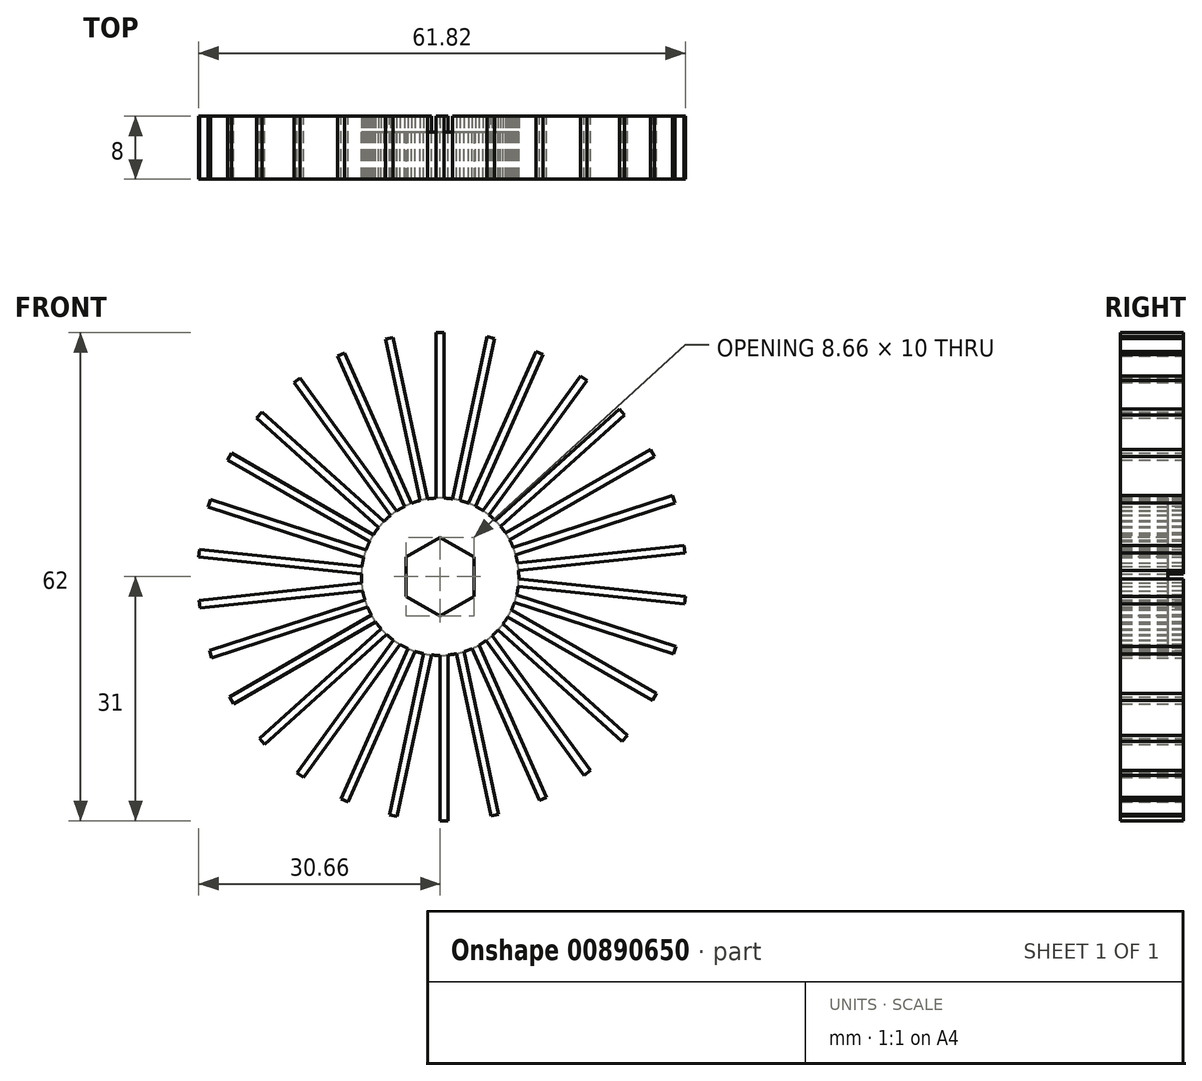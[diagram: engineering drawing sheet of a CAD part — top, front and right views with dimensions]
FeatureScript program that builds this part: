
annotation { "Feature Type Name" : "Feature", "Feature Type Description" : "" }
export const myFeature = defineFeature(function(context is Context, id is Id, definition is map)
    precondition{}
    {
        {
            var Q0;
            Q0=qCreatedBy(makeId("Front.planeOp"),FACE);
            var sketch = newSketch(context, id + "F0", { "sketchPlane" : qUnion([Q0])});
            skCircle(sketch, "E0", {"center": v(0, 0) * mm, "radius": 10 * mm});
            skCircle(sketch, "E1", {"center": v(0, 0) * mm, "radius": 5 * mm});
            skCircle(sketch, "E2.cCircle", {"center": v(0, 0) * mm, "radius": 5 * mm, "construction": true});
            skLineSegment(sketch, "E2.0", {"start": v(0, 5) * mm, "end": v(4.33, 2.5) * mm});
            skLineSegment(sketch, "E2.1", {"start": v(4.33, 2.5) * mm, "end": v(4.33, -2.5) * mm});
            skLineSegment(sketch, "E2.2", {"start": v(4.33, -2.5) * mm, "end": v(0, -5) * mm});
            skLineSegment(sketch, "E2.3", {"start": v(0, -5) * mm, "end": v(-4.33, -2.5) * mm});
            skLineSegment(sketch, "E2.4", {"start": v(-4.33, -2.5) * mm, "end": v(-4.33, 2.5) * mm});
            skLineSegment(sketch, "E2.5", {"start": v(-4.33, 2.5) * mm, "end": v(0, 5) * mm});
            skLineSegment(sketch, "E3", {"start": v(-0.5, 31) * mm, "end": v(0.5, 31) * mm});
            skLineSegment(sketch, "E4", {"start": v(0.5, 31) * mm, "end": v(0.5, 0) * mm});
            skLineSegment(sketch, "E5", {"start": v(-0.5, 31) * mm, "end": v(-0.5, 0) * mm});
            skLineSegment(sketch, "E6.1.0", {"start": v(-5.95, 30.37) * mm, "end": v(0.5, 0.05) * mm});
            skLineSegment(sketch, "E6.1.1", {"start": v(-6.93, 30.17) * mm, "end": v(-0.48, -0.16) * mm});
            skLineSegment(sketch, "E6.1.2", {"start": v(-6.93, 30.17) * mm, "end": v(-5.95, 30.37) * mm});
            skLineSegment(sketch, "E6.2.0", {"start": v(-12.13, 28.42) * mm, "end": v(0.48, 0.1) * mm});
            skLineSegment(sketch, "E6.2.1", {"start": v(-13.04, 28.01) * mm, "end": v(-0.44, -0.3) * mm});
            skLineSegment(sketch, "E6.2.2", {"start": v(-13.04, 28.01) * mm, "end": v(-12.13, 28.42) * mm});
            skLineSegment(sketch, "E6.3.0", {"start": v(-17.77, 25.23) * mm, "end": v(0.45, 0.15) * mm});
            skLineSegment(sketch, "E6.3.1", {"start": v(-18.58, 24.64) * mm, "end": v(-0.36, -0.44) * mm});
            skLineSegment(sketch, "E6.3.2", {"start": v(-18.58, 24.64) * mm, "end": v(-17.77, 25.23) * mm});
            skLineSegment(sketch, "E6.4.0", {"start": v(-22.62, 20.93) * mm, "end": v(0.42, 0.19) * mm});
            skLineSegment(sketch, "E6.4.1", {"start": v(-23.29, 20.19) * mm, "end": v(-0.25, -0.56) * mm});
            skLineSegment(sketch, "E6.4.2", {"start": v(-23.29, 20.19) * mm, "end": v(-22.62, 20.93) * mm});
            skLineSegment(sketch, "E6.5.0", {"start": v(-26.47, 15.72) * mm, "end": v(0.38, 0.22) * mm});
            skLineSegment(sketch, "E6.5.1", {"start": v(-26.97, 14.85) * mm, "end": v(-0.12, -0.65) * mm});
            skLineSegment(sketch, "E6.5.2", {"start": v(-26.97, 14.85) * mm, "end": v(-26.47, 15.72) * mm});
            skPoint(sketch, "E6.center", {"position": v(0.25, 0) * mm});
            skLineSegment(sketch, "E7.3.6.0", {"start": v(-29.46, 8.87) * mm, "end": v(0.02, -0.71) * mm});
            skLineSegment(sketch, "E7.5.6.0", {"start": v(-29.16, 9.82) * mm, "end": v(0.33, 0.24) * mm});
            skLineSegment(sketch, "E7.6.6.0", {"start": v(-29.46, 8.87) * mm, "end": v(-29.16, 9.82) * mm});
            skLineSegment(sketch, "E7.3.7.0", {"start": v(-30.66, 2.5) * mm, "end": v(0.17, -0.75) * mm});
            skLineSegment(sketch, "E7.5.7.0", {"start": v(-30.55, 3.49) * mm, "end": v(0.28, 0.25) * mm});
            skLineSegment(sketch, "E7.6.7.0", {"start": v(-30.66, 2.5) * mm, "end": v(-30.55, 3.49) * mm});
            skLineSegment(sketch, "E7.3.8.0", {"start": v(-30.5, -3.99) * mm, "end": v(0.33, -0.75) * mm});
            skLineSegment(sketch, "E7.5.8.0", {"start": v(-30.6, -3) * mm, "end": v(0.22, 0.25) * mm});
            skLineSegment(sketch, "E7.6.8.0", {"start": v(-30.5, -3.99) * mm, "end": v(-30.6, -3) * mm});
            skLineSegment(sketch, "E7.3.9.0", {"start": v(-29, -10.3) * mm, "end": v(0.48, -0.71) * mm});
            skLineSegment(sketch, "E7.5.9.0", {"start": v(-29.31, -9.34) * mm, "end": v(0.17, 0.24) * mm});
            skLineSegment(sketch, "E7.6.9.0", {"start": v(-29, -10.3) * mm, "end": v(-29.31, -9.34) * mm});
            skLineSegment(sketch, "E7.3.10.0", {"start": v(-26.22, -16.15) * mm, "end": v(0.63, -0.65) * mm});
            skLineSegment(sketch, "E7.5.10.0", {"start": v(-26.72, -15.28) * mm, "end": v(0.13, 0.22) * mm});
            skLineSegment(sketch, "E7.6.10.0", {"start": v(-26.22, -16.15) * mm, "end": v(-26.72, -15.28) * mm});
            skLineSegment(sketch, "E7.3.11.0", {"start": v(-22.29, -21.3) * mm, "end": v(0.75, -0.56) * mm});
            skLineSegment(sketch, "E7.5.11.0", {"start": v(-22.95, -20.56) * mm, "end": v(0.08, 0.19) * mm});
            skLineSegment(sketch, "E7.6.11.0", {"start": v(-22.29, -21.3) * mm, "end": v(-22.95, -20.56) * mm});
            skLineSegment(sketch, "E8.3.12.0", {"start": v(-17.36, -25.52) * mm, "end": v(0.86, -0.44) * mm});
            skLineSegment(sketch, "E8.5.12.0", {"start": v(-18.17, -24.93) * mm, "end": v(0.05, 0.15) * mm});
            skLineSegment(sketch, "E8.6.12.0", {"start": v(-17.36, -25.52) * mm, "end": v(-18.17, -24.93) * mm});
            skLineSegment(sketch, "E8.3.13.0", {"start": v(-11.67, -28.62) * mm, "end": v(0.94, -0.3) * mm});
            skLineSegment(sketch, "E8.5.13.0", {"start": v(-12.59, -28.22) * mm, "end": v(0.02, 0.1) * mm});
            skLineSegment(sketch, "E8.6.13.0", {"start": v(-11.67, -28.62) * mm, "end": v(-12.59, -28.22) * mm});
            skLineSegment(sketch, "E8.3.14.0", {"start": v(-5.46, -30.48) * mm, "end": v(0.98, -0.16) * mm});
            skLineSegment(sketch, "E8.5.14.0", {"start": v(-6.44, -30.27) * mm, "end": v(0, 0.05) * mm});
            skLineSegment(sketch, "E8.6.14.0", {"start": v(-5.46, -30.48) * mm, "end": v(-6.44, -30.27) * mm});
            skLineSegment(sketch, "E8.3.15.0", {"start": v(1, -31) * mm, "end": v(1, 0) * mm});
            skLineSegment(sketch, "E8.5.15.0", {"start": v(0, -31) * mm, "end": v(0, 0) * mm});
            skLineSegment(sketch, "E8.6.15.0", {"start": v(1, -31) * mm, "end": v(0, -31) * mm});
            skLineSegment(sketch, "E8.3.16.0", {"start": v(7.43, -30.17) * mm, "end": v(0.98, 0.16) * mm});
            skLineSegment(sketch, "E8.5.16.0", {"start": v(6.45, -30.37) * mm, "end": v(0, -0.05) * mm});
            skLineSegment(sketch, "E8.6.16.0", {"start": v(7.43, -30.17) * mm, "end": v(6.45, -30.37) * mm});
            skLineSegment(sketch, "E8.3.17.0", {"start": v(13.54, -28.01) * mm, "end": v(0.94, 0.3) * mm});
            skLineSegment(sketch, "E8.5.17.0", {"start": v(12.63, -28.42) * mm, "end": v(0.02, -0.1) * mm});
            skLineSegment(sketch, "E8.6.17.0", {"start": v(13.54, -28.01) * mm, "end": v(12.63, -28.42) * mm});
            skLineSegment(sketch, "E8.3.18.0", {"start": v(19.08, -24.64) * mm, "end": v(0.86, 0.44) * mm});
            skLineSegment(sketch, "E8.5.18.0", {"start": v(18.27, -25.23) * mm, "end": v(0.05, -0.15) * mm});
            skLineSegment(sketch, "E8.6.18.0", {"start": v(19.08, -24.64) * mm, "end": v(18.27, -25.23) * mm});
            skLineSegment(sketch, "E8.3.19.0", {"start": v(23.79, -20.19) * mm, "end": v(0.75, 0.56) * mm});
            skLineSegment(sketch, "E8.5.19.0", {"start": v(23.12, -20.93) * mm, "end": v(0.08, -0.19) * mm});
            skLineSegment(sketch, "E8.6.19.0", {"start": v(23.79, -20.19) * mm, "end": v(23.12, -20.93) * mm});
            skLineSegment(sketch, "E8.3.20.0", {"start": v(27.47, -14.85) * mm, "end": v(0.63, 0.65) * mm});
            skLineSegment(sketch, "E8.5.20.0", {"start": v(26.97, -15.72) * mm, "end": v(0.13, -0.22) * mm});
            skLineSegment(sketch, "E8.6.20.0", {"start": v(27.47, -14.85) * mm, "end": v(26.97, -15.72) * mm});
            skLineSegment(sketch, "E8.3.21.0", {"start": v(29.96, -8.87) * mm, "end": v(0.48, 0.71) * mm});
            skLineSegment(sketch, "E8.5.21.0", {"start": v(29.66, -9.82) * mm, "end": v(0.17, -0.24) * mm});
            skLineSegment(sketch, "E8.6.21.0", {"start": v(29.96, -8.87) * mm, "end": v(29.66, -9.82) * mm});
            skLineSegment(sketch, "E8.3.22.0", {"start": v(31.16, -2.5) * mm, "end": v(0.33, 0.75) * mm});
            skLineSegment(sketch, "E8.5.22.0", {"start": v(31.05, -3.49) * mm, "end": v(0.22, -0.25) * mm});
            skLineSegment(sketch, "E8.6.22.0", {"start": v(31.16, -2.5) * mm, "end": v(31.05, -3.49) * mm});
            skLineSegment(sketch, "E8.3.23.0", {"start": v(31, 3.99) * mm, "end": v(0.17, 0.75) * mm});
            skLineSegment(sketch, "E8.5.23.0", {"start": v(31.1, 3) * mm, "end": v(0.28, -0.25) * mm});
            skLineSegment(sketch, "E8.6.23.0", {"start": v(31, 3.99) * mm, "end": v(31.1, 3) * mm});
            skLineSegment(sketch, "E9.3.24.0", {"start": v(29.5, 10.3) * mm, "end": v(0.02, 0.71) * mm});
            skLineSegment(sketch, "E9.5.24.0", {"start": v(29.81, 9.34) * mm, "end": v(0.33, -0.24) * mm});
            skLineSegment(sketch, "E9.6.24.0", {"start": v(29.5, 10.3) * mm, "end": v(29.81, 9.34) * mm});
            skLineSegment(sketch, "E9.3.25.0", {"start": v(26.72, 16.15) * mm, "end": v(-0.12, 0.65) * mm});
            skLineSegment(sketch, "E9.5.25.0", {"start": v(27.22, 15.28) * mm, "end": v(0.38, -0.22) * mm});
            skLineSegment(sketch, "E9.6.25.0", {"start": v(26.72, 16.15) * mm, "end": v(27.22, 15.28) * mm});
            skLineSegment(sketch, "E9.3.26.0", {"start": v(22.79, 21.3) * mm, "end": v(-0.25, 0.56) * mm});
            skLineSegment(sketch, "E9.5.26.0", {"start": v(23.45, 20.56) * mm, "end": v(0.42, -0.19) * mm});
            skLineSegment(sketch, "E9.6.26.0", {"start": v(22.79, 21.3) * mm, "end": v(23.45, 20.56) * mm});
            skLineSegment(sketch, "E9.3.27.0", {"start": v(17.86, 25.52) * mm, "end": v(-0.36, 0.44) * mm});
            skLineSegment(sketch, "E9.5.27.0", {"start": v(18.67, 24.93) * mm, "end": v(0.45, -0.15) * mm});
            skLineSegment(sketch, "E9.6.27.0", {"start": v(17.86, 25.52) * mm, "end": v(18.67, 24.93) * mm});
            skLineSegment(sketch, "E9.3.28.0", {"start": v(12.17, 28.62) * mm, "end": v(-0.44, 0.3) * mm});
            skLineSegment(sketch, "E9.5.28.0", {"start": v(13.09, 28.22) * mm, "end": v(0.48, -0.1) * mm});
            skLineSegment(sketch, "E9.6.28.0", {"start": v(12.17, 28.62) * mm, "end": v(13.09, 28.22) * mm});
            skLineSegment(sketch, "E9.3.29.0", {"start": v(5.96, 30.48) * mm, "end": v(-0.48, 0.16) * mm});
            skLineSegment(sketch, "E9.5.29.0", {"start": v(6.94, 30.27) * mm, "end": v(0.5, -0.05) * mm});
            skLineSegment(sketch, "E9.6.29.0", {"start": v(5.96, 30.48) * mm, "end": v(6.94, 30.27) * mm});
            skSolve(sketch);
        }
        {
            var Q0;
            {var subQ5=sQuery(id+"F0.wireOp",EDGE,"E7.6.8.0");Q0=makeQuery(id+"F0.imprint","IMPRINT",FACE,{"disambiguationData":[TD([[makeQuery(id+"F0.imprint","IMPRINT",EDGE,{"derivedFrom":subQ5}),-1.0]])]});}
            var Q1;
            {var subQ5=sQuery(id+"F0.wireOp",EDGE,"E7.6.6.0");Q1=makeQuery(id+"F0.imprint","IMPRINT",FACE,{"disambiguationData":[TD([[makeQuery(id+"F0.imprint","IMPRINT",EDGE,{"derivedFrom":subQ5}),-1.0]])]});}
            var Q2;
            {var subQ5=sQuery(id+"F0.wireOp",EDGE,"E7.6.7.0");Q2=makeQuery(id+"F0.imprint","IMPRINT",FACE,{"disambiguationData":[TD([[makeQuery(id+"F0.imprint","IMPRINT",EDGE,{"derivedFrom":subQ5}),-1.0]])]});}
            var Q3;
            {var subQ5=sQuery(id+"F0.wireOp",EDGE,"E8.6.23.0");Q3=makeQuery(id+"F0.imprint","IMPRINT",FACE,{"disambiguationData":[TD([[makeQuery(id+"F0.imprint","IMPRINT",EDGE,{"derivedFrom":subQ5}),-1.0]])]});}
            var Q4;
            {var subQ5=sQuery(id+"F0.wireOp",EDGE,"E9.6.24.0");Q4=makeQuery(id+"F0.imprint","IMPRINT",FACE,{"disambiguationData":[TD([[makeQuery(id+"F0.imprint","IMPRINT",EDGE,{"derivedFrom":subQ5}),-1.0]])]});}
            var Q5;
            {var subQ5=sQuery(id+"F0.wireOp",EDGE,"E9.6.25.0");Q5=makeQuery(id+"F0.imprint","IMPRINT",FACE,{"disambiguationData":[TD([[makeQuery(id+"F0.imprint","IMPRINT",EDGE,{"derivedFrom":subQ5}),-1.0]])]});}
            var Q6;
            {var subQ5=sQuery(id+"F0.wireOp",EDGE,"E9.6.26.0");Q6=makeQuery(id+"F0.imprint","IMPRINT",FACE,{"disambiguationData":[TD([[makeQuery(id+"F0.imprint","IMPRINT",EDGE,{"derivedFrom":subQ5}),-1.0]])]});}
            var Q7;
            {var subQ5=sQuery(id+"F0.wireOp",EDGE,"E9.6.27.0");Q7=makeQuery(id+"F0.imprint","IMPRINT",FACE,{"disambiguationData":[TD([[makeQuery(id+"F0.imprint","IMPRINT",EDGE,{"derivedFrom":subQ5}),-1.0]])]});}
            var Q8;
            {var subQ5=sQuery(id+"F0.wireOp",EDGE,"E9.6.28.0");Q8=makeQuery(id+"F0.imprint","IMPRINT",FACE,{"disambiguationData":[TD([[makeQuery(id+"F0.imprint","IMPRINT",EDGE,{"derivedFrom":subQ5}),-1.0]])]});}
            var Q9;
            {var subQ5=sQuery(id+"F0.wireOp",EDGE,"E9.6.29.0");Q9=makeQuery(id+"F0.imprint","IMPRINT",FACE,{"disambiguationData":[TD([[makeQuery(id+"F0.imprint","IMPRINT",EDGE,{"derivedFrom":subQ5}),-1.0]])]});}
            var Q10;
            {var subQ5=sQuery(id+"F0.wireOp",EDGE,"E3");Q10=makeQuery(id+"F0.imprint","IMPRINT",FACE,{"disambiguationData":[TD([[makeQuery(id+"F0.imprint","IMPRINT",EDGE,{"derivedFrom":subQ5}),-1.0]])]});}
            var Q11;
            {var subQ5=sQuery(id+"F0.wireOp",EDGE,"E6.1.2");Q11=makeQuery(id+"F0.imprint","IMPRINT",FACE,{"disambiguationData":[TD([[makeQuery(id+"F0.imprint","IMPRINT",EDGE,{"derivedFrom":subQ5}),-1.0]])]});}
            var Q12;
            {var subQ5=sQuery(id+"F0.wireOp",EDGE,"E6.2.2");Q12=makeQuery(id+"F0.imprint","IMPRINT",FACE,{"disambiguationData":[TD([[makeQuery(id+"F0.imprint","IMPRINT",EDGE,{"derivedFrom":subQ5}),-1.0]])]});}
            var Q13;
            {var subQ5=sQuery(id+"F0.wireOp",EDGE,"E6.3.2");Q13=makeQuery(id+"F0.imprint","IMPRINT",FACE,{"disambiguationData":[TD([[makeQuery(id+"F0.imprint","IMPRINT",EDGE,{"derivedFrom":subQ5}),-1.0]])]});}
            var Q14;
            {var subQ5=sQuery(id+"F0.wireOp",EDGE,"E6.4.2");Q14=makeQuery(id+"F0.imprint","IMPRINT",FACE,{"disambiguationData":[TD([[makeQuery(id+"F0.imprint","IMPRINT",EDGE,{"derivedFrom":subQ5}),-1.0]])]});}
            var Q15;
            {var subQ5=sQuery(id+"F0.wireOp",EDGE,"E6.5.2");Q15=makeQuery(id+"F0.imprint","IMPRINT",FACE,{"disambiguationData":[TD([[makeQuery(id+"F0.imprint","IMPRINT",EDGE,{"derivedFrom":subQ5}),-1.0]])]});}
            var Q16;
            {var subQ0=sQuery(id+"F0.wireOp",EDGE,"E7.3.6.0");var subQ1=sQuery(id+"F0.wireOp",EDGE,"E0");var subQ2=makeQuery(id+"F0.imprint","INTERSECT",VERTEX,{"derivedFrom":[subQ1,subQ0]});Q16=makeQuery(id+"F0.imprint","IMPRINT",FACE,{"disambiguationData":[TD([[makeQuery(id+"F0.imprint","IMPRINT",EDGE,{"disambiguationData":[TD([[subQ2,-1.0]])],"derivedFrom":subQ1}),1.0]])]});}
            var Q17;
            {var subQ0=sQuery(id+"F0.wireOp",EDGE,"E7.5.6.0");var subQ1=sQuery(id+"F0.wireOp",EDGE,"E0");var subQ2=makeQuery(id+"F0.imprint","INTERSECT",VERTEX,{"derivedFrom":[subQ1,subQ0]});Q17=makeQuery(id+"F0.imprint","IMPRINT",FACE,{"disambiguationData":[TD([[makeQuery(id+"F0.imprint","IMPRINT",EDGE,{"disambiguationData":[TD([[subQ2,-1.0]])],"derivedFrom":subQ1}),1.0]])]});}
            var Q18;
            {var subQ0=sQuery(id+"F0.wireOp",EDGE,"E4");var subQ1=sQuery(id+"F0.wireOp",EDGE,"E0");var subQ2=makeQuery(id+"F0.imprint","INTERSECT",VERTEX,{"derivedFrom":[subQ1,subQ0]});Q18=makeQuery(id+"F0.imprint","IMPRINT",FACE,{"disambiguationData":[TD([[makeQuery(id+"F0.imprint","IMPRINT",EDGE,{"disambiguationData":[TD([[subQ2,-1.0]])],"derivedFrom":subQ1}),1.0]])]});}
            var Q19;
            {var subQ5=sQuery(id+"F0.wireOp",EDGE,"E8.6.22.0");Q19=makeQuery(id+"F0.imprint","IMPRINT",FACE,{"disambiguationData":[TD([[makeQuery(id+"F0.imprint","IMPRINT",EDGE,{"derivedFrom":subQ5}),-1.0]])]});}
            var Q20;
            {var subQ0=sQuery(id+"F0.wireOp",EDGE,"E6.4.1");var subQ1=sQuery(id+"F0.wireOp",EDGE,"E0");var subQ2=makeQuery(id+"F0.imprint","INTERSECT",VERTEX,{"derivedFrom":[subQ1,subQ0]});Q20=makeQuery(id+"F0.imprint","IMPRINT",FACE,{"disambiguationData":[TD([[makeQuery(id+"F0.imprint","IMPRINT",EDGE,{"disambiguationData":[TD([[subQ2,-1.0]])],"derivedFrom":subQ1}),1.0]])]});}
            var Q21;
            {var subQ0=sQuery(id+"F0.wireOp",EDGE,"E6.3.0");var subQ1=sQuery(id+"F0.wireOp",EDGE,"E0");var subQ2=makeQuery(id+"F0.imprint","INTERSECT",VERTEX,{"derivedFrom":[subQ1,subQ0]});Q21=makeQuery(id+"F0.imprint","IMPRINT",FACE,{"disambiguationData":[TD([[makeQuery(id+"F0.imprint","IMPRINT",EDGE,{"disambiguationData":[TD([[subQ2,-1.0]])],"derivedFrom":subQ1}),1.0]])]});}
            var Q22;
            {var subQ0=sQuery(id+"F0.wireOp",EDGE,"E6.5.1");var subQ1=sQuery(id+"F0.wireOp",EDGE,"E0");var subQ2=makeQuery(id+"F0.imprint","INTERSECT",VERTEX,{"derivedFrom":[subQ1,subQ0]});Q22=makeQuery(id+"F0.imprint","IMPRINT",FACE,{"disambiguationData":[TD([[makeQuery(id+"F0.imprint","IMPRINT",EDGE,{"disambiguationData":[TD([[subQ2,-1.0]])],"derivedFrom":subQ1}),1.0]])]});}
            var Q23;
            {var subQ0=sQuery(id+"F0.wireOp",EDGE,"E6.4.0");var subQ1=sQuery(id+"F0.wireOp",EDGE,"E0");var subQ2=makeQuery(id+"F0.imprint","INTERSECT",VERTEX,{"derivedFrom":[subQ1,subQ0]});Q23=makeQuery(id+"F0.imprint","IMPRINT",FACE,{"disambiguationData":[TD([[makeQuery(id+"F0.imprint","IMPRINT",EDGE,{"disambiguationData":[TD([[subQ2,-1.0]])],"derivedFrom":subQ1}),1.0]])]});}
            var Q24;
            {var subQ5=sQuery(id+"F0.wireOp",EDGE,"E7.6.9.0");Q24=makeQuery(id+"F0.imprint","IMPRINT",FACE,{"disambiguationData":[TD([[makeQuery(id+"F0.imprint","IMPRINT",EDGE,{"derivedFrom":subQ5}),-1.0]])]});}
            var Q25;
            {var subQ0=sQuery(id+"F0.wireOp",EDGE,"E7.3.7.0");var subQ1=sQuery(id+"F0.wireOp",EDGE,"E0");var subQ2=makeQuery(id+"F0.imprint","INTERSECT",VERTEX,{"derivedFrom":[subQ1,subQ0]});Q25=makeQuery(id+"F0.imprint","IMPRINT",FACE,{"disambiguationData":[TD([[makeQuery(id+"F0.imprint","IMPRINT",EDGE,{"disambiguationData":[TD([[subQ2,-1.0]])],"derivedFrom":subQ1}),1.0]])]});}
            var Q26;
            {var subQ0=sQuery(id+"F0.wireOp",EDGE,"E6.5.0");var subQ1=sQuery(id+"F0.wireOp",EDGE,"E0");var subQ2=makeQuery(id+"F0.imprint","INTERSECT",VERTEX,{"derivedFrom":[subQ1,subQ0]});Q26=makeQuery(id+"F0.imprint","IMPRINT",FACE,{"disambiguationData":[TD([[makeQuery(id+"F0.imprint","IMPRINT",EDGE,{"disambiguationData":[TD([[subQ2,-1.0]])],"derivedFrom":subQ1}),1.0]])]});}
            var Q27;
            {var subQ5=sQuery(id+"F0.wireOp",EDGE,"E7.6.10.0");Q27=makeQuery(id+"F0.imprint","IMPRINT",FACE,{"disambiguationData":[TD([[makeQuery(id+"F0.imprint","IMPRINT",EDGE,{"derivedFrom":subQ5}),-1.0]])]});}
            var Q28;
            {var subQ0=sQuery(id+"F0.wireOp",EDGE,"E7.5.8.0");var subQ1=sQuery(id+"F0.wireOp",EDGE,"E0");var subQ2=makeQuery(id+"F0.imprint","INTERSECT",VERTEX,{"derivedFrom":[subQ1,subQ0]});Q28=makeQuery(id+"F0.imprint","IMPRINT",FACE,{"disambiguationData":[TD([[makeQuery(id+"F0.imprint","IMPRINT",EDGE,{"disambiguationData":[TD([[subQ2,-1.0]])],"derivedFrom":subQ1}),1.0]])]});}
            var Q29;
            {var subQ1=sQuery(id+"F0.wireOp",EDGE,"E0");var subQ5=sQuery(id+"F0.wireOp",EDGE,"E7.5.10.0");var subQ6=makeQuery(id+"F0.imprint","INTERSECT",VERTEX,{"derivedFrom":[subQ1,subQ5]});Q29=makeQuery(id+"F0.imprint","IMPRINT",FACE,{"disambiguationData":[TD([[makeQuery(id+"F0.imprint","IMPRINT",EDGE,{"disambiguationData":[TD([[subQ6,-1.0]])],"derivedFrom":subQ1}),1.0]])]});}
            var Q30;
            {var subQ5=sQuery(id+"F0.wireOp",EDGE,"E7.6.11.0");Q30=makeQuery(id+"F0.imprint","IMPRINT",FACE,{"disambiguationData":[TD([[makeQuery(id+"F0.imprint","IMPRINT",EDGE,{"derivedFrom":subQ5}),-1.0]])]});}
            var Q31;
            {var subQ0=sQuery(id+"F0.wireOp",EDGE,"E7.3.9.0");var subQ1=sQuery(id+"F0.wireOp",EDGE,"E0");var subQ2=makeQuery(id+"F0.imprint","INTERSECT",VERTEX,{"derivedFrom":[subQ1,subQ0]});Q31=makeQuery(id+"F0.imprint","IMPRINT",FACE,{"disambiguationData":[TD([[makeQuery(id+"F0.imprint","IMPRINT",EDGE,{"disambiguationData":[TD([[subQ2,-1.0]])],"derivedFrom":subQ1}),1.0]])]});}
            var Q32;
            {var subQ0=sQuery(id+"F0.wireOp",EDGE,"E7.5.9.0");var subQ1=sQuery(id+"F0.wireOp",EDGE,"E0");var subQ2=makeQuery(id+"F0.imprint","INTERSECT",VERTEX,{"derivedFrom":[subQ1,subQ0]});Q32=makeQuery(id+"F0.imprint","IMPRINT",FACE,{"disambiguationData":[TD([[makeQuery(id+"F0.imprint","IMPRINT",EDGE,{"disambiguationData":[TD([[subQ2,-1.0]])],"derivedFrom":subQ1}),1.0]])]});}
            var Q33;
            {var subQ1=sQuery(id+"F0.wireOp",EDGE,"E0");var subQ5=sQuery(id+"F0.wireOp",EDGE,"E8.5.19.0");var subQ6=makeQuery(id+"F0.imprint","INTERSECT",VERTEX,{"derivedFrom":[subQ1,subQ5]});Q33=makeQuery(id+"F0.imprint","IMPRINT",FACE,{"disambiguationData":[TD([[makeQuery(id+"F0.imprint","IMPRINT",EDGE,{"disambiguationData":[TD([[subQ6,-1.0]])],"derivedFrom":subQ1}),1.0]])]});}
            var Q34;
            {var subQ5=sQuery(id+"F0.wireOp",EDGE,"E8.6.12.0");Q34=makeQuery(id+"F0.imprint","IMPRINT",FACE,{"disambiguationData":[TD([[makeQuery(id+"F0.imprint","IMPRINT",EDGE,{"derivedFrom":subQ5}),-1.0]])]});}
            var Q35;
            {var subQ7=sQuery(id+"F0.wireOp",EDGE,"E8.3.23.0");var subQ8=sQuery(id+"F0.wireOp",EDGE,"E0");var subQ9=makeQuery(id+"F0.imprint","INTERSECT",VERTEX,{"derivedFrom":[subQ8,subQ7]});Q35=makeQuery(id+"F0.imprint","IMPRINT",FACE,{"disambiguationData":[TD([[makeQuery(id+"F0.imprint","IMPRINT",EDGE,{"disambiguationData":[TD([[subQ9,1.0]])],"derivedFrom":subQ8}),1.0]])]});}
            var Q36;
            {var subQ5=sQuery(id+"F0.wireOp",EDGE,"E8.6.13.0");Q36=makeQuery(id+"F0.imprint","IMPRINT",FACE,{"disambiguationData":[TD([[makeQuery(id+"F0.imprint","IMPRINT",EDGE,{"derivedFrom":subQ5}),-1.0]])]});}
            var Q37;
            {var subQ0=sQuery(id+"F0.wireOp",EDGE,"E8.5.12.0");var subQ1=sQuery(id+"F0.wireOp",EDGE,"E0");var subQ2=makeQuery(id+"F0.imprint","INTERSECT",VERTEX,{"derivedFrom":[subQ1,subQ0]});Q37=makeQuery(id+"F0.imprint","IMPRINT",FACE,{"disambiguationData":[TD([[makeQuery(id+"F0.imprint","IMPRINT",EDGE,{"disambiguationData":[TD([[subQ2,-1.0]])],"derivedFrom":subQ1}),1.0]])]});}
            var Q38;
            {var subQ1=sQuery(id+"F0.wireOp",EDGE,"E0");var subQ8=sQuery(id+"F0.wireOp",EDGE,"E9.5.24.0");var subQ11=makeQuery(id+"F0.imprint","INTERSECT",VERTEX,{"derivedFrom":[subQ1,subQ8]});Q38=makeQuery(id+"F0.imprint","IMPRINT",FACE,{"disambiguationData":[TD([[makeQuery(id+"F0.imprint","IMPRINT",EDGE,{"disambiguationData":[TD([[subQ11,-1.0]])],"derivedFrom":subQ1}),1.0]])]});}
            var Q39;
            {var subQ5=sQuery(id+"F0.wireOp",EDGE,"E8.6.14.0");Q39=makeQuery(id+"F0.imprint","IMPRINT",FACE,{"disambiguationData":[TD([[makeQuery(id+"F0.imprint","IMPRINT",EDGE,{"derivedFrom":subQ5}),-1.0]])]});}
            var Q40;
            {var subQ0=sQuery(id+"F0.wireOp",EDGE,"E8.3.12.0");var subQ1=sQuery(id+"F0.wireOp",EDGE,"E0");var subQ2=makeQuery(id+"F0.imprint","INTERSECT",VERTEX,{"derivedFrom":[subQ1,subQ0]});Q40=makeQuery(id+"F0.imprint","IMPRINT",FACE,{"disambiguationData":[TD([[makeQuery(id+"F0.imprint","IMPRINT",EDGE,{"disambiguationData":[TD([[subQ2,-1.0]])],"derivedFrom":subQ1}),1.0]])]});}
            var Q41;
            {var subQ0=sQuery(id+"F0.wireOp",EDGE,"E8.5.13.0");var subQ1=sQuery(id+"F0.wireOp",EDGE,"E0");var subQ2=makeQuery(id+"F0.imprint","INTERSECT",VERTEX,{"derivedFrom":[subQ1,subQ0]});Q41=makeQuery(id+"F0.imprint","IMPRINT",FACE,{"disambiguationData":[TD([[makeQuery(id+"F0.imprint","IMPRINT",EDGE,{"disambiguationData":[TD([[subQ2,-1.0]])],"derivedFrom":subQ1}),1.0]])]});}
            var Q42;
            {var subQ3=sQuery(id+"F0.wireOp",EDGE,"E9.5.25.0");var subQ8=sQuery(id+"F0.wireOp",EDGE,"E0");var subQ9=makeQuery(id+"F0.imprint","INTERSECT",VERTEX,{"derivedFrom":[subQ8,subQ3]});Q42=makeQuery(id+"F0.imprint","IMPRINT",FACE,{"disambiguationData":[TD([[makeQuery(id+"F0.imprint","IMPRINT",EDGE,{"disambiguationData":[TD([[subQ9,-1.0]])],"derivedFrom":subQ8}),1.0]])]});}
            var Q43;
            {var subQ5=sQuery(id+"F0.wireOp",EDGE,"E8.6.15.0");Q43=makeQuery(id+"F0.imprint","IMPRINT",FACE,{"disambiguationData":[TD([[makeQuery(id+"F0.imprint","IMPRINT",EDGE,{"derivedFrom":subQ5}),-1.0]])]});}
            var Q44;
            {var subQ0=sQuery(id+"F0.wireOp",EDGE,"E8.5.14.0");var subQ1=sQuery(id+"F0.wireOp",EDGE,"E0");var subQ2=makeQuery(id+"F0.imprint","INTERSECT",VERTEX,{"derivedFrom":[subQ1,subQ0]});Q44=makeQuery(id+"F0.imprint","IMPRINT",FACE,{"disambiguationData":[TD([[makeQuery(id+"F0.imprint","IMPRINT",EDGE,{"disambiguationData":[TD([[subQ2,-1.0]])],"derivedFrom":subQ1}),1.0]])]});}
            var Q45;
            {var subQ1=sQuery(id+"F0.wireOp",EDGE,"E0");var subQ9=sQuery(id+"F0.wireOp",EDGE,"E8.5.21.0");var subQ10=makeQuery(id+"F0.imprint","INTERSECT",VERTEX,{"derivedFrom":[subQ1,subQ9]});Q45=makeQuery(id+"F0.imprint","IMPRINT",FACE,{"disambiguationData":[TD([[makeQuery(id+"F0.imprint","IMPRINT",EDGE,{"disambiguationData":[TD([[subQ10,-1.0]])],"derivedFrom":subQ1}),1.0]])]});}
            var Q46;
            {var subQ5=sQuery(id+"F0.wireOp",EDGE,"E8.6.16.0");Q46=makeQuery(id+"F0.imprint","IMPRINT",FACE,{"disambiguationData":[TD([[makeQuery(id+"F0.imprint","IMPRINT",EDGE,{"derivedFrom":subQ5}),-1.0]])]});}
            var Q47;
            {var subQ0=sQuery(id+"F0.wireOp",EDGE,"E9.3.28.0");var subQ1=sQuery(id+"F0.wireOp",EDGE,"E0");var subQ2=makeQuery(id+"F0.imprint","INTERSECT",VERTEX,{"derivedFrom":[subQ1,subQ0]});Q47=makeQuery(id+"F0.imprint","IMPRINT",FACE,{"disambiguationData":[TD([[makeQuery(id+"F0.imprint","IMPRINT",EDGE,{"disambiguationData":[TD([[subQ2,-1.0]])],"derivedFrom":subQ1}),1.0]])]});}
            var Q48;
            {var subQ0=sQuery(id+"F0.wireOp",EDGE,"E8.3.14.0");var subQ1=sQuery(id+"F0.wireOp",EDGE,"E0");var subQ2=makeQuery(id+"F0.imprint","INTERSECT",VERTEX,{"derivedFrom":[subQ1,subQ0]});Q48=makeQuery(id+"F0.imprint","IMPRINT",FACE,{"disambiguationData":[TD([[makeQuery(id+"F0.imprint","IMPRINT",EDGE,{"disambiguationData":[TD([[subQ2,-1.0]])],"derivedFrom":subQ1}),1.0]])]});}
            var Q49;
            {var subQ0=sQuery(id+"F0.wireOp",EDGE,"E8.5.15.0");var subQ1=sQuery(id+"F0.wireOp",EDGE,"E0");var subQ2=makeQuery(id+"F0.imprint","INTERSECT",VERTEX,{"derivedFrom":[subQ1,subQ0]});Q49=makeQuery(id+"F0.imprint","IMPRINT",FACE,{"disambiguationData":[TD([[makeQuery(id+"F0.imprint","IMPRINT",EDGE,{"disambiguationData":[TD([[subQ2,-1.0]])],"derivedFrom":subQ1}),1.0]])]});}
            var Q50;
            {var subQ1=sQuery(id+"F0.wireOp",EDGE,"E0");var subQ9=sQuery(id+"F0.wireOp",EDGE,"E8.5.22.0");var subQ10=makeQuery(id+"F0.imprint","INTERSECT",VERTEX,{"derivedFrom":[subQ1,subQ9]});Q50=makeQuery(id+"F0.imprint","IMPRINT",FACE,{"disambiguationData":[TD([[makeQuery(id+"F0.imprint","IMPRINT",EDGE,{"disambiguationData":[TD([[subQ10,-1.0]])],"derivedFrom":subQ1}),1.0]])]});}
            var Q51;
            {var subQ5=sQuery(id+"F0.wireOp",EDGE,"E8.6.17.0");Q51=makeQuery(id+"F0.imprint","IMPRINT",FACE,{"disambiguationData":[TD([[makeQuery(id+"F0.imprint","IMPRINT",EDGE,{"derivedFrom":subQ5}),-1.0]])]});}
            var Q52;
            {var subQ0=sQuery(id+"F0.wireOp",EDGE,"E9.5.27.0");var subQ1=sQuery(id+"F0.wireOp",EDGE,"E0");var subQ2=makeQuery(id+"F0.imprint","INTERSECT",VERTEX,{"derivedFrom":[subQ1,subQ0]});Q52=makeQuery(id+"F0.imprint","IMPRINT",FACE,{"disambiguationData":[TD([[makeQuery(id+"F0.imprint","IMPRINT",EDGE,{"disambiguationData":[TD([[subQ2,-1.0]])],"derivedFrom":subQ1}),1.0]])]});}
            var Q53;
            {var subQ0=sQuery(id+"F0.wireOp",EDGE,"E8.5.16.0");var subQ1=sQuery(id+"F0.wireOp",EDGE,"E0");var subQ2=makeQuery(id+"F0.imprint","INTERSECT",VERTEX,{"derivedFrom":[subQ1,subQ0]});Q53=makeQuery(id+"F0.imprint","IMPRINT",FACE,{"disambiguationData":[TD([[makeQuery(id+"F0.imprint","IMPRINT",EDGE,{"disambiguationData":[TD([[subQ2,-1.0]])],"derivedFrom":subQ1}),1.0]])]});}
            var Q54;
            {var subQ5=sQuery(id+"F0.wireOp",EDGE,"E8.6.18.0");Q54=makeQuery(id+"F0.imprint","IMPRINT",FACE,{"disambiguationData":[TD([[makeQuery(id+"F0.imprint","IMPRINT",EDGE,{"derivedFrom":subQ5}),-1.0]])]});}
            var Q55;
            {var subQ0=sQuery(id+"F0.wireOp",EDGE,"E8.3.16.0");var subQ1=sQuery(id+"F0.wireOp",EDGE,"E0");var subQ2=makeQuery(id+"F0.imprint","INTERSECT",VERTEX,{"derivedFrom":[subQ1,subQ0]});Q55=makeQuery(id+"F0.imprint","IMPRINT",FACE,{"disambiguationData":[TD([[makeQuery(id+"F0.imprint","IMPRINT",EDGE,{"disambiguationData":[TD([[subQ2,-1.0]])],"derivedFrom":subQ1}),1.0]])]});}
            var Q56;
            {var subQ0=sQuery(id+"F0.wireOp",EDGE,"E9.5.28.0");var subQ1=sQuery(id+"F0.wireOp",EDGE,"E0");var subQ2=makeQuery(id+"F0.imprint","INTERSECT",VERTEX,{"derivedFrom":[subQ1,subQ0]});Q56=makeQuery(id+"F0.imprint","IMPRINT",FACE,{"disambiguationData":[TD([[makeQuery(id+"F0.imprint","IMPRINT",EDGE,{"disambiguationData":[TD([[subQ2,-1.0]])],"derivedFrom":subQ1}),1.0]])]});}
            var Q57;
            {var subQ0=sQuery(id+"F0.wireOp",EDGE,"E8.5.17.0");var subQ1=sQuery(id+"F0.wireOp",EDGE,"E0");var subQ2=makeQuery(id+"F0.imprint","INTERSECT",VERTEX,{"derivedFrom":[subQ1,subQ0]});Q57=makeQuery(id+"F0.imprint","IMPRINT",FACE,{"disambiguationData":[TD([[makeQuery(id+"F0.imprint","IMPRINT",EDGE,{"disambiguationData":[TD([[subQ2,-1.0]])],"derivedFrom":subQ1}),1.0]])]});}
            var Q58;
            {var subQ5=sQuery(id+"F0.wireOp",EDGE,"E8.6.19.0");Q58=makeQuery(id+"F0.imprint","IMPRINT",FACE,{"disambiguationData":[TD([[makeQuery(id+"F0.imprint","IMPRINT",EDGE,{"derivedFrom":subQ5}),-1.0]])]});}
            var Q59;
            {var subQ0=sQuery(id+"F0.wireOp",EDGE,"E8.5.18.0");var subQ1=sQuery(id+"F0.wireOp",EDGE,"E0");var subQ2=makeQuery(id+"F0.imprint","INTERSECT",VERTEX,{"derivedFrom":[subQ1,subQ0]});Q59=makeQuery(id+"F0.imprint","IMPRINT",FACE,{"disambiguationData":[TD([[makeQuery(id+"F0.imprint","IMPRINT",EDGE,{"disambiguationData":[TD([[subQ2,-1.0]])],"derivedFrom":subQ1}),1.0]])]});}
            var Q60;
            {var subQ5=sQuery(id+"F0.wireOp",EDGE,"E8.6.20.0");Q60=makeQuery(id+"F0.imprint","IMPRINT",FACE,{"disambiguationData":[TD([[makeQuery(id+"F0.imprint","IMPRINT",EDGE,{"derivedFrom":subQ5}),-1.0]])]});}
            var Q61;
            {var subQ0=sQuery(id+"F0.wireOp",EDGE,"E8.3.18.0");var subQ1=sQuery(id+"F0.wireOp",EDGE,"E0");var subQ2=makeQuery(id+"F0.imprint","INTERSECT",VERTEX,{"derivedFrom":[subQ1,subQ0]});Q61=makeQuery(id+"F0.imprint","IMPRINT",FACE,{"disambiguationData":[TD([[makeQuery(id+"F0.imprint","IMPRINT",EDGE,{"disambiguationData":[TD([[subQ2,-1.0]])],"derivedFrom":subQ1}),1.0]])]});}
            var Q62;
            {var subQ0=sQuery(id+"F0.wireOp",EDGE,"E6.1.0");var subQ1=sQuery(id+"F0.wireOp",EDGE,"E0");var subQ2=makeQuery(id+"F0.imprint","INTERSECT",VERTEX,{"derivedFrom":[subQ1,subQ0]});Q62=makeQuery(id+"F0.imprint","IMPRINT",FACE,{"disambiguationData":[TD([[makeQuery(id+"F0.imprint","IMPRINT",EDGE,{"disambiguationData":[TD([[subQ2,-1.0]])],"derivedFrom":subQ1}),1.0]])]});}
            var Q63;
            {var subQ5=sQuery(id+"F0.wireOp",EDGE,"E8.6.21.0");Q63=makeQuery(id+"F0.imprint","IMPRINT",FACE,{"disambiguationData":[TD([[makeQuery(id+"F0.imprint","IMPRINT",EDGE,{"derivedFrom":subQ5}),-1.0]])]});}
            var Q64;
            {var subQ0=sQuery(id+"F0.wireOp",EDGE,"E6.2.0");var subQ1=sQuery(id+"F0.wireOp",EDGE,"E0");var subQ2=makeQuery(id+"F0.imprint","INTERSECT",VERTEX,{"derivedFrom":[subQ1,subQ0]});Q64=makeQuery(id+"F0.imprint","IMPRINT",FACE,{"disambiguationData":[TD([[makeQuery(id+"F0.imprint","IMPRINT",EDGE,{"disambiguationData":[TD([[subQ2,-1.0]])],"derivedFrom":subQ1}),1.0]])]});}
            var Q65;
            {var subQ0=sQuery(id+"F0.wireOp",EDGE,"E9.3.24.0");var subQ1=sQuery(id+"F0.wireOp",EDGE,"E0");var subQ2=makeQuery(id+"F0.imprint","INTERSECT",VERTEX,{"derivedFrom":[subQ1,subQ0]});Q65=makeQuery(id+"F0.imprint","IMPRINT",FACE,{"disambiguationData":[TD([[makeQuery(id+"F0.imprint","IMPRINT",EDGE,{"disambiguationData":[TD([[subQ2,-1.0]])],"derivedFrom":subQ1}),1.0]])]});}
            var Q66;
            {var subQ0=sQuery(id+"F0.wireOp",EDGE,"E8.3.23.0");var subQ1=sQuery(id+"F0.wireOp",EDGE,"E0");var subQ2=makeQuery(id+"F0.imprint","INTERSECT",VERTEX,{"derivedFrom":[subQ1,subQ0]});Q66=makeQuery(id+"F0.imprint","IMPRINT",FACE,{"disambiguationData":[TD([[makeQuery(id+"F0.imprint","IMPRINT",EDGE,{"disambiguationData":[TD([[subQ2,-1.0]])],"derivedFrom":subQ1}),1.0]])]});}
            var Q67;
            {var subQ0=sQuery(id+"F0.wireOp",EDGE,"E8.3.19.0");var subQ1=sQuery(id+"F0.wireOp",EDGE,"E0");var subQ2=makeQuery(id+"F0.imprint","INTERSECT",VERTEX,{"derivedFrom":[subQ1,subQ0]});Q67=makeQuery(id+"F0.imprint","IMPRINT",FACE,{"disambiguationData":[TD([[makeQuery(id+"F0.imprint","IMPRINT",EDGE,{"disambiguationData":[TD([[subQ2,-1.0]])],"derivedFrom":subQ1}),1.0]])]});}
            var Q68;
            {var subQ0=sQuery(id+"F0.wireOp",EDGE,"E9.5.29.0");var subQ1=sQuery(id+"F0.wireOp",EDGE,"E2.0");var subQ2=makeQuery(id+"F0.imprint","INTERSECT",VERTEX,{"derivedFrom":[subQ1,subQ0]});Q68=makeQuery(id+"F0.imprint","IMPRINT",FACE,{"disambiguationData":[TD([[makeQuery(id+"F0.imprint","IMPRINT",EDGE,{"disambiguationData":[TD([[subQ2,-1.0]])],"derivedFrom":subQ1}),-1.0]])]});}
            var Q69;
            {var subQ0=sQuery(id+"F0.wireOp",EDGE,"E7.5.7.0");var subQ1=sQuery(id+"F0.wireOp",EDGE,"E0");var subQ2=makeQuery(id+"F0.imprint","INTERSECT",VERTEX,{"derivedFrom":[subQ1,subQ0]});Q69=makeQuery(id+"F0.imprint","IMPRINT",FACE,{"disambiguationData":[TD([[makeQuery(id+"F0.imprint","IMPRINT",EDGE,{"disambiguationData":[TD([[subQ2,-1.0]])],"derivedFrom":subQ1}),1.0]])]});}
            var Q70;
            {var subQ0=sQuery(id+"F0.wireOp",EDGE,"E8.3.20.0");var subQ1=sQuery(id+"F0.wireOp",EDGE,"E0");var subQ2=makeQuery(id+"F0.imprint","INTERSECT",VERTEX,{"derivedFrom":[subQ1,subQ0]});Q70=makeQuery(id+"F0.imprint","IMPRINT",FACE,{"disambiguationData":[TD([[makeQuery(id+"F0.imprint","IMPRINT",EDGE,{"disambiguationData":[TD([[subQ2,-1.0]])],"derivedFrom":subQ1}),1.0]])]});}
            var Q71;
            {var subQ0=sQuery(id+"F0.wireOp",EDGE,"E7.3.8.0");var subQ1=sQuery(id+"F0.wireOp",EDGE,"E0");var subQ2=makeQuery(id+"F0.imprint","INTERSECT",VERTEX,{"derivedFrom":[subQ1,subQ0]});Q71=makeQuery(id+"F0.imprint","IMPRINT",FACE,{"disambiguationData":[TD([[makeQuery(id+"F0.imprint","IMPRINT",EDGE,{"disambiguationData":[TD([[subQ2,-1.0]])],"derivedFrom":subQ1}),1.0]])]});}
            var Q72;
            {var subQ0=sQuery(id+"F0.wireOp",EDGE,"E8.3.21.0");var subQ1=sQuery(id+"F0.wireOp",EDGE,"E0");var subQ2=makeQuery(id+"F0.imprint","INTERSECT",VERTEX,{"derivedFrom":[subQ1,subQ0]});Q72=makeQuery(id+"F0.imprint","IMPRINT",FACE,{"disambiguationData":[TD([[makeQuery(id+"F0.imprint","IMPRINT",EDGE,{"disambiguationData":[TD([[subQ2,-1.0]])],"derivedFrom":subQ1}),1.0]])]});}
            var Q73;
            {var subQ1=sQuery(id+"F0.wireOp",EDGE,"E1");var subQ8=sQuery(id+"F0.wireOp",EDGE,"E8.5.12.0");var subQ11=makeQuery(id+"F0.imprint","INTERSECT",VERTEX,{"derivedFrom":[subQ1,subQ8]});Q73=makeQuery(id+"F0.imprint","IMPRINT",FACE,{"disambiguationData":[TD([[makeQuery(id+"F0.imprint","IMPRINT",EDGE,{"disambiguationData":[TD([[subQ11,-1.0]])],"derivedFrom":subQ1}),1.0]])]});}
            var Q74;
            {var subQ0=sQuery(id+"F0.wireOp",EDGE,"E8.5.23.0");var subQ1=sQuery(id+"F0.wireOp",EDGE,"E0");var subQ2=makeQuery(id+"F0.imprint","INTERSECT",VERTEX,{"derivedFrom":[subQ1,subQ0]});Q74=makeQuery(id+"F0.imprint","IMPRINT",FACE,{"disambiguationData":[TD([[makeQuery(id+"F0.imprint","IMPRINT",EDGE,{"disambiguationData":[TD([[subQ2,1.0]])],"derivedFrom":subQ1}),1.0]])]});}
            var Q75;
            {var subQ0=sQuery(id+"F0.wireOp",EDGE,"E7.3.10.0");var subQ1=sQuery(id+"F0.wireOp",EDGE,"E0");var subQ2=makeQuery(id+"F0.imprint","INTERSECT",VERTEX,{"derivedFrom":[subQ1,subQ0]});Q75=makeQuery(id+"F0.imprint","IMPRINT",FACE,{"disambiguationData":[TD([[makeQuery(id+"F0.imprint","IMPRINT",EDGE,{"disambiguationData":[TD([[subQ2,-1.0]])],"derivedFrom":subQ1}),1.0]])]});}
            var Q76;
            {var subQ0=sQuery(id+"F0.wireOp",EDGE,"E7.5.11.0");var subQ1=sQuery(id+"F0.wireOp",EDGE,"E0");var subQ2=makeQuery(id+"F0.imprint","INTERSECT",VERTEX,{"derivedFrom":[subQ1,subQ0]});Q76=makeQuery(id+"F0.imprint","IMPRINT",FACE,{"disambiguationData":[TD([[makeQuery(id+"F0.imprint","IMPRINT",EDGE,{"disambiguationData":[TD([[subQ2,-1.0]])],"derivedFrom":subQ1}),1.0]])]});}
            var Q77;
            {var subQ0=sQuery(id+"F0.wireOp",EDGE,"E9.3.25.0");var subQ1=sQuery(id+"F0.wireOp",EDGE,"E0");var subQ2=makeQuery(id+"F0.imprint","INTERSECT",VERTEX,{"derivedFrom":[subQ1,subQ0]});Q77=makeQuery(id+"F0.imprint","IMPRINT",FACE,{"disambiguationData":[TD([[makeQuery(id+"F0.imprint","IMPRINT",EDGE,{"disambiguationData":[TD([[subQ2,-1.0]])],"derivedFrom":subQ1}),1.0]])]});}
            var Q78;
            {var subQ0=sQuery(id+"F0.wireOp",EDGE,"E7.3.11.0");var subQ1=sQuery(id+"F0.wireOp",EDGE,"E0");var subQ2=makeQuery(id+"F0.imprint","INTERSECT",VERTEX,{"derivedFrom":[subQ1,subQ0]});Q78=makeQuery(id+"F0.imprint","IMPRINT",FACE,{"disambiguationData":[TD([[makeQuery(id+"F0.imprint","IMPRINT",EDGE,{"disambiguationData":[TD([[subQ2,-1.0]])],"derivedFrom":subQ1}),1.0]])]});}
            var Q79;
            {var subQ0=sQuery(id+"F0.wireOp",EDGE,"E9.3.26.0");var subQ1=sQuery(id+"F0.wireOp",EDGE,"E0");var subQ2=makeQuery(id+"F0.imprint","INTERSECT",VERTEX,{"derivedFrom":[subQ1,subQ0]});Q79=makeQuery(id+"F0.imprint","IMPRINT",FACE,{"disambiguationData":[TD([[makeQuery(id+"F0.imprint","IMPRINT",EDGE,{"disambiguationData":[TD([[subQ2,-1.0]])],"derivedFrom":subQ1}),1.0]])]});}
            var Q80;
            {var subQ0=sQuery(id+"F0.wireOp",EDGE,"E9.3.27.0");var subQ1=sQuery(id+"F0.wireOp",EDGE,"E0");var subQ2=makeQuery(id+"F0.imprint","INTERSECT",VERTEX,{"derivedFrom":[subQ1,subQ0]});Q80=makeQuery(id+"F0.imprint","IMPRINT",FACE,{"disambiguationData":[TD([[makeQuery(id+"F0.imprint","IMPRINT",EDGE,{"disambiguationData":[TD([[subQ2,-1.0]])],"derivedFrom":subQ1}),1.0]])]});}
            var Q81;
            {var subQ0=sQuery(id+"F0.wireOp",EDGE,"E8.3.13.0");var subQ1=sQuery(id+"F0.wireOp",EDGE,"E0");var subQ2=makeQuery(id+"F0.imprint","INTERSECT",VERTEX,{"derivedFrom":[subQ1,subQ0]});Q81=makeQuery(id+"F0.imprint","IMPRINT",FACE,{"disambiguationData":[TD([[makeQuery(id+"F0.imprint","IMPRINT",EDGE,{"disambiguationData":[TD([[subQ2,-1.0]])],"derivedFrom":subQ1}),1.0]])]});}
            var Q82;
            {var subQ0=sQuery(id+"F0.wireOp",EDGE,"E9.5.24.0");var subQ1=sQuery(id+"F0.wireOp",EDGE,"E2.1");var subQ2=makeQuery(id+"F0.imprint","INTERSECT",VERTEX,{"derivedFrom":[subQ1,subQ0]});Q82=makeQuery(id+"F0.imprint","IMPRINT",FACE,{"disambiguationData":[TD([[makeQuery(id+"F0.imprint","IMPRINT",EDGE,{"disambiguationData":[TD([[subQ2,-1.0]])],"derivedFrom":subQ1}),-1.0]])]});}
            var Q83;
            {var subQ0=sQuery(id+"F0.wireOp",EDGE,"E9.5.26.0");var subQ1=sQuery(id+"F0.wireOp",EDGE,"E0");var subQ2=makeQuery(id+"F0.imprint","INTERSECT",VERTEX,{"derivedFrom":[subQ1,subQ0]});Q83=makeQuery(id+"F0.imprint","IMPRINT",FACE,{"disambiguationData":[TD([[makeQuery(id+"F0.imprint","IMPRINT",EDGE,{"disambiguationData":[TD([[subQ2,-1.0]])],"derivedFrom":subQ1}),1.0]])]});}
            var Q84;
            {var subQ0=sQuery(id+"F0.wireOp",EDGE,"E9.3.29.0");var subQ1=sQuery(id+"F0.wireOp",EDGE,"E0");var subQ2=makeQuery(id+"F0.imprint","INTERSECT",VERTEX,{"derivedFrom":[subQ1,subQ0]});Q84=makeQuery(id+"F0.imprint","IMPRINT",FACE,{"disambiguationData":[TD([[makeQuery(id+"F0.imprint","IMPRINT",EDGE,{"disambiguationData":[TD([[subQ2,-1.0]])],"derivedFrom":subQ1}),1.0]])]});}
            var Q85;
            {var subQ0=sQuery(id+"F0.wireOp",EDGE,"E8.3.15.0");var subQ1=sQuery(id+"F0.wireOp",EDGE,"E0");var subQ2=makeQuery(id+"F0.imprint","INTERSECT",VERTEX,{"derivedFrom":[subQ1,subQ0]});Q85=makeQuery(id+"F0.imprint","IMPRINT",FACE,{"disambiguationData":[TD([[makeQuery(id+"F0.imprint","IMPRINT",EDGE,{"disambiguationData":[TD([[subQ2,-1.0]])],"derivedFrom":subQ1}),1.0]])]});}
            var Q86;
            {var subQ0=sQuery(id+"F0.wireOp",EDGE,"E8.5.23.0");var subQ1=sQuery(id+"F0.wireOp",EDGE,"E2.1");var subQ2=makeQuery(id+"F0.imprint","INTERSECT",VERTEX,{"derivedFrom":[subQ1,subQ0]});Q86=makeQuery(id+"F0.imprint","IMPRINT",FACE,{"disambiguationData":[TD([[makeQuery(id+"F0.imprint","IMPRINT",EDGE,{"disambiguationData":[TD([[subQ2,-1.0]])],"derivedFrom":subQ1}),-1.0]])]});}
            var Q87;
            {var subQ3=sQuery(id+"F0.wireOp",EDGE,"E8.5.20.0");var subQ8=sQuery(id+"F0.wireOp",EDGE,"E0");var subQ9=makeQuery(id+"F0.imprint","INTERSECT",VERTEX,{"derivedFrom":[subQ8,subQ3]});Q87=makeQuery(id+"F0.imprint","IMPRINT",FACE,{"disambiguationData":[TD([[makeQuery(id+"F0.imprint","IMPRINT",EDGE,{"disambiguationData":[TD([[subQ9,-1.0]])],"derivedFrom":subQ8}),1.0]])]});}
            var Q88;
            {var subQ0=sQuery(id+"F0.wireOp",EDGE,"E5");var subQ1=sQuery(id+"F0.wireOp",EDGE,"E0");var subQ2=makeQuery(id+"F0.imprint","INTERSECT",VERTEX,{"derivedFrom":[subQ1,subQ0]});Q88=makeQuery(id+"F0.imprint","IMPRINT",FACE,{"disambiguationData":[TD([[makeQuery(id+"F0.imprint","IMPRINT",EDGE,{"disambiguationData":[TD([[subQ2,-1.0]])],"derivedFrom":subQ1}),1.0]])]});}
            var Q89;
            {var subQ0=sQuery(id+"F0.wireOp",EDGE,"E8.5.22.0");var subQ1=sQuery(id+"F0.wireOp",EDGE,"E2.1");var subQ2=makeQuery(id+"F0.imprint","INTERSECT",VERTEX,{"derivedFrom":[subQ1,subQ0]});Q89=makeQuery(id+"F0.imprint","IMPRINT",FACE,{"disambiguationData":[TD([[makeQuery(id+"F0.imprint","IMPRINT",EDGE,{"disambiguationData":[TD([[subQ2,-1.0]])],"derivedFrom":subQ1}),-1.0]])]});}
            var Q90;
            {var subQ0=sQuery(id+"F0.wireOp",EDGE,"E6.1.1");var subQ1=sQuery(id+"F0.wireOp",EDGE,"E0");var subQ2=makeQuery(id+"F0.imprint","INTERSECT",VERTEX,{"derivedFrom":[subQ1,subQ0]});Q90=makeQuery(id+"F0.imprint","IMPRINT",FACE,{"disambiguationData":[TD([[makeQuery(id+"F0.imprint","IMPRINT",EDGE,{"disambiguationData":[TD([[subQ2,-1.0]])],"derivedFrom":subQ1}),1.0]])]});}
            var Q91;
            {var subQ0=sQuery(id+"F0.wireOp",EDGE,"E8.3.17.0");var subQ1=sQuery(id+"F0.wireOp",EDGE,"E0");var subQ2=makeQuery(id+"F0.imprint","INTERSECT",VERTEX,{"derivedFrom":[subQ1,subQ0]});Q91=makeQuery(id+"F0.imprint","IMPRINT",FACE,{"disambiguationData":[TD([[makeQuery(id+"F0.imprint","IMPRINT",EDGE,{"disambiguationData":[TD([[subQ2,-1.0]])],"derivedFrom":subQ1}),1.0]])]});}
            var Q92;
            {var subQ0=sQuery(id+"F0.wireOp",EDGE,"E9.5.29.0");var subQ1=sQuery(id+"F0.wireOp",EDGE,"E0");var subQ2=makeQuery(id+"F0.imprint","INTERSECT",VERTEX,{"derivedFrom":[subQ1,subQ0]});Q92=makeQuery(id+"F0.imprint","IMPRINT",FACE,{"disambiguationData":[TD([[makeQuery(id+"F0.imprint","IMPRINT",EDGE,{"disambiguationData":[TD([[subQ2,-1.0]])],"derivedFrom":subQ1}),1.0]])]});}
            var Q93;
            {var subQ0=sQuery(id+"F0.wireOp",EDGE,"E6.2.1");var subQ1=sQuery(id+"F0.wireOp",EDGE,"E0");var subQ2=makeQuery(id+"F0.imprint","INTERSECT",VERTEX,{"derivedFrom":[subQ1,subQ0]});Q93=makeQuery(id+"F0.imprint","IMPRINT",FACE,{"disambiguationData":[TD([[makeQuery(id+"F0.imprint","IMPRINT",EDGE,{"disambiguationData":[TD([[subQ2,-1.0]])],"derivedFrom":subQ1}),1.0]])]});}
            var Q94;
            {var subQ0=sQuery(id+"F0.wireOp",EDGE,"E6.3.1");var subQ1=sQuery(id+"F0.wireOp",EDGE,"E0");var subQ2=makeQuery(id+"F0.imprint","INTERSECT",VERTEX,{"derivedFrom":[subQ1,subQ0]});Q94=makeQuery(id+"F0.imprint","IMPRINT",FACE,{"disambiguationData":[TD([[makeQuery(id+"F0.imprint","IMPRINT",EDGE,{"disambiguationData":[TD([[subQ2,-1.0]])],"derivedFrom":subQ1}),1.0]])]});}
            var Q95;
            {var subQ0=sQuery(id+"F0.wireOp",EDGE,"E9.5.25.0");var subQ1=sQuery(id+"F0.wireOp",EDGE,"E1");var subQ2=makeQuery(id+"F0.imprint","INTERSECT",VERTEX,{"derivedFrom":[subQ1,subQ0]});Q95=makeQuery(id+"F0.imprint","IMPRINT",FACE,{"disambiguationData":[TD([[makeQuery(id+"F0.imprint","IMPRINT",EDGE,{"disambiguationData":[TD([[subQ2,-1.0]])],"derivedFrom":subQ1}),1.0]])]});}
            var Q96;
            {var subQ0=sQuery(id+"F0.wireOp",EDGE,"E2.2");var subQ5=sQuery(id+"F0.wireOp",EDGE,"E8.3.19.0");var subQ6=makeQuery(id+"F0.imprint","INTERSECT",VERTEX,{"derivedFrom":[subQ0,subQ5]});Q96=makeQuery(id+"F0.imprint","IMPRINT",FACE,{"disambiguationData":[TD([[makeQuery(id+"F0.imprint","IMPRINT",EDGE,{"disambiguationData":[TD([[subQ6,-1.0]])],"derivedFrom":subQ5}),-1.0]])]});}
            var Q97;
            {var subQ0=sQuery(id+"F0.wireOp",EDGE,"E6.5.0");var subQ1=sQuery(id+"F0.wireOp",EDGE,"E6.3.1");var subQ2=makeQuery(id+"F0.imprint","INTERSECT",VERTEX,{"derivedFrom":[subQ1,subQ0]});Q97=makeQuery(id+"F0.imprint","IMPRINT",FACE,{"disambiguationData":[TD([[makeQuery(id+"F0.imprint","IMPRINT",EDGE,{"disambiguationData":[TD([[subQ2,-1.0]])],"derivedFrom":subQ1}),-1.0]])]});}
            var Q98;
            {var subQ1=sQuery(id+"F0.wireOp",EDGE,"E2.1");var subQ5=sQuery(id+"F0.wireOp",EDGE,"E8.3.22.0");var subQ6=makeQuery(id+"F0.imprint","INTERSECT",VERTEX,{"derivedFrom":[subQ1,subQ5]});Q98=makeQuery(id+"F0.imprint","IMPRINT",FACE,{"disambiguationData":[TD([[makeQuery(id+"F0.imprint","IMPRINT",EDGE,{"disambiguationData":[TD([[subQ6,-1.0]])],"derivedFrom":subQ1}),-1.0]])]});}
            var Q99;
            {var subQ1=sQuery(id+"F0.wireOp",EDGE,"E2.5");var subQ5=sQuery(id+"F0.wireOp",EDGE,"E6.3.1");var subQ6=makeQuery(id+"F0.imprint","INTERSECT",VERTEX,{"derivedFrom":[subQ1,subQ5]});Q99=makeQuery(id+"F0.imprint","IMPRINT",FACE,{"disambiguationData":[TD([[makeQuery(id+"F0.imprint","IMPRINT",EDGE,{"disambiguationData":[TD([[subQ6,-1.0]])],"derivedFrom":subQ1}),-1.0]])]});}
            var Q100;
            {var subQ3=sQuery(id+"F0.wireOp",EDGE,"E7.5.7.0");var subQ9=sQuery(id+"F0.wireOp",EDGE,"E1");var subQ11=makeQuery(id+"F0.imprint","INTERSECT",VERTEX,{"derivedFrom":[subQ9,subQ3]});Q100=makeQuery(id+"F0.imprint","IMPRINT",FACE,{"disambiguationData":[TD([[makeQuery(id+"F0.imprint","IMPRINT",EDGE,{"disambiguationData":[TD([[subQ11,-1.0]])],"derivedFrom":subQ9}),1.0]])]});}
            var Q101;
            {var subQ0=sQuery(id+"F0.wireOp",EDGE,"E9.5.24.0");var subQ1=sQuery(id+"F0.wireOp",EDGE,"E1");var subQ2=makeQuery(id+"F0.imprint","INTERSECT",VERTEX,{"derivedFrom":[subQ1,subQ0]});Q101=makeQuery(id+"F0.imprint","IMPRINT",FACE,{"disambiguationData":[TD([[makeQuery(id+"F0.imprint","IMPRINT",EDGE,{"disambiguationData":[TD([[subQ2,-1.0]])],"derivedFrom":subQ1}),-1.0]])]});}
            var Q102;
            {var subQ0=sQuery(id+"F0.wireOp",EDGE,"E7.3.8.0");var subQ1=sQuery(id+"F0.wireOp",EDGE,"E1");var subQ2=makeQuery(id+"F0.imprint","INTERSECT",VERTEX,{"derivedFrom":[subQ1,subQ0]});Q102=makeQuery(id+"F0.imprint","IMPRINT",FACE,{"disambiguationData":[TD([[makeQuery(id+"F0.imprint","IMPRINT",EDGE,{"disambiguationData":[TD([[subQ2,-1.0]])],"derivedFrom":subQ1}),1.0]])]});}
            var Q103;
            {var subQ0=sQuery(id+"F0.wireOp",EDGE,"E9.3.29.0");var subQ1=sQuery(id+"F0.wireOp",EDGE,"E2.0");var subQ2=makeQuery(id+"F0.imprint","INTERSECT",VERTEX,{"derivedFrom":[subQ1,subQ0]});Q103=makeQuery(id+"F0.imprint","IMPRINT",FACE,{"disambiguationData":[TD([[makeQuery(id+"F0.imprint","IMPRINT",EDGE,{"disambiguationData":[TD([[subQ2,-1.0]])],"derivedFrom":subQ1}),1.0]])]});}
            var Q104;
            {var subQ0=sQuery(id+"F0.wireOp",EDGE,"E2.5");var subQ5=sQuery(id+"F0.wireOp",EDGE,"E6.1.0");var subQ6=makeQuery(id+"F0.imprint","INTERSECT",VERTEX,{"derivedFrom":[subQ0,subQ5]});Q104=makeQuery(id+"F0.imprint","IMPRINT",FACE,{"disambiguationData":[TD([[makeQuery(id+"F0.imprint","IMPRINT",EDGE,{"disambiguationData":[TD([[subQ6,-1.0]])],"derivedFrom":subQ5}),1.0]])]});}
            var Q105;
            {var subQ0=sQuery(id+"F0.wireOp",EDGE,"E7.5.10.0");var subQ1=sQuery(id+"F0.wireOp",EDGE,"E7.3.8.0");var subQ2=makeQuery(id+"F0.imprint","INTERSECT",VERTEX,{"derivedFrom":[subQ1,subQ0]});Q105=makeQuery(id+"F0.imprint","IMPRINT",FACE,{"disambiguationData":[TD([[makeQuery(id+"F0.imprint","IMPRINT",EDGE,{"disambiguationData":[TD([[subQ2,-1.0]])],"derivedFrom":subQ1}),-1.0]])]});}
            var Q106;
            {var subQ0=sQuery(id+"F0.wireOp",EDGE,"E8.5.14.0");var subQ1=sQuery(id+"F0.wireOp",EDGE,"E7.3.11.0");var subQ2=makeQuery(id+"F0.imprint","INTERSECT",VERTEX,{"derivedFrom":[subQ1,subQ0]});Q106=makeQuery(id+"F0.imprint","IMPRINT",FACE,{"disambiguationData":[TD([[makeQuery(id+"F0.imprint","IMPRINT",EDGE,{"disambiguationData":[TD([[subQ2,-1.0]])],"derivedFrom":subQ1}),-1.0]])]});}
            var Q107;
            {var subQ0=sQuery(id+"F0.wireOp",EDGE,"E8.5.17.0");var subQ1=sQuery(id+"F0.wireOp",EDGE,"E8.3.14.0");var subQ2=makeQuery(id+"F0.imprint","INTERSECT",VERTEX,{"derivedFrom":[subQ1,subQ0]});Q107=makeQuery(id+"F0.imprint","IMPRINT",FACE,{"disambiguationData":[TD([[makeQuery(id+"F0.imprint","IMPRINT",EDGE,{"disambiguationData":[TD([[subQ2,-1.0]])],"derivedFrom":subQ1}),-1.0]])]});}
            var Q108;
            {var subQ1=sQuery(id+"F0.wireOp",EDGE,"E2.4");var subQ5=sQuery(id+"F0.wireOp",EDGE,"E7.3.7.0");var subQ6=makeQuery(id+"F0.imprint","INTERSECT",VERTEX,{"derivedFrom":[subQ1,subQ5]});Q108=makeQuery(id+"F0.imprint","IMPRINT",FACE,{"disambiguationData":[TD([[makeQuery(id+"F0.imprint","IMPRINT",EDGE,{"disambiguationData":[TD([[subQ6,-1.0]])],"derivedFrom":subQ1}),-1.0]])]});}
            var Q109;
            {var subQ0=sQuery(id+"F0.wireOp",EDGE,"E6.2.0");var subQ1=sQuery(id+"F0.wireOp",EDGE,"E1");var subQ2=makeQuery(id+"F0.imprint","INTERSECT",VERTEX,{"derivedFrom":[subQ1,subQ0]});Q109=makeQuery(id+"F0.imprint","IMPRINT",FACE,{"disambiguationData":[TD([[makeQuery(id+"F0.imprint","IMPRINT",EDGE,{"disambiguationData":[TD([[subQ2,-1.0]])],"derivedFrom":subQ1}),1.0]])]});}
            var Q110;
            {var subQ0=sQuery(id+"F0.wireOp",EDGE,"E4");var subQ1=sQuery(id+"F0.wireOp",EDGE,"E2.0");var subQ2=makeQuery(id+"F0.imprint","INTERSECT",VERTEX,{"derivedFrom":[subQ1,subQ0]});Q110=makeQuery(id+"F0.imprint","IMPRINT",FACE,{"disambiguationData":[TD([[makeQuery(id+"F0.imprint","IMPRINT",EDGE,{"disambiguationData":[TD([[subQ2,-1.0]])],"derivedFrom":subQ1}),-1.0]])]});}
            var Q111;
            {var subQ0=sQuery(id+"F0.wireOp",EDGE,"E8.5.18.0");var subQ1=sQuery(id+"F0.wireOp",EDGE,"E2.2");var subQ2=makeQuery(id+"F0.imprint","INTERSECT",VERTEX,{"derivedFrom":[subQ1,subQ0]});Q111=makeQuery(id+"F0.imprint","IMPRINT",FACE,{"disambiguationData":[TD([[makeQuery(id+"F0.imprint","IMPRINT",EDGE,{"disambiguationData":[TD([[subQ2,-1.0]])],"derivedFrom":subQ1}),-1.0]])]});}
            var Q112;
            {var subQ0=sQuery(id+"F0.wireOp",EDGE,"E7.5.8.0");var subQ1=sQuery(id+"F0.wireOp",EDGE,"E2.4");var subQ2=makeQuery(id+"F0.imprint","INTERSECT",VERTEX,{"derivedFrom":[subQ1,subQ0]});Q112=makeQuery(id+"F0.imprint","IMPRINT",FACE,{"disambiguationData":[TD([[makeQuery(id+"F0.imprint","IMPRINT",EDGE,{"disambiguationData":[TD([[subQ2,-1.0]])],"derivedFrom":subQ1}),-1.0]])]});}
            var Q113;
            {var subQ0=sQuery(id+"F0.wireOp",EDGE,"E8.3.23.0");var subQ1=sQuery(id+"F0.wireOp",EDGE,"E1");var subQ2=makeQuery(id+"F0.imprint","INTERSECT",VERTEX,{"derivedFrom":[subQ1,subQ0]});Q113=makeQuery(id+"F0.imprint","IMPRINT",FACE,{"disambiguationData":[TD([[makeQuery(id+"F0.imprint","IMPRINT",EDGE,{"disambiguationData":[TD([[subQ2,-1.0]])],"derivedFrom":subQ1}),1.0]])]});}
            var Q114;
            {var subQ0=sQuery(id+"F0.wireOp",EDGE,"E2.1");var subQ5=sQuery(id+"F0.wireOp",EDGE,"E9.3.24.0");var subQ7=makeQuery(id+"F0.imprint","INTERSECT",VERTEX,{"derivedFrom":[subQ0,subQ5]});Q114=makeQuery(id+"F0.imprint","IMPRINT",FACE,{"disambiguationData":[TD([[makeQuery(id+"F0.imprint","IMPRINT",EDGE,{"disambiguationData":[TD([[subQ7,-1.0]])],"derivedFrom":subQ5}),-1.0]])]});}
            var Q115;
            {var subQ1=sQuery(id+"F0.wireOp",EDGE,"E2.1");var subQ5=sQuery(id+"F0.wireOp",EDGE,"E8.3.23.0");var subQ6=makeQuery(id+"F0.imprint","INTERSECT",VERTEX,{"derivedFrom":[subQ1,subQ5]});Q115=makeQuery(id+"F0.imprint","IMPRINT",FACE,{"disambiguationData":[TD([[makeQuery(id+"F0.imprint","IMPRINT",EDGE,{"disambiguationData":[TD([[subQ6,-1.0]])],"derivedFrom":subQ1}),-1.0]])]});}
            var Q116;
            {var subQ1=sQuery(id+"F0.wireOp",EDGE,"E2.4");var subQ5=sQuery(id+"F0.wireOp",EDGE,"E7.3.6.0");var subQ6=makeQuery(id+"F0.imprint","INTERSECT",VERTEX,{"derivedFrom":[subQ1,subQ5]});Q116=makeQuery(id+"F0.imprint","IMPRINT",FACE,{"disambiguationData":[TD([[makeQuery(id+"F0.imprint","IMPRINT",EDGE,{"disambiguationData":[TD([[subQ6,-1.0]])],"derivedFrom":subQ1}),-1.0]])]});}
            var Q117;
            {var subQ0=sQuery(id+"F0.wireOp",EDGE,"E6.3.0");var subQ1=sQuery(id+"F0.wireOp",EDGE,"E1");var subQ2=makeQuery(id+"F0.imprint","INTERSECT",VERTEX,{"derivedFrom":[subQ1,subQ0]});Q117=makeQuery(id+"F0.imprint","IMPRINT",FACE,{"disambiguationData":[TD([[makeQuery(id+"F0.imprint","IMPRINT",EDGE,{"disambiguationData":[TD([[subQ2,-1.0]])],"derivedFrom":subQ1}),1.0]])]});}
            var Q118;
            {var subQ0=sQuery(id+"F0.wireOp",EDGE,"E7.3.11.0");var subQ1=sQuery(id+"F0.wireOp",EDGE,"E1");var subQ2=makeQuery(id+"F0.imprint","INTERSECT",VERTEX,{"derivedFrom":[subQ1,subQ0]});Q118=makeQuery(id+"F0.imprint","IMPRINT",FACE,{"disambiguationData":[TD([[makeQuery(id+"F0.imprint","IMPRINT",EDGE,{"disambiguationData":[TD([[subQ2,-1.0]])],"derivedFrom":subQ1}),1.0]])]});}
            var Q119;
            {var subQ0=sQuery(id+"F0.wireOp",EDGE,"E8.5.17.0");var subQ1=sQuery(id+"F0.wireOp",EDGE,"E2.2");var subQ2=makeQuery(id+"F0.imprint","INTERSECT",VERTEX,{"derivedFrom":[subQ1,subQ0]});Q119=makeQuery(id+"F0.imprint","IMPRINT",FACE,{"disambiguationData":[TD([[makeQuery(id+"F0.imprint","IMPRINT",EDGE,{"disambiguationData":[TD([[subQ2,-1.0]])],"derivedFrom":subQ1}),-1.0]])]});}
            var Q120;
            {var subQ0=sQuery(id+"F0.wireOp",EDGE,"E8.5.15.0");var subQ5=sQuery(id+"F0.wireOp",EDGE,"E8.3.14.0");var subQ6=makeQuery(id+"F0.imprint","INTERSECT",VERTEX,{"derivedFrom":[subQ5,subQ0]});Q120=makeQuery(id+"F0.imprint","IMPRINT",FACE,{"disambiguationData":[TD([[makeQuery(id+"F0.imprint","IMPRINT",EDGE,{"disambiguationData":[TD([[subQ6,-1.0]])],"derivedFrom":subQ5}),-1.0]])]});}
            var Q121;
            {var subQ0=sQuery(id+"F0.wireOp",EDGE,"E6.3.0");var subQ1=sQuery(id+"F0.wireOp",EDGE,"E5");var subQ2=makeQuery(id+"F0.imprint","INTERSECT",VERTEX,{"derivedFrom":[subQ1,subQ0]});Q121=makeQuery(id+"F0.imprint","IMPRINT",FACE,{"disambiguationData":[TD([[makeQuery(id+"F0.imprint","IMPRINT",EDGE,{"disambiguationData":[TD([[subQ2,-1.0]])],"derivedFrom":subQ1}),-1.0]])]});}
            var Q122;
            {var subQ1=sQuery(id+"F0.wireOp",EDGE,"E2.1");var subQ7=sQuery(id+"F0.wireOp",EDGE,"E8.3.21.0");var subQ8=makeQuery(id+"F0.imprint","INTERSECT",VERTEX,{"derivedFrom":[subQ1,subQ7]});Q122=makeQuery(id+"F0.imprint","IMPRINT",FACE,{"disambiguationData":[TD([[makeQuery(id+"F0.imprint","IMPRINT",EDGE,{"disambiguationData":[TD([[subQ8,-1.0]])],"derivedFrom":subQ1}),-1.0]])]});}
            var Q123;
            {var subQ0=sQuery(id+"F0.wireOp",EDGE,"E6.2.1");var subQ1=sQuery(id+"F0.wireOp",EDGE,"E2.5");var subQ2=makeQuery(id+"F0.imprint","INTERSECT",VERTEX,{"derivedFrom":[subQ1,subQ0]});Q123=makeQuery(id+"F0.imprint","IMPRINT",FACE,{"disambiguationData":[TD([[makeQuery(id+"F0.imprint","IMPRINT",EDGE,{"disambiguationData":[TD([[subQ2,-1.0]])],"derivedFrom":subQ1}),-1.0]])]});}
            var Q124;
            {var subQ3=sQuery(id+"F0.wireOp",EDGE,"E7.5.8.0");var subQ6=sQuery(id+"F0.wireOp",EDGE,"E1");var subQ11=makeQuery(id+"F0.imprint","INTERSECT",VERTEX,{"derivedFrom":[subQ6,subQ3]});Q124=makeQuery(id+"F0.imprint","IMPRINT",FACE,{"disambiguationData":[TD([[makeQuery(id+"F0.imprint","IMPRINT",EDGE,{"disambiguationData":[TD([[subQ11,-1.0]])],"derivedFrom":subQ6}),1.0]])]});}
            var Q125;
            {var subQ0=sQuery(id+"F0.wireOp",EDGE,"E8.3.12.0");var subQ1=sQuery(id+"F0.wireOp",EDGE,"E1");var subQ2=makeQuery(id+"F0.imprint","INTERSECT",VERTEX,{"derivedFrom":[subQ1,subQ0]});Q125=makeQuery(id+"F0.imprint","IMPRINT",FACE,{"disambiguationData":[TD([[makeQuery(id+"F0.imprint","IMPRINT",EDGE,{"disambiguationData":[TD([[subQ2,-1.0]])],"derivedFrom":subQ1}),1.0]])]});}
            var Q126;
            {var subQ0=sQuery(id+"F0.wireOp",EDGE,"E9.3.27.0");var subQ1=sQuery(id+"F0.wireOp",EDGE,"E2.0");var subQ2=makeQuery(id+"F0.imprint","INTERSECT",VERTEX,{"derivedFrom":[subQ1,subQ0]});Q126=makeQuery(id+"F0.imprint","IMPRINT",FACE,{"disambiguationData":[TD([[makeQuery(id+"F0.imprint","IMPRINT",EDGE,{"disambiguationData":[TD([[subQ2,-1.0]])],"derivedFrom":subQ1}),1.0]])]});}
            var Q127;
            {var subQ0=sQuery(id+"F0.wireOp",EDGE,"E8.3.14.0");var subQ1=sQuery(id+"F0.wireOp",EDGE,"E2.3");var subQ2=makeQuery(id+"F0.imprint","INTERSECT",VERTEX,{"derivedFrom":[subQ1,subQ0]});Q127=makeQuery(id+"F0.imprint","IMPRINT",FACE,{"disambiguationData":[TD([[makeQuery(id+"F0.imprint","IMPRINT",EDGE,{"disambiguationData":[TD([[subQ2,-1.0]])],"derivedFrom":subQ1}),-1.0]])]});}
            var Q128;
            {var subQ0=sQuery(id+"F0.wireOp",EDGE,"E8.3.20.0");var subQ1=sQuery(id+"F0.wireOp",EDGE,"E2.1");var subQ2=makeQuery(id+"F0.imprint","INTERSECT",VERTEX,{"derivedFrom":[subQ1,subQ0]});Q128=makeQuery(id+"F0.imprint","IMPRINT",FACE,{"disambiguationData":[TD([[makeQuery(id+"F0.imprint","IMPRINT",EDGE,{"disambiguationData":[TD([[subQ2,-1.0]])],"derivedFrom":subQ1}),-1.0]])]});}
            var Q129;
            {var subQ1=sQuery(id+"F0.wireOp",EDGE,"E2.5");var subQ7=sQuery(id+"F0.wireOp",EDGE,"E6.1.1");var subQ8=makeQuery(id+"F0.imprint","INTERSECT",VERTEX,{"derivedFrom":[subQ1,subQ7]});Q129=makeQuery(id+"F0.imprint","IMPRINT",FACE,{"disambiguationData":[TD([[makeQuery(id+"F0.imprint","IMPRINT",EDGE,{"disambiguationData":[TD([[subQ8,-1.0]])],"derivedFrom":subQ1}),-1.0]])]});}
            var Q130;
            {var subQ1=sQuery(id+"F0.wireOp",EDGE,"E1");var subQ8=sQuery(id+"F0.wireOp",EDGE,"E7.5.11.0");var subQ11=makeQuery(id+"F0.imprint","INTERSECT",VERTEX,{"derivedFrom":[subQ1,subQ8]});Q130=makeQuery(id+"F0.imprint","IMPRINT",FACE,{"disambiguationData":[TD([[makeQuery(id+"F0.imprint","IMPRINT",EDGE,{"disambiguationData":[TD([[subQ11,-1.0]])],"derivedFrom":subQ1}),1.0]])]});}
            var Q131;
            {var subQ0=sQuery(id+"F0.wireOp",EDGE,"E9.5.28.0");var subQ1=sQuery(id+"F0.wireOp",EDGE,"E2.0");var subQ2=makeQuery(id+"F0.imprint","INTERSECT",VERTEX,{"derivedFrom":[subQ1,subQ0]});Q131=makeQuery(id+"F0.imprint","IMPRINT",FACE,{"disambiguationData":[TD([[makeQuery(id+"F0.imprint","IMPRINT",EDGE,{"disambiguationData":[TD([[subQ2,-1.0]])],"derivedFrom":subQ1}),-1.0]])]});}
            var Q132;
            {var subQ1=sQuery(id+"F0.wireOp",EDGE,"E2.3");var subQ3=sQuery(id+"F0.wireOp",EDGE,"E8.3.14.0");var subQ4=makeQuery(id+"F0.imprint","INTERSECT",VERTEX,{"derivedFrom":[subQ1,subQ3]});Q132=makeQuery(id+"F0.imprint","IMPRINT",FACE,{"disambiguationData":[TD([[makeQuery(id+"F0.imprint","IMPRINT",EDGE,{"disambiguationData":[TD([[subQ4,-1.0]])],"derivedFrom":subQ3}),-1.0]])]});}
            var Q133;
            {var subQ0=sQuery(id+"F0.wireOp",EDGE,"E7.3.9.0");var subQ1=sQuery(id+"F0.wireOp",EDGE,"E2.4");var subQ2=makeQuery(id+"F0.imprint","INTERSECT",VERTEX,{"derivedFrom":[subQ1,subQ0]});Q133=makeQuery(id+"F0.imprint","IMPRINT",FACE,{"disambiguationData":[TD([[makeQuery(id+"F0.imprint","IMPRINT",EDGE,{"disambiguationData":[TD([[subQ2,-1.0]])],"derivedFrom":subQ1}),-1.0]])]});}
            var Q134;
            {var subQ0=sQuery(id+"F0.wireOp",EDGE,"E8.5.18.0");var subQ1=sQuery(id+"F0.wireOp",EDGE,"E8.3.15.0");var subQ2=makeQuery(id+"F0.imprint","INTERSECT",VERTEX,{"derivedFrom":[subQ1,subQ0]});Q134=makeQuery(id+"F0.imprint","IMPRINT",FACE,{"disambiguationData":[TD([[makeQuery(id+"F0.imprint","IMPRINT",EDGE,{"disambiguationData":[TD([[subQ2,-1.0]])],"derivedFrom":subQ1}),-1.0]])]});}
            var Q135;
            {var subQ1=sQuery(id+"F0.wireOp",EDGE,"E5");var subQ6=sQuery(id+"F0.wireOp",EDGE,"E2.5");var subQ9=makeQuery(id+"F0.imprint","INTERSECT",VERTEX,{"derivedFrom":[subQ6,subQ1]});Q135=makeQuery(id+"F0.imprint","IMPRINT",FACE,{"disambiguationData":[TD([[makeQuery(id+"F0.imprint","IMPRINT",EDGE,{"disambiguationData":[TD([[subQ9,-1.0]])],"derivedFrom":subQ6}),-1.0]])]});}
            var Q136;
            {var subQ0=sQuery(id+"F0.wireOp",EDGE,"E9.3.26.0");var subQ1=sQuery(id+"F0.wireOp",EDGE,"E2.0");var subQ2=makeQuery(id+"F0.imprint","INTERSECT",VERTEX,{"derivedFrom":[subQ1,subQ0]});Q136=makeQuery(id+"F0.imprint","IMPRINT",FACE,{"disambiguationData":[TD([[makeQuery(id+"F0.imprint","IMPRINT",EDGE,{"disambiguationData":[TD([[subQ2,-1.0]])],"derivedFrom":subQ1}),1.0]])]});}
            var Q137;
            {var subQ0=sQuery(id+"F0.wireOp",EDGE,"E6.4.0");var subQ1=sQuery(id+"F0.wireOp",EDGE,"E2.5");var subQ2=makeQuery(id+"F0.imprint","INTERSECT",VERTEX,{"derivedFrom":[subQ1,subQ0]});Q137=makeQuery(id+"F0.imprint","IMPRINT",FACE,{"disambiguationData":[TD([[makeQuery(id+"F0.imprint","IMPRINT",EDGE,{"disambiguationData":[TD([[subQ2,-1.0]])],"derivedFrom":subQ1}),-1.0]])]});}
            var Q138;
            {var subQ0=sQuery(id+"F0.wireOp",EDGE,"E7.5.7.0");var subQ1=sQuery(id+"F0.wireOp",EDGE,"E2.4");var subQ2=makeQuery(id+"F0.imprint","INTERSECT",VERTEX,{"derivedFrom":[subQ1,subQ0]});Q138=makeQuery(id+"F0.imprint","IMPRINT",FACE,{"disambiguationData":[TD([[makeQuery(id+"F0.imprint","IMPRINT",EDGE,{"disambiguationData":[TD([[subQ2,-1.0]])],"derivedFrom":subQ1}),-1.0]])]});}
            var Q139;
            {var subQ0=sQuery(id+"F0.wireOp",EDGE,"E6.4.0");var subQ1=sQuery(id+"F0.wireOp",EDGE,"E1");var subQ2=makeQuery(id+"F0.imprint","INTERSECT",VERTEX,{"derivedFrom":[subQ1,subQ0]});Q139=makeQuery(id+"F0.imprint","IMPRINT",FACE,{"disambiguationData":[TD([[makeQuery(id+"F0.imprint","IMPRINT",EDGE,{"disambiguationData":[TD([[subQ2,-1.0]])],"derivedFrom":subQ1}),1.0]])]});}
            var Q140;
            {var subQ0=sQuery(id+"F0.wireOp",EDGE,"E8.3.18.0");var subQ1=sQuery(id+"F0.wireOp",EDGE,"E2.2");var subQ2=makeQuery(id+"F0.imprint","INTERSECT",VERTEX,{"derivedFrom":[subQ1,subQ0]});Q140=makeQuery(id+"F0.imprint","IMPRINT",FACE,{"disambiguationData":[TD([[makeQuery(id+"F0.imprint","IMPRINT",EDGE,{"disambiguationData":[TD([[subQ2,-1.0]])],"derivedFrom":subQ1}),-1.0]])]});}
            var Q141;
            {var subQ1=sQuery(id+"F0.wireOp",EDGE,"E1");var subQ8=sQuery(id+"F0.wireOp",EDGE,"E8.5.13.0");var subQ11=makeQuery(id+"F0.imprint","INTERSECT",VERTEX,{"derivedFrom":[subQ1,subQ8]});Q141=makeQuery(id+"F0.imprint","IMPRINT",FACE,{"disambiguationData":[TD([[makeQuery(id+"F0.imprint","IMPRINT",EDGE,{"disambiguationData":[TD([[subQ11,-1.0]])],"derivedFrom":subQ1}),1.0]])]});}
            var Q142;
            {var subQ0=sQuery(id+"F0.wireOp",EDGE,"E8.3.15.0");var subQ1=sQuery(id+"F0.wireOp",EDGE,"E1");var subQ2=makeQuery(id+"F0.imprint","INTERSECT",VERTEX,{"derivedFrom":[subQ1,subQ0]});Q142=makeQuery(id+"F0.imprint","IMPRINT",FACE,{"disambiguationData":[TD([[makeQuery(id+"F0.imprint","IMPRINT",EDGE,{"disambiguationData":[TD([[subQ2,-1.0]])],"derivedFrom":subQ1}),1.0]])]});}
            var Q143;
            {var subQ0=sQuery(id+"F0.wireOp",EDGE,"E9.5.27.0");var subQ1=sQuery(id+"F0.wireOp",EDGE,"E2.0");var subQ2=makeQuery(id+"F0.imprint","INTERSECT",VERTEX,{"derivedFrom":[subQ1,subQ0]});Q143=makeQuery(id+"F0.imprint","IMPRINT",FACE,{"disambiguationData":[TD([[makeQuery(id+"F0.imprint","IMPRINT",EDGE,{"disambiguationData":[TD([[subQ2,-1.0]])],"derivedFrom":subQ1}),-1.0]])]});}
            var Q144;
            {var subQ0=sQuery(id+"F0.wireOp",EDGE,"E8.5.14.0");var subQ1=sQuery(id+"F0.wireOp",EDGE,"E2.3");var subQ2=makeQuery(id+"F0.imprint","INTERSECT",VERTEX,{"derivedFrom":[subQ1,subQ0]});Q144=makeQuery(id+"F0.imprint","IMPRINT",FACE,{"disambiguationData":[TD([[makeQuery(id+"F0.imprint","IMPRINT",EDGE,{"disambiguationData":[TD([[subQ2,-1.0]])],"derivedFrom":subQ1}),-1.0]])]});}
            var Q145;
            {var subQ0=sQuery(id+"F0.wireOp",EDGE,"E6.4.1");var subQ1=sQuery(id+"F0.wireOp",EDGE,"E2.5");var subQ2=makeQuery(id+"F0.imprint","INTERSECT",VERTEX,{"derivedFrom":[subQ1,subQ0]});Q145=makeQuery(id+"F0.imprint","IMPRINT",FACE,{"disambiguationData":[TD([[makeQuery(id+"F0.imprint","IMPRINT",EDGE,{"disambiguationData":[TD([[subQ2,-1.0]])],"derivedFrom":subQ1}),-1.0]])]});}
            var Q146;
            {var subQ0=sQuery(id+"F0.wireOp",EDGE,"E7.5.6.0");var subQ1=sQuery(id+"F0.wireOp",EDGE,"E1");var subQ2=makeQuery(id+"F0.imprint","INTERSECT",VERTEX,{"derivedFrom":[subQ1,subQ0]});Q146=makeQuery(id+"F0.imprint","IMPRINT",FACE,{"disambiguationData":[TD([[makeQuery(id+"F0.imprint","IMPRINT",EDGE,{"disambiguationData":[TD([[subQ2,-1.0]])],"derivedFrom":subQ1}),1.0]])]});}
            var Q147;
            {var subQ1=sQuery(id+"F0.wireOp",EDGE,"E2.2");var subQ5=sQuery(id+"F0.wireOp",EDGE,"E8.3.17.0");var subQ6=makeQuery(id+"F0.imprint","INTERSECT",VERTEX,{"derivedFrom":[subQ1,subQ5]});Q147=makeQuery(id+"F0.imprint","IMPRINT",FACE,{"disambiguationData":[TD([[makeQuery(id+"F0.imprint","IMPRINT",EDGE,{"disambiguationData":[TD([[subQ6,-1.0]])],"derivedFrom":subQ1}),-1.0]])]});}
            var Q148;
            {var subQ3=sQuery(id+"F0.wireOp",EDGE,"E8.5.16.0");var subQ7=sQuery(id+"F0.wireOp",EDGE,"E1");var subQ8=makeQuery(id+"F0.imprint","INTERSECT",VERTEX,{"derivedFrom":[subQ7,subQ3]});Q148=makeQuery(id+"F0.imprint","IMPRINT",FACE,{"disambiguationData":[TD([[makeQuery(id+"F0.imprint","IMPRINT",EDGE,{"disambiguationData":[TD([[subQ8,-1.0]])],"derivedFrom":subQ7}),1.0]])]});}
            var Q149;
            {var subQ0=sQuery(id+"F0.wireOp",EDGE,"E9.3.25.0");var subQ1=sQuery(id+"F0.wireOp",EDGE,"E2.0");var subQ2=makeQuery(id+"F0.imprint","INTERSECT",VERTEX,{"derivedFrom":[subQ1,subQ0]});Q149=makeQuery(id+"F0.imprint","IMPRINT",FACE,{"disambiguationData":[TD([[makeQuery(id+"F0.imprint","IMPRINT",EDGE,{"disambiguationData":[TD([[subQ2,-1.0]])],"derivedFrom":subQ1}),1.0]])]});}
            var Q150;
            {var subQ0=sQuery(id+"F0.wireOp",EDGE,"E8.3.12.0");var subQ1=sQuery(id+"F0.wireOp",EDGE,"E2.3");var subQ2=makeQuery(id+"F0.imprint","INTERSECT",VERTEX,{"derivedFrom":[subQ1,subQ0]});Q150=makeQuery(id+"F0.imprint","IMPRINT",FACE,{"disambiguationData":[TD([[makeQuery(id+"F0.imprint","IMPRINT",EDGE,{"disambiguationData":[TD([[subQ2,-1.0]])],"derivedFrom":subQ1}),1.0]])]});}
            var Q151;
            {var subQ0=sQuery(id+"F0.wireOp",EDGE,"E6.3.0");var subQ1=sQuery(id+"F0.wireOp",EDGE,"E2.5");var subQ2=makeQuery(id+"F0.imprint","INTERSECT",VERTEX,{"derivedFrom":[subQ1,subQ0]});Q151=makeQuery(id+"F0.imprint","IMPRINT",FACE,{"disambiguationData":[TD([[makeQuery(id+"F0.imprint","IMPRINT",EDGE,{"disambiguationData":[TD([[subQ2,-1.0]])],"derivedFrom":subQ1}),-1.0]])]});}
            var Q152;
            {var subQ1=sQuery(id+"F0.wireOp",EDGE,"E1");var subQ7=sQuery(id+"F0.wireOp",EDGE,"E7.5.9.0");var subQ9=makeQuery(id+"F0.imprint","INTERSECT",VERTEX,{"derivedFrom":[subQ1,subQ7]});Q152=makeQuery(id+"F0.imprint","IMPRINT",FACE,{"disambiguationData":[TD([[makeQuery(id+"F0.imprint","IMPRINT",EDGE,{"disambiguationData":[TD([[subQ9,-1.0]])],"derivedFrom":subQ1}),1.0]])]});}
            var Q153;
            {var subQ0=sQuery(id+"F0.wireOp",EDGE,"E8.3.16.0");var subQ1=sQuery(id+"F0.wireOp",EDGE,"E2.2");var subQ2=makeQuery(id+"F0.imprint","INTERSECT",VERTEX,{"derivedFrom":[subQ1,subQ0]});Q153=makeQuery(id+"F0.imprint","IMPRINT",FACE,{"disambiguationData":[TD([[makeQuery(id+"F0.imprint","IMPRINT",EDGE,{"disambiguationData":[TD([[subQ2,-1.0]])],"derivedFrom":subQ1}),-1.0]])]});}
            var Q154;
            {var subQ1=sQuery(id+"F0.wireOp",EDGE,"E1");var subQ8=sQuery(id+"F0.wireOp",EDGE,"E8.5.17.0");var subQ11=makeQuery(id+"F0.imprint","INTERSECT",VERTEX,{"derivedFrom":[subQ1,subQ8]});Q154=makeQuery(id+"F0.imprint","IMPRINT",FACE,{"disambiguationData":[TD([[makeQuery(id+"F0.imprint","IMPRINT",EDGE,{"disambiguationData":[TD([[subQ11,-1.0]])],"derivedFrom":subQ1}),1.0]])]});}
            var Q155;
            {var subQ0=sQuery(id+"F0.wireOp",EDGE,"E6.1.1");var subQ1=sQuery(id+"F0.wireOp",EDGE,"E1");var subQ2=makeQuery(id+"F0.imprint","INTERSECT",VERTEX,{"derivedFrom":[subQ1,subQ0]});Q155=makeQuery(id+"F0.imprint","IMPRINT",FACE,{"disambiguationData":[TD([[makeQuery(id+"F0.imprint","IMPRINT",EDGE,{"disambiguationData":[TD([[subQ2,-1.0]])],"derivedFrom":subQ1}),1.0]])]});}
            var Q156;
            {var subQ0=sQuery(id+"F0.wireOp",EDGE,"E9.5.25.0");var subQ1=sQuery(id+"F0.wireOp",EDGE,"E2.1");var subQ2=makeQuery(id+"F0.imprint","INTERSECT",VERTEX,{"derivedFrom":[subQ1,subQ0]});Q156=makeQuery(id+"F0.imprint","IMPRINT",FACE,{"disambiguationData":[TD([[makeQuery(id+"F0.imprint","IMPRINT",EDGE,{"disambiguationData":[TD([[subQ2,-1.0]])],"derivedFrom":subQ1}),-1.0]])]});}
            var Q157;
            {var subQ0=sQuery(id+"F0.wireOp",EDGE,"E8.5.13.0");var subQ1=sQuery(id+"F0.wireOp",EDGE,"E2.3");var subQ2=makeQuery(id+"F0.imprint","INTERSECT",VERTEX,{"derivedFrom":[subQ1,subQ0]});Q157=makeQuery(id+"F0.imprint","IMPRINT",FACE,{"disambiguationData":[TD([[makeQuery(id+"F0.imprint","IMPRINT",EDGE,{"disambiguationData":[TD([[subQ2,-1.0]])],"derivedFrom":subQ1}),-1.0]])]});}
            var Q158;
            {var subQ1=sQuery(id+"F0.wireOp",EDGE,"E1");var subQ3=sQuery(id+"F0.wireOp",EDGE,"E7.3.10.0");var subQ4=makeQuery(id+"F0.imprint","INTERSECT",VERTEX,{"derivedFrom":[subQ1,subQ3]});Q158=makeQuery(id+"F0.imprint","IMPRINT",FACE,{"disambiguationData":[TD([[makeQuery(id+"F0.imprint","IMPRINT",EDGE,{"disambiguationData":[TD([[subQ4,-1.0]])],"derivedFrom":subQ3}),1.0]])]});}
            var Q159;
            {var subQ3=sQuery(id+"F0.wireOp",EDGE,"E8.5.14.0");var subQ7=sQuery(id+"F0.wireOp",EDGE,"E1");var subQ9=makeQuery(id+"F0.imprint","INTERSECT",VERTEX,{"derivedFrom":[subQ7,subQ3]});Q159=makeQuery(id+"F0.imprint","IMPRINT",FACE,{"disambiguationData":[TD([[makeQuery(id+"F0.imprint","IMPRINT",EDGE,{"disambiguationData":[TD([[subQ9,-1.0]])],"derivedFrom":subQ7}),1.0]])]});}
            var Q160;
            {var subQ0=sQuery(id+"F0.wireOp",EDGE,"E8.3.15.0");var subQ1=sQuery(id+"F0.wireOp",EDGE,"E2.2");var subQ2=makeQuery(id+"F0.imprint","INTERSECT",VERTEX,{"derivedFrom":[subQ1,subQ0]});Q160=makeQuery(id+"F0.imprint","IMPRINT",FACE,{"disambiguationData":[TD([[makeQuery(id+"F0.imprint","IMPRINT",EDGE,{"disambiguationData":[TD([[subQ2,-1.0]])],"derivedFrom":subQ1}),-1.0]])]});}
            var Q161;
            {var subQ3=sQuery(id+"F0.wireOp",EDGE,"E8.5.18.0");var subQ6=sQuery(id+"F0.wireOp",EDGE,"E1");var subQ11=makeQuery(id+"F0.imprint","INTERSECT",VERTEX,{"derivedFrom":[subQ6,subQ3]});Q161=makeQuery(id+"F0.imprint","IMPRINT",FACE,{"disambiguationData":[TD([[makeQuery(id+"F0.imprint","IMPRINT",EDGE,{"disambiguationData":[TD([[subQ11,-1.0]])],"derivedFrom":subQ6}),1.0]])]});}
            var Q162;
            {var subQ0=sQuery(id+"F0.wireOp",EDGE,"E6.2.0");var subQ1=sQuery(id+"F0.wireOp",EDGE,"E2.5");var subQ2=makeQuery(id+"F0.imprint","INTERSECT",VERTEX,{"derivedFrom":[subQ1,subQ0]});Q162=makeQuery(id+"F0.imprint","IMPRINT",FACE,{"disambiguationData":[TD([[makeQuery(id+"F0.imprint","IMPRINT",EDGE,{"disambiguationData":[TD([[subQ2,-1.0]])],"derivedFrom":subQ1}),-1.0]])]});}
            var Q163;
            {var subQ1=sQuery(id+"F0.wireOp",EDGE,"E1");var subQ3=sQuery(id+"F0.wireOp",EDGE,"E8.3.15.0");var subQ4=makeQuery(id+"F0.imprint","INTERSECT",VERTEX,{"derivedFrom":[subQ1,subQ3]});Q163=makeQuery(id+"F0.imprint","IMPRINT",FACE,{"disambiguationData":[TD([[makeQuery(id+"F0.imprint","IMPRINT",EDGE,{"disambiguationData":[TD([[subQ4,-1.0]])],"derivedFrom":subQ3}),1.0]])]});}
            var Q164;
            {var subQ0=sQuery(id+"F0.wireOp",EDGE,"E7.5.6.0");var subQ1=sQuery(id+"F0.wireOp",EDGE,"E6.4.1");var subQ2=makeQuery(id+"F0.imprint","INTERSECT",VERTEX,{"derivedFrom":[subQ1,subQ0]});Q164=makeQuery(id+"F0.imprint","IMPRINT",FACE,{"disambiguationData":[TD([[makeQuery(id+"F0.imprint","IMPRINT",EDGE,{"disambiguationData":[TD([[subQ2,-1.0]])],"derivedFrom":subQ1}),-1.0]])]});}
            var Q165;
            {var subQ0=sQuery(id+"F0.wireOp",EDGE,"E8.5.19.0");var subQ1=sQuery(id+"F0.wireOp",EDGE,"E1");var subQ2=makeQuery(id+"F0.imprint","INTERSECT",VERTEX,{"derivedFrom":[subQ1,subQ0]});Q165=makeQuery(id+"F0.imprint","IMPRINT",FACE,{"disambiguationData":[TD([[makeQuery(id+"F0.imprint","IMPRINT",EDGE,{"disambiguationData":[TD([[subQ2,-1.0]])],"derivedFrom":subQ1}),1.0]])]});}
            var Q166;
            {var subQ0=sQuery(id+"F0.wireOp",EDGE,"E6.5.0");var subQ1=sQuery(id+"F0.wireOp",EDGE,"E6.4.1");var subQ2=makeQuery(id+"F0.imprint","INTERSECT",VERTEX,{"derivedFrom":[subQ1,subQ0]});Q166=makeQuery(id+"F0.imprint","IMPRINT",FACE,{"disambiguationData":[TD([[makeQuery(id+"F0.imprint","IMPRINT",EDGE,{"disambiguationData":[TD([[subQ2,-1.0]])],"derivedFrom":subQ1}),-1.0]])]});}
            var Q167;
            {var subQ0=sQuery(id+"F0.wireOp",EDGE,"E8.5.12.0");var subQ1=sQuery(id+"F0.wireOp",EDGE,"E2.3");var subQ2=makeQuery(id+"F0.imprint","INTERSECT",VERTEX,{"derivedFrom":[subQ1,subQ0]});Q167=makeQuery(id+"F0.imprint","IMPRINT",FACE,{"disambiguationData":[TD([[makeQuery(id+"F0.imprint","IMPRINT",EDGE,{"disambiguationData":[TD([[subQ2,-1.0]])],"derivedFrom":subQ1}),-1.0]])]});}
            var Q168;
            {var subQ1=sQuery(id+"F0.wireOp",EDGE,"E2.3");var subQ5=sQuery(id+"F0.wireOp",EDGE,"E8.3.12.0");var subQ6=makeQuery(id+"F0.imprint","INTERSECT",VERTEX,{"derivedFrom":[subQ1,subQ5]});Q168=makeQuery(id+"F0.imprint","IMPRINT",FACE,{"disambiguationData":[TD([[makeQuery(id+"F0.imprint","IMPRINT",EDGE,{"disambiguationData":[TD([[subQ6,-1.0]])],"derivedFrom":subQ1}),-1.0]])]});}
            var Q169;
            {var subQ1=sQuery(id+"F0.wireOp",EDGE,"E1");var subQ8=sQuery(id+"F0.wireOp",EDGE,"E9.5.26.0");var subQ11=makeQuery(id+"F0.imprint","INTERSECT",VERTEX,{"derivedFrom":[subQ1,subQ8]});Q169=makeQuery(id+"F0.imprint","IMPRINT",FACE,{"disambiguationData":[TD([[makeQuery(id+"F0.imprint","IMPRINT",EDGE,{"disambiguationData":[TD([[subQ11,-1.0]])],"derivedFrom":subQ1}),1.0]])]});}
            var Q170;
            {var subQ5=sQuery(id+"F0.wireOp",EDGE,"E9.3.28.0");var subQ7=sQuery(id+"F0.wireOp",EDGE,"E2.0");var subQ8=makeQuery(id+"F0.imprint","INTERSECT",VERTEX,{"derivedFrom":[subQ7,subQ5]});Q170=makeQuery(id+"F0.imprint","IMPRINT",FACE,{"disambiguationData":[TD([[makeQuery(id+"F0.imprint","IMPRINT",EDGE,{"disambiguationData":[TD([[subQ8,-1.0]])],"derivedFrom":subQ7}),-1.0]])]});}
            var Q171;
            {var subQ1=sQuery(id+"F0.wireOp",EDGE,"E2.3");var subQ7=sQuery(id+"F0.wireOp",EDGE,"E7.3.11.0");var subQ8=makeQuery(id+"F0.imprint","INTERSECT",VERTEX,{"derivedFrom":[subQ1,subQ7]});Q171=makeQuery(id+"F0.imprint","IMPRINT",FACE,{"disambiguationData":[TD([[makeQuery(id+"F0.imprint","IMPRINT",EDGE,{"disambiguationData":[TD([[subQ8,-1.0]])],"derivedFrom":subQ1}),-1.0]])]});}
            var Q172;
            {var subQ3=sQuery(id+"F0.wireOp",EDGE,"E9.5.27.0");var subQ6=sQuery(id+"F0.wireOp",EDGE,"E1");var subQ11=makeQuery(id+"F0.imprint","INTERSECT",VERTEX,{"derivedFrom":[subQ6,subQ3]});Q172=makeQuery(id+"F0.imprint","IMPRINT",FACE,{"disambiguationData":[TD([[makeQuery(id+"F0.imprint","IMPRINT",EDGE,{"disambiguationData":[TD([[subQ11,-1.0]])],"derivedFrom":subQ6}),1.0]])]});}
            var Q173;
            {var subQ1=sQuery(id+"F0.wireOp",EDGE,"E1");var subQ3=sQuery(id+"F0.wireOp",EDGE,"E6.5.1");var subQ4=makeQuery(id+"F0.imprint","INTERSECT",VERTEX,{"derivedFrom":[subQ1,subQ3]});Q173=makeQuery(id+"F0.imprint","IMPRINT",FACE,{"disambiguationData":[TD([[makeQuery(id+"F0.imprint","IMPRINT",EDGE,{"disambiguationData":[TD([[subQ4,-1.0]])],"derivedFrom":subQ3}),1.0]])]});}
            var Q174;
            {var subQ1=sQuery(id+"F0.wireOp",EDGE,"E1");var subQ3=sQuery(id+"F0.wireOp",EDGE,"E8.5.21.0");var subQ4=makeQuery(id+"F0.imprint","INTERSECT",VERTEX,{"derivedFrom":[subQ1,subQ3]});Q174=makeQuery(id+"F0.imprint","IMPRINT",FACE,{"disambiguationData":[TD([[makeQuery(id+"F0.imprint","IMPRINT",EDGE,{"disambiguationData":[TD([[subQ4,-1.0]])],"derivedFrom":subQ3}),1.0]])]});}
            var Q175;
            {var subQ0=sQuery(id+"F0.wireOp",EDGE,"E8.5.20.0");var subQ1=sQuery(id+"F0.wireOp",EDGE,"E2.2");var subQ2=makeQuery(id+"F0.imprint","INTERSECT",VERTEX,{"derivedFrom":[subQ1,subQ0]});Q175=makeQuery(id+"F0.imprint","IMPRINT",FACE,{"disambiguationData":[TD([[makeQuery(id+"F0.imprint","IMPRINT",EDGE,{"disambiguationData":[TD([[subQ2,-1.0]])],"derivedFrom":subQ1}),-1.0]])]});}
            var Q176;
            {var subQ0=sQuery(id+"F0.wireOp",EDGE,"E8.3.20.0");var subQ1=sQuery(id+"F0.wireOp",EDGE,"E1");var subQ2=makeQuery(id+"F0.imprint","INTERSECT",VERTEX,{"derivedFrom":[subQ1,subQ0]});Q176=makeQuery(id+"F0.imprint","IMPRINT",FACE,{"disambiguationData":[TD([[makeQuery(id+"F0.imprint","IMPRINT",EDGE,{"disambiguationData":[TD([[subQ2,-1.0]])],"derivedFrom":subQ1}),1.0]])]});}
            var Q177;
            {var subQ1=sQuery(id+"F0.wireOp",EDGE,"E1");var subQ9=sQuery(id+"F0.wireOp",EDGE,"E9.5.28.0");var subQ11=makeQuery(id+"F0.imprint","INTERSECT",VERTEX,{"derivedFrom":[subQ1,subQ9]});Q177=makeQuery(id+"F0.imprint","IMPRINT",FACE,{"disambiguationData":[TD([[makeQuery(id+"F0.imprint","IMPRINT",EDGE,{"disambiguationData":[TD([[subQ11,-1.0]])],"derivedFrom":subQ1}),1.0]])]});}
            var Q178;
            {var subQ0=sQuery(id+"F0.wireOp",EDGE,"E7.3.6.0");var subQ1=sQuery(id+"F0.wireOp",EDGE,"E1");var subQ2=makeQuery(id+"F0.imprint","INTERSECT",VERTEX,{"derivedFrom":[subQ1,subQ0]});Q178=makeQuery(id+"F0.imprint","IMPRINT",FACE,{"disambiguationData":[TD([[makeQuery(id+"F0.imprint","IMPRINT",EDGE,{"disambiguationData":[TD([[subQ2,-1.0]])],"derivedFrom":subQ1}),1.0]])]});}
            var Q179;
            {var subQ0=sQuery(id+"F0.wireOp",EDGE,"E8.5.21.0");var subQ1=sQuery(id+"F0.wireOp",EDGE,"E1");var subQ2=makeQuery(id+"F0.imprint","INTERSECT",VERTEX,{"derivedFrom":[subQ1,subQ0]});Q179=makeQuery(id+"F0.imprint","IMPRINT",FACE,{"disambiguationData":[TD([[makeQuery(id+"F0.imprint","IMPRINT",EDGE,{"disambiguationData":[TD([[subQ2,-1.0]])],"derivedFrom":subQ1}),-1.0]])]});}
            var Q180;
            {var subQ1=sQuery(id+"F0.wireOp",EDGE,"E2.0");var subQ5=sQuery(id+"F0.wireOp",EDGE,"E9.3.26.0");var subQ6=makeQuery(id+"F0.imprint","INTERSECT",VERTEX,{"derivedFrom":[subQ1,subQ5]});Q180=makeQuery(id+"F0.imprint","IMPRINT",FACE,{"disambiguationData":[TD([[makeQuery(id+"F0.imprint","IMPRINT",EDGE,{"disambiguationData":[TD([[subQ6,-1.0]])],"derivedFrom":subQ1}),-1.0]])]});}
            var Q181;
            {var subQ3=sQuery(id+"F0.wireOp",EDGE,"E9.5.29.0");var subQ9=sQuery(id+"F0.wireOp",EDGE,"E1");var subQ10=makeQuery(id+"F0.imprint","INTERSECT",VERTEX,{"derivedFrom":[subQ9,subQ3]});Q181=makeQuery(id+"F0.imprint","IMPRINT",FACE,{"disambiguationData":[TD([[makeQuery(id+"F0.imprint","IMPRINT",EDGE,{"disambiguationData":[TD([[subQ10,-1.0]])],"derivedFrom":subQ9}),1.0]])]});}
            var Q182;
            {var subQ0=sQuery(id+"F0.wireOp",EDGE,"E8.5.22.0");var subQ1=sQuery(id+"F0.wireOp",EDGE,"E1");var subQ2=makeQuery(id+"F0.imprint","INTERSECT",VERTEX,{"derivedFrom":[subQ1,subQ0]});Q182=makeQuery(id+"F0.imprint","IMPRINT",FACE,{"disambiguationData":[TD([[makeQuery(id+"F0.imprint","IMPRINT",EDGE,{"disambiguationData":[TD([[subQ2,-1.0]])],"derivedFrom":subQ1}),-1.0]])]});}
            var Q183;
            {var subQ0=sQuery(id+"F0.wireOp",EDGE,"E8.5.19.0");var subQ1=sQuery(id+"F0.wireOp",EDGE,"E2.2");var subQ2=makeQuery(id+"F0.imprint","INTERSECT",VERTEX,{"derivedFrom":[subQ1,subQ0]});Q183=makeQuery(id+"F0.imprint","IMPRINT",FACE,{"disambiguationData":[TD([[makeQuery(id+"F0.imprint","IMPRINT",EDGE,{"disambiguationData":[TD([[subQ2,-1.0]])],"derivedFrom":subQ1}),-1.0]])]});}
            var Q184;
            {var subQ0=sQuery(id+"F0.wireOp",EDGE,"E7.5.9.0");var subQ1=sQuery(id+"F0.wireOp",EDGE,"E2.4");var subQ2=makeQuery(id+"F0.imprint","INTERSECT",VERTEX,{"derivedFrom":[subQ1,subQ0]});Q184=makeQuery(id+"F0.imprint","IMPRINT",FACE,{"disambiguationData":[TD([[makeQuery(id+"F0.imprint","IMPRINT",EDGE,{"disambiguationData":[TD([[subQ2,-1.0]])],"derivedFrom":subQ1}),-1.0]])]});}
            var Q185;
            {var subQ0=sQuery(id+"F0.wireOp",EDGE,"E8.3.22.0");var subQ1=sQuery(id+"F0.wireOp",EDGE,"E1");var subQ2=makeQuery(id+"F0.imprint","INTERSECT",VERTEX,{"derivedFrom":[subQ1,subQ0]});Q185=makeQuery(id+"F0.imprint","IMPRINT",FACE,{"disambiguationData":[TD([[makeQuery(id+"F0.imprint","IMPRINT",EDGE,{"disambiguationData":[TD([[subQ2,-1.0]])],"derivedFrom":subQ1}),1.0]])]});}
            var Q186;
            {var subQ0=sQuery(id+"F0.wireOp",EDGE,"E8.5.23.0");var subQ1=sQuery(id+"F0.wireOp",EDGE,"E1");var subQ2=makeQuery(id+"F0.imprint","INTERSECT",VERTEX,{"derivedFrom":[subQ1,subQ0]});Q186=makeQuery(id+"F0.imprint","IMPRINT",FACE,{"disambiguationData":[TD([[makeQuery(id+"F0.imprint","IMPRINT",EDGE,{"disambiguationData":[TD([[subQ2,1.0]])],"derivedFrom":subQ1}),1.0]])]});}
            var Q187;
            {var subQ0=sQuery(id+"F0.wireOp",EDGE,"E8.5.20.0");var subQ1=sQuery(id+"F0.wireOp",EDGE,"E8.3.17.0");var subQ2=makeQuery(id+"F0.imprint","INTERSECT",VERTEX,{"derivedFrom":[subQ1,subQ0]});Q187=makeQuery(id+"F0.imprint","IMPRINT",FACE,{"disambiguationData":[TD([[makeQuery(id+"F0.imprint","IMPRINT",EDGE,{"disambiguationData":[TD([[subQ2,-1.0]])],"derivedFrom":subQ1}),-1.0]])]});}
            var Q188;
            {var subQ1=sQuery(id+"F0.wireOp",EDGE,"E2.0");var subQ5=sQuery(id+"F0.wireOp",EDGE,"E9.3.25.0");var subQ6=makeQuery(id+"F0.imprint","INTERSECT",VERTEX,{"derivedFrom":[subQ1,subQ5]});Q188=makeQuery(id+"F0.imprint","IMPRINT",FACE,{"disambiguationData":[TD([[makeQuery(id+"F0.imprint","IMPRINT",EDGE,{"disambiguationData":[TD([[subQ6,-1.0]])],"derivedFrom":subQ1}),-1.0]])]});}
            var Q189;
            {var subQ3=sQuery(id+"F0.wireOp",EDGE,"E6.1.0");var subQ5=sQuery(id+"F0.wireOp",EDGE,"E1");var subQ6=makeQuery(id+"F0.imprint","INTERSECT",VERTEX,{"derivedFrom":[subQ5,subQ3]});Q189=makeQuery(id+"F0.imprint","IMPRINT",FACE,{"disambiguationData":[TD([[makeQuery(id+"F0.imprint","IMPRINT",EDGE,{"disambiguationData":[TD([[subQ6,-1.0]])],"derivedFrom":subQ5}),1.0]])]});}
            var Q190;
            {var subQ0=sQuery(id+"F0.wireOp",EDGE,"E7.3.10.0");var subQ1=sQuery(id+"F0.wireOp",EDGE,"E1");var subQ2=makeQuery(id+"F0.imprint","INTERSECT",VERTEX,{"derivedFrom":[subQ1,subQ0]});Q190=makeQuery(id+"F0.imprint","IMPRINT",FACE,{"disambiguationData":[TD([[makeQuery(id+"F0.imprint","IMPRINT",EDGE,{"disambiguationData":[TD([[subQ2,-1.0]])],"derivedFrom":subQ1}),1.0]])]});}
            var Q191;
            {var subQ0=sQuery(id+"F0.wireOp",EDGE,"E9.3.28.0");var subQ1=sQuery(id+"F0.wireOp",EDGE,"E2.0");var subQ2=makeQuery(id+"F0.imprint","INTERSECT",VERTEX,{"derivedFrom":[subQ1,subQ0]});Q191=makeQuery(id+"F0.imprint","IMPRINT",FACE,{"disambiguationData":[TD([[makeQuery(id+"F0.imprint","IMPRINT",EDGE,{"disambiguationData":[TD([[subQ2,-1.0]])],"derivedFrom":subQ1}),1.0]])]});}
            var Q192;
            {var subQ0=sQuery(id+"F0.wireOp",EDGE,"E8.3.16.0");var subQ1=sQuery(id+"F0.wireOp",EDGE,"E2.2");var subQ2=makeQuery(id+"F0.imprint","INTERSECT",VERTEX,{"derivedFrom":[subQ1,subQ0]});Q192=makeQuery(id+"F0.imprint","IMPRINT",FACE,{"disambiguationData":[TD([[makeQuery(id+"F0.imprint","IMPRINT",EDGE,{"disambiguationData":[TD([[subQ2,-1.0]])],"derivedFrom":subQ1}),1.0]])]});}
            var Q193;
            {var subQ0=sQuery(id+"F0.wireOp",EDGE,"E7.3.6.0");var subQ1=sQuery(id+"F0.wireOp",EDGE,"E2.4");var subQ2=makeQuery(id+"F0.imprint","INTERSECT",VERTEX,{"derivedFrom":[subQ1,subQ0]});Q193=makeQuery(id+"F0.imprint","IMPRINT",FACE,{"disambiguationData":[TD([[makeQuery(id+"F0.imprint","IMPRINT",EDGE,{"disambiguationData":[TD([[subQ2,-1.0]])],"derivedFrom":subQ1}),1.0]])]});}
            var Q194;
            {var subQ0=sQuery(id+"F0.wireOp",EDGE,"E8.3.17.0");var subQ1=sQuery(id+"F0.wireOp",EDGE,"E2.2");var subQ2=makeQuery(id+"F0.imprint","INTERSECT",VERTEX,{"derivedFrom":[subQ1,subQ0]});Q194=makeQuery(id+"F0.imprint","IMPRINT",FACE,{"disambiguationData":[TD([[makeQuery(id+"F0.imprint","IMPRINT",EDGE,{"disambiguationData":[TD([[subQ2,-1.0]])],"derivedFrom":subQ1}),1.0]])]});}
            var Q195;
            {var subQ0=sQuery(id+"F0.wireOp",EDGE,"E7.3.7.0");var subQ1=sQuery(id+"F0.wireOp",EDGE,"E2.4");var subQ2=makeQuery(id+"F0.imprint","INTERSECT",VERTEX,{"derivedFrom":[subQ1,subQ0]});Q195=makeQuery(id+"F0.imprint","IMPRINT",FACE,{"disambiguationData":[TD([[makeQuery(id+"F0.imprint","IMPRINT",EDGE,{"disambiguationData":[TD([[subQ2,-1.0]])],"derivedFrom":subQ1}),1.0]])]});}
            var Q196;
            {var subQ0=sQuery(id+"F0.wireOp",EDGE,"E9.5.24.0");var subQ1=sQuery(id+"F0.wireOp",EDGE,"E1");var subQ2=makeQuery(id+"F0.imprint","INTERSECT",VERTEX,{"derivedFrom":[subQ1,subQ0]});Q196=makeQuery(id+"F0.imprint","IMPRINT",FACE,{"disambiguationData":[TD([[makeQuery(id+"F0.imprint","IMPRINT",EDGE,{"disambiguationData":[TD([[subQ2,-1.0]])],"derivedFrom":subQ1}),1.0]])]});}
            var Q197;
            {var subQ1=sQuery(id+"F0.wireOp",EDGE,"E2.1");var subQ5=sQuery(id+"F0.wireOp",EDGE,"E9.3.24.0");var subQ6=makeQuery(id+"F0.imprint","INTERSECT",VERTEX,{"derivedFrom":[subQ1,subQ5]});Q197=makeQuery(id+"F0.imprint","IMPRINT",FACE,{"disambiguationData":[TD([[makeQuery(id+"F0.imprint","IMPRINT",EDGE,{"disambiguationData":[TD([[subQ6,-1.0]])],"derivedFrom":subQ1}),-1.0]])]});}
            var Q198;
            {var subQ0=sQuery(id+"F0.wireOp",EDGE,"E9.5.25.0");var subQ1=sQuery(id+"F0.wireOp",EDGE,"E1");var subQ2=makeQuery(id+"F0.imprint","INTERSECT",VERTEX,{"derivedFrom":[subQ1,subQ0]});Q198=makeQuery(id+"F0.imprint","IMPRINT",FACE,{"disambiguationData":[TD([[makeQuery(id+"F0.imprint","IMPRINT",EDGE,{"disambiguationData":[TD([[subQ2,-1.0]])],"derivedFrom":subQ1}),-1.0]])]});}
            var Q199;
            {var subQ1=sQuery(id+"F0.wireOp",EDGE,"E1");var subQ3=sQuery(id+"F0.wireOp",EDGE,"E7.5.10.0");var subQ4=makeQuery(id+"F0.imprint","INTERSECT",VERTEX,{"derivedFrom":[subQ1,subQ3]});Q199=makeQuery(id+"F0.imprint","IMPRINT",FACE,{"disambiguationData":[TD([[makeQuery(id+"F0.imprint","IMPRINT",EDGE,{"disambiguationData":[TD([[subQ4,-1.0]])],"derivedFrom":subQ3}),-1.0]])]});}
            var Q200;
            {var subQ0=sQuery(id+"F0.wireOp",EDGE,"E6.4.0");var subQ1=sQuery(id+"F0.wireOp",EDGE,"E6.1.1");var subQ2=makeQuery(id+"F0.imprint","INTERSECT",VERTEX,{"derivedFrom":[subQ1,subQ0]});Q200=makeQuery(id+"F0.imprint","IMPRINT",FACE,{"disambiguationData":[TD([[makeQuery(id+"F0.imprint","IMPRINT",EDGE,{"disambiguationData":[TD([[subQ2,-1.0]])],"derivedFrom":subQ1}),-1.0]])]});}
            var Q201;
            {var subQ0=sQuery(id+"F0.wireOp",EDGE,"E7.5.8.0");var subQ1=sQuery(id+"F0.wireOp",EDGE,"E6.5.1");var subQ2=makeQuery(id+"F0.imprint","INTERSECT",VERTEX,{"derivedFrom":[subQ1,subQ0]});Q201=makeQuery(id+"F0.imprint","IMPRINT",FACE,{"disambiguationData":[TD([[makeQuery(id+"F0.imprint","IMPRINT",EDGE,{"disambiguationData":[TD([[subQ2,-1.0]])],"derivedFrom":subQ1}),-1.0]])]});}
            var Q202;
            {var subQ0=sQuery(id+"F0.wireOp",EDGE,"E9.3.25.0");var subQ1=sQuery(id+"F0.wireOp",EDGE,"E1");var subQ2=makeQuery(id+"F0.imprint","INTERSECT",VERTEX,{"derivedFrom":[subQ1,subQ0]});Q202=makeQuery(id+"F0.imprint","IMPRINT",FACE,{"disambiguationData":[TD([[makeQuery(id+"F0.imprint","IMPRINT",EDGE,{"disambiguationData":[TD([[subQ2,-1.0]])],"derivedFrom":subQ1}),1.0]])]});}
            var Q203;
            {var subQ0=sQuery(id+"F0.wireOp",EDGE,"E7.5.6.0");var subQ1=sQuery(id+"F0.wireOp",EDGE,"E2.4");var subQ2=makeQuery(id+"F0.imprint","INTERSECT",VERTEX,{"derivedFrom":[subQ1,subQ0]});Q203=makeQuery(id+"F0.imprint","IMPRINT",FACE,{"disambiguationData":[TD([[makeQuery(id+"F0.imprint","IMPRINT",EDGE,{"disambiguationData":[TD([[subQ2,-1.0]])],"derivedFrom":subQ1}),-1.0]])]});}
            var Q204;
            {var subQ1=sQuery(id+"F0.wireOp",EDGE,"E1");var subQ3=sQuery(id+"F0.wireOp",EDGE,"E9.3.25.0");var subQ4=makeQuery(id+"F0.imprint","INTERSECT",VERTEX,{"derivedFrom":[subQ1,subQ3]});Q204=makeQuery(id+"F0.imprint","IMPRINT",FACE,{"disambiguationData":[TD([[makeQuery(id+"F0.imprint","IMPRINT",EDGE,{"disambiguationData":[TD([[subQ4,-1.0]])],"derivedFrom":subQ3}),1.0]])]});}
            var Q205;
            {var subQ0=sQuery(id+"F0.wireOp",EDGE,"E9.3.26.0");var subQ1=sQuery(id+"F0.wireOp",EDGE,"E1");var subQ2=makeQuery(id+"F0.imprint","INTERSECT",VERTEX,{"derivedFrom":[subQ1,subQ0]});Q205=makeQuery(id+"F0.imprint","IMPRINT",FACE,{"disambiguationData":[TD([[makeQuery(id+"F0.imprint","IMPRINT",EDGE,{"disambiguationData":[TD([[subQ2,-1.0]])],"derivedFrom":subQ1}),1.0]])]});}
            var Q206;
            {var subQ0=sQuery(id+"F0.wireOp",EDGE,"E8.3.15.0");var subQ1=sQuery(id+"F0.wireOp",EDGE,"E2.2");var subQ2=makeQuery(id+"F0.imprint","INTERSECT",VERTEX,{"derivedFrom":[subQ1,subQ0]});Q206=makeQuery(id+"F0.imprint","IMPRINT",FACE,{"disambiguationData":[TD([[makeQuery(id+"F0.imprint","IMPRINT",EDGE,{"disambiguationData":[TD([[subQ2,-1.0]])],"derivedFrom":subQ1}),1.0]])]});}
            var Q207;
            {var subQ0=sQuery(id+"F0.wireOp",EDGE,"E6.5.0");var subQ1=sQuery(id+"F0.wireOp",EDGE,"E2.5");var subQ2=makeQuery(id+"F0.imprint","INTERSECT",VERTEX,{"derivedFrom":[subQ1,subQ0]});Q207=makeQuery(id+"F0.imprint","IMPRINT",FACE,{"disambiguationData":[TD([[makeQuery(id+"F0.imprint","IMPRINT",EDGE,{"disambiguationData":[TD([[subQ2,-1.0]])],"derivedFrom":subQ1}),-1.0]])]});}
            var Q208;
            {var subQ1=sQuery(id+"F0.wireOp",EDGE,"E1");var subQ3=sQuery(id+"F0.wireOp",EDGE,"E4");var subQ4=makeQuery(id+"F0.imprint","INTERSECT",VERTEX,{"derivedFrom":[subQ1,subQ3]});Q208=makeQuery(id+"F0.imprint","IMPRINT",FACE,{"disambiguationData":[TD([[makeQuery(id+"F0.imprint","IMPRINT",EDGE,{"disambiguationData":[TD([[subQ4,-1.0]])],"derivedFrom":subQ3}),-1.0]])]});}
            var Q209;
            {var subQ0=sQuery(id+"F0.wireOp",EDGE,"E8.3.13.0");var subQ1=sQuery(id+"F0.wireOp",EDGE,"E1");var subQ2=makeQuery(id+"F0.imprint","INTERSECT",VERTEX,{"derivedFrom":[subQ1,subQ0]});Q209=makeQuery(id+"F0.imprint","IMPRINT",FACE,{"disambiguationData":[TD([[makeQuery(id+"F0.imprint","IMPRINT",EDGE,{"disambiguationData":[TD([[subQ2,-1.0]])],"derivedFrom":subQ1}),1.0]])]});}
            var Q210;
            {var subQ0=sQuery(id+"F0.wireOp",EDGE,"E6.3.1");var subQ1=sQuery(id+"F0.wireOp",EDGE,"E2.5");var subQ2=makeQuery(id+"F0.imprint","INTERSECT",VERTEX,{"derivedFrom":[subQ1,subQ0]});Q210=makeQuery(id+"F0.imprint","IMPRINT",FACE,{"disambiguationData":[TD([[makeQuery(id+"F0.imprint","IMPRINT",EDGE,{"disambiguationData":[TD([[subQ2,-1.0]])],"derivedFrom":subQ1}),1.0]])]});}
            var Q211;
            {var subQ0=sQuery(id+"F0.wireOp",EDGE,"E8.5.15.0");var subQ1=sQuery(id+"F0.wireOp",EDGE,"E8.3.12.0");var subQ2=makeQuery(id+"F0.imprint","INTERSECT",VERTEX,{"derivedFrom":[subQ1,subQ0]});Q211=makeQuery(id+"F0.imprint","IMPRINT",FACE,{"disambiguationData":[TD([[makeQuery(id+"F0.imprint","IMPRINT",EDGE,{"disambiguationData":[TD([[subQ2,-1.0]])],"derivedFrom":subQ1}),-1.0]])]});}
            var Q212;
            {var subQ1=sQuery(id+"F0.wireOp",EDGE,"E2.2");var subQ7=sQuery(id+"F0.wireOp",EDGE,"E8.3.19.0");var subQ8=makeQuery(id+"F0.imprint","INTERSECT",VERTEX,{"derivedFrom":[subQ1,subQ7]});Q212=makeQuery(id+"F0.imprint","IMPRINT",FACE,{"disambiguationData":[TD([[makeQuery(id+"F0.imprint","IMPRINT",EDGE,{"disambiguationData":[TD([[subQ8,-1.0]])],"derivedFrom":subQ1}),-1.0]])]});}
            var Q213;
            {var subQ1=sQuery(id+"F0.wireOp",EDGE,"E1");var subQ3=sQuery(id+"F0.wireOp",EDGE,"E8.3.14.0");var subQ4=makeQuery(id+"F0.imprint","INTERSECT",VERTEX,{"derivedFrom":[subQ1,subQ3]});Q213=makeQuery(id+"F0.imprint","IMPRINT",FACE,{"disambiguationData":[TD([[makeQuery(id+"F0.imprint","IMPRINT",EDGE,{"disambiguationData":[TD([[subQ4,-1.0]])],"derivedFrom":subQ3}),-1.0]])]});}
            var Q214;
            {var subQ0=sQuery(id+"F0.wireOp",EDGE,"E6.2.1");var subQ1=sQuery(id+"F0.wireOp",EDGE,"E2.5");var subQ2=makeQuery(id+"F0.imprint","INTERSECT",VERTEX,{"derivedFrom":[subQ1,subQ0]});Q214=makeQuery(id+"F0.imprint","IMPRINT",FACE,{"disambiguationData":[TD([[makeQuery(id+"F0.imprint","IMPRINT",EDGE,{"disambiguationData":[TD([[subQ2,-1.0]])],"derivedFrom":subQ1}),1.0]])]});}
            var Q215;
            {var subQ0=sQuery(id+"F0.wireOp",EDGE,"E6.5.1");var subQ1=sQuery(id+"F0.wireOp",EDGE,"E1");var subQ2=makeQuery(id+"F0.imprint","INTERSECT",VERTEX,{"derivedFrom":[subQ1,subQ0]});Q215=makeQuery(id+"F0.imprint","IMPRINT",FACE,{"disambiguationData":[TD([[makeQuery(id+"F0.imprint","IMPRINT",EDGE,{"disambiguationData":[TD([[subQ2,-1.0]])],"derivedFrom":subQ1}),1.0]])]});}
            var Q216;
            {var subQ0=sQuery(id+"F0.wireOp",EDGE,"E8.3.16.0");var subQ1=sQuery(id+"F0.wireOp",EDGE,"E1");var subQ2=makeQuery(id+"F0.imprint","INTERSECT",VERTEX,{"derivedFrom":[subQ1,subQ0]});Q216=makeQuery(id+"F0.imprint","IMPRINT",FACE,{"disambiguationData":[TD([[makeQuery(id+"F0.imprint","IMPRINT",EDGE,{"disambiguationData":[TD([[subQ2,-1.0]])],"derivedFrom":subQ1}),1.0]])]});}
            var Q217;
            {var subQ0=sQuery(id+"F0.wireOp",EDGE,"E9.3.28.0");var subQ1=sQuery(id+"F0.wireOp",EDGE,"E4");var subQ2=makeQuery(id+"F0.imprint","INTERSECT",VERTEX,{"derivedFrom":[subQ1,subQ0]});Q217=makeQuery(id+"F0.imprint","IMPRINT",FACE,{"disambiguationData":[TD([[makeQuery(id+"F0.imprint","IMPRINT",EDGE,{"disambiguationData":[TD([[subQ2,-1.0]])],"derivedFrom":subQ1}),-1.0]])]});}
            var Q218;
            {var subQ0=sQuery(id+"F0.wireOp",EDGE,"E8.3.17.0");var subQ1=sQuery(id+"F0.wireOp",EDGE,"E1");var subQ2=makeQuery(id+"F0.imprint","INTERSECT",VERTEX,{"derivedFrom":[subQ1,subQ0]});Q218=makeQuery(id+"F0.imprint","IMPRINT",FACE,{"disambiguationData":[TD([[makeQuery(id+"F0.imprint","IMPRINT",EDGE,{"disambiguationData":[TD([[subQ2,-1.0]])],"derivedFrom":subQ1}),1.0]])]});}
            var Q219;
            {var subQ0=sQuery(id+"F0.wireOp",EDGE,"E6.1.1");var subQ1=sQuery(id+"F0.wireOp",EDGE,"E2.5");var subQ2=makeQuery(id+"F0.imprint","INTERSECT",VERTEX,{"derivedFrom":[subQ1,subQ0]});Q219=makeQuery(id+"F0.imprint","IMPRINT",FACE,{"disambiguationData":[TD([[makeQuery(id+"F0.imprint","IMPRINT",EDGE,{"disambiguationData":[TD([[subQ2,-1.0]])],"derivedFrom":subQ1}),1.0]])]});}
            var Q220;
            {var subQ0=sQuery(id+"F0.wireOp",EDGE,"E8.5.22.0");var subQ1=sQuery(id+"F0.wireOp",EDGE,"E8.3.19.0");var subQ2=makeQuery(id+"F0.imprint","INTERSECT",VERTEX,{"derivedFrom":[subQ1,subQ0]});Q220=makeQuery(id+"F0.imprint","IMPRINT",FACE,{"disambiguationData":[TD([[makeQuery(id+"F0.imprint","IMPRINT",EDGE,{"disambiguationData":[TD([[subQ2,-1.0]])],"derivedFrom":subQ1}),-1.0]])]});}
            var Q221;
            {var subQ0=sQuery(id+"F0.wireOp",EDGE,"E8.3.18.0");var subQ1=sQuery(id+"F0.wireOp",EDGE,"E1");var subQ2=makeQuery(id+"F0.imprint","INTERSECT",VERTEX,{"derivedFrom":[subQ1,subQ0]});Q221=makeQuery(id+"F0.imprint","IMPRINT",FACE,{"disambiguationData":[TD([[makeQuery(id+"F0.imprint","IMPRINT",EDGE,{"disambiguationData":[TD([[subQ2,-1.0]])],"derivedFrom":subQ1}),1.0]])]});}
            var Q222;
            {var subQ0=sQuery(id+"F0.wireOp",EDGE,"E7.3.11.0");var subQ1=sQuery(id+"F0.wireOp",EDGE,"E2.3");var subQ2=makeQuery(id+"F0.imprint","INTERSECT",VERTEX,{"derivedFrom":[subQ1,subQ0]});Q222=makeQuery(id+"F0.imprint","IMPRINT",FACE,{"disambiguationData":[TD([[makeQuery(id+"F0.imprint","IMPRINT",EDGE,{"disambiguationData":[TD([[subQ2,-1.0]])],"derivedFrom":subQ1}),1.0]])]});}
            var Q223;
            {var subQ0=sQuery(id+"F0.wireOp",EDGE,"E6.5.0");var subQ1=sQuery(id+"F0.wireOp",EDGE,"E6.2.1");var subQ2=makeQuery(id+"F0.imprint","INTERSECT",VERTEX,{"derivedFrom":[subQ1,subQ0]});Q223=makeQuery(id+"F0.imprint","IMPRINT",FACE,{"disambiguationData":[TD([[makeQuery(id+"F0.imprint","IMPRINT",EDGE,{"disambiguationData":[TD([[subQ2,-1.0]])],"derivedFrom":subQ1}),-1.0]])]});}
            var Q224;
            {var subQ0=sQuery(id+"F0.wireOp",EDGE,"E8.5.15.0");var subQ1=sQuery(id+"F0.wireOp",EDGE,"E8.3.13.0");var subQ2=makeQuery(id+"F0.imprint","INTERSECT",VERTEX,{"derivedFrom":[subQ1,subQ0]});Q224=makeQuery(id+"F0.imprint","IMPRINT",FACE,{"disambiguationData":[TD([[makeQuery(id+"F0.imprint","IMPRINT",EDGE,{"disambiguationData":[TD([[subQ2,-1.0]])],"derivedFrom":subQ1}),-1.0]])]});}
            var Q225;
            {var subQ0=sQuery(id+"F0.wireOp",EDGE,"E8.5.19.0");var subQ1=sQuery(id+"F0.wireOp",EDGE,"E8.3.16.0");var subQ2=makeQuery(id+"F0.imprint","INTERSECT",VERTEX,{"derivedFrom":[subQ1,subQ0]});Q225=makeQuery(id+"F0.imprint","IMPRINT",FACE,{"disambiguationData":[TD([[makeQuery(id+"F0.imprint","IMPRINT",EDGE,{"disambiguationData":[TD([[subQ2,-1.0]])],"derivedFrom":subQ1}),-1.0]])]});}
            var Q226;
            {var subQ1=sQuery(id+"F0.wireOp",EDGE,"E2.3");var subQ5=sQuery(id+"F0.wireOp",EDGE,"E8.3.13.0");var subQ6=makeQuery(id+"F0.imprint","INTERSECT",VERTEX,{"derivedFrom":[subQ1,subQ5]});Q226=makeQuery(id+"F0.imprint","IMPRINT",FACE,{"disambiguationData":[TD([[makeQuery(id+"F0.imprint","IMPRINT",EDGE,{"disambiguationData":[TD([[subQ6,-1.0]])],"derivedFrom":subQ1}),-1.0]])]});}
            var Q227;
            {var subQ0=sQuery(id+"F0.wireOp",EDGE,"E8.5.20.0");var subQ1=sQuery(id+"F0.wireOp",EDGE,"E1");var subQ2=makeQuery(id+"F0.imprint","INTERSECT",VERTEX,{"derivedFrom":[subQ1,subQ0]});Q227=makeQuery(id+"F0.imprint","IMPRINT",FACE,{"disambiguationData":[TD([[makeQuery(id+"F0.imprint","IMPRINT",EDGE,{"disambiguationData":[TD([[subQ2,-1.0]])],"derivedFrom":subQ1}),-1.0]])]});}
            var Q228;
            {var subQ0=sQuery(id+"F0.wireOp",EDGE,"E7.5.7.0");var subQ1=sQuery(id+"F0.wireOp",EDGE,"E6.4.1");var subQ2=makeQuery(id+"F0.imprint","INTERSECT",VERTEX,{"derivedFrom":[subQ1,subQ0]});Q228=makeQuery(id+"F0.imprint","IMPRINT",FACE,{"disambiguationData":[TD([[makeQuery(id+"F0.imprint","IMPRINT",EDGE,{"disambiguationData":[TD([[subQ2,-1.0]])],"derivedFrom":subQ1}),-1.0]])]});}
            var Q229;
            {var subQ0=sQuery(id+"F0.wireOp",EDGE,"E7.5.10.0");var subQ1=sQuery(id+"F0.wireOp",EDGE,"E7.3.7.0");var subQ2=makeQuery(id+"F0.imprint","INTERSECT",VERTEX,{"derivedFrom":[subQ1,subQ0]});Q229=makeQuery(id+"F0.imprint","IMPRINT",FACE,{"disambiguationData":[TD([[makeQuery(id+"F0.imprint","IMPRINT",EDGE,{"disambiguationData":[TD([[subQ2,-1.0]])],"derivedFrom":subQ1}),-1.0]])]});}
            var Q230;
            {var subQ5=sQuery(id+"F0.wireOp",EDGE,"E9.3.29.0");var subQ7=sQuery(id+"F0.wireOp",EDGE,"E2.0");var subQ9=makeQuery(id+"F0.imprint","INTERSECT",VERTEX,{"derivedFrom":[subQ7,subQ5]});Q230=makeQuery(id+"F0.imprint","IMPRINT",FACE,{"disambiguationData":[TD([[makeQuery(id+"F0.imprint","IMPRINT",EDGE,{"disambiguationData":[TD([[subQ9,-1.0]])],"derivedFrom":subQ7}),-1.0]])]});}
            var Q231;
            {var subQ0=sQuery(id+"F0.wireOp",EDGE,"E7.3.10.0");var subQ1=sQuery(id+"F0.wireOp",EDGE,"E2.3");var subQ2=makeQuery(id+"F0.imprint","INTERSECT",VERTEX,{"derivedFrom":[subQ1,subQ0]});Q231=makeQuery(id+"F0.imprint","IMPRINT",FACE,{"disambiguationData":[TD([[makeQuery(id+"F0.imprint","IMPRINT",EDGE,{"disambiguationData":[TD([[subQ2,-1.0]])],"derivedFrom":subQ1}),1.0]])]});}
            var Q232;
            {var subQ0=sQuery(id+"F0.wireOp",EDGE,"E8.5.21.0");var subQ1=sQuery(id+"F0.wireOp",EDGE,"E1");var subQ2=makeQuery(id+"F0.imprint","INTERSECT",VERTEX,{"derivedFrom":[subQ1,subQ0]});Q232=makeQuery(id+"F0.imprint","IMPRINT",FACE,{"disambiguationData":[TD([[makeQuery(id+"F0.imprint","IMPRINT",EDGE,{"disambiguationData":[TD([[subQ2,-1.0]])],"derivedFrom":subQ1}),1.0]])]});}
            var Q233;
            {var subQ0=sQuery(id+"F0.wireOp",EDGE,"E7.5.10.0");var subQ1=sQuery(id+"F0.wireOp",EDGE,"E2.4");var subQ2=makeQuery(id+"F0.imprint","INTERSECT",VERTEX,{"derivedFrom":[subQ1,subQ0]});Q233=makeQuery(id+"F0.imprint","IMPRINT",FACE,{"disambiguationData":[TD([[makeQuery(id+"F0.imprint","IMPRINT",EDGE,{"disambiguationData":[TD([[subQ2,-1.0]])],"derivedFrom":subQ1}),-1.0]])]});}
            var Q234;
            {var subQ0=sQuery(id+"F0.wireOp",EDGE,"E9.3.27.0");var subQ1=sQuery(id+"F0.wireOp",EDGE,"E2.0");var subQ2=makeQuery(id+"F0.imprint","INTERSECT",VERTEX,{"derivedFrom":[subQ1,subQ0]});Q234=makeQuery(id+"F0.imprint","IMPRINT",FACE,{"disambiguationData":[TD([[makeQuery(id+"F0.imprint","IMPRINT",EDGE,{"disambiguationData":[TD([[subQ2,-1.0]])],"derivedFrom":subQ1}),-1.0]])]});}
            var Q235;
            {var subQ0=sQuery(id+"F0.wireOp",EDGE,"E7.3.10.0");var subQ1=sQuery(id+"F0.wireOp",EDGE,"E2.3");var subQ2=makeQuery(id+"F0.imprint","INTERSECT",VERTEX,{"derivedFrom":[subQ1,subQ0]});Q235=makeQuery(id+"F0.imprint","IMPRINT",FACE,{"disambiguationData":[TD([[makeQuery(id+"F0.imprint","IMPRINT",EDGE,{"disambiguationData":[TD([[subQ2,-1.0]])],"derivedFrom":subQ1}),-1.0]])]});}
            var Q236;
            {var subQ0=sQuery(id+"F0.wireOp",EDGE,"E7.3.8.0");var subQ1=sQuery(id+"F0.wireOp",EDGE,"E2.4");var subQ2=makeQuery(id+"F0.imprint","INTERSECT",VERTEX,{"derivedFrom":[subQ1,subQ0]});Q236=makeQuery(id+"F0.imprint","IMPRINT",FACE,{"disambiguationData":[TD([[makeQuery(id+"F0.imprint","IMPRINT",EDGE,{"disambiguationData":[TD([[subQ2,-1.0]])],"derivedFrom":subQ1}),1.0]])]});}
            var Q237;
            {var subQ0=sQuery(id+"F0.wireOp",EDGE,"E8.3.22.0");var subQ1=sQuery(id+"F0.wireOp",EDGE,"E1");var subQ2=makeQuery(id+"F0.imprint","INTERSECT",VERTEX,{"derivedFrom":[subQ1,subQ0]});Q237=makeQuery(id+"F0.imprint","IMPRINT",FACE,{"disambiguationData":[TD([[makeQuery(id+"F0.imprint","IMPRINT",EDGE,{"disambiguationData":[TD([[subQ2,1.0]])],"derivedFrom":subQ1}),1.0]])]});}
            var Q238;
            {var subQ0=sQuery(id+"F0.wireOp",EDGE,"E8.5.22.0");var subQ1=sQuery(id+"F0.wireOp",EDGE,"E1");var subQ2=makeQuery(id+"F0.imprint","INTERSECT",VERTEX,{"derivedFrom":[subQ1,subQ0]});Q238=makeQuery(id+"F0.imprint","IMPRINT",FACE,{"disambiguationData":[TD([[makeQuery(id+"F0.imprint","IMPRINT",EDGE,{"disambiguationData":[TD([[subQ2,-1.0]])],"derivedFrom":subQ1}),1.0]])]});}
            var Q239;
            {var subQ0=sQuery(id+"F0.wireOp",EDGE,"E7.5.10.0");var subQ3=sQuery(id+"F0.wireOp",EDGE,"E7.3.9.0");var subQ4=makeQuery(id+"F0.imprint","INTERSECT",VERTEX,{"derivedFrom":[subQ3,subQ0]});Q239=makeQuery(id+"F0.imprint","IMPRINT",FACE,{"disambiguationData":[TD([[makeQuery(id+"F0.imprint","IMPRINT",EDGE,{"disambiguationData":[TD([[subQ4,-1.0]])],"derivedFrom":subQ3}),-1.0]])]});}
            var Q240;
            {var subQ0=sQuery(id+"F0.wireOp",EDGE,"E7.3.7.0");var subQ1=sQuery(id+"F0.wireOp",EDGE,"E1");var subQ2=makeQuery(id+"F0.imprint","INTERSECT",VERTEX,{"derivedFrom":[subQ1,subQ0]});Q240=makeQuery(id+"F0.imprint","IMPRINT",FACE,{"disambiguationData":[TD([[makeQuery(id+"F0.imprint","IMPRINT",EDGE,{"disambiguationData":[TD([[subQ2,-1.0]])],"derivedFrom":subQ1}),1.0]])]});}
            var Q241;
            {var subQ0=sQuery(id+"F0.wireOp",EDGE,"E7.3.8.0");var subQ1=sQuery(id+"F0.wireOp",EDGE,"E2.4");var subQ2=makeQuery(id+"F0.imprint","INTERSECT",VERTEX,{"derivedFrom":[subQ1,subQ0]});Q241=makeQuery(id+"F0.imprint","IMPRINT",FACE,{"disambiguationData":[TD([[makeQuery(id+"F0.imprint","IMPRINT",EDGE,{"disambiguationData":[TD([[subQ2,-1.0]])],"derivedFrom":subQ1}),-1.0]])]});}
            var Q242;
            {var subQ1=sQuery(id+"F0.wireOp",EDGE,"E1");var subQ3=sQuery(id+"F0.wireOp",EDGE,"E9.3.24.0");var subQ4=makeQuery(id+"F0.imprint","INTERSECT",VERTEX,{"derivedFrom":[subQ1,subQ3]});Q242=makeQuery(id+"F0.imprint","IMPRINT",FACE,{"disambiguationData":[TD([[makeQuery(id+"F0.imprint","IMPRINT",EDGE,{"disambiguationData":[TD([[subQ4,-1.0]])],"derivedFrom":subQ3}),-1.0]])]});}
            var Q243;
            {var subQ0=sQuery(id+"F0.wireOp",EDGE,"E7.5.6.0");var subQ1=sQuery(id+"F0.wireOp",EDGE,"E6.3.1");var subQ2=makeQuery(id+"F0.imprint","INTERSECT",VERTEX,{"derivedFrom":[subQ1,subQ0]});Q243=makeQuery(id+"F0.imprint","IMPRINT",FACE,{"disambiguationData":[TD([[makeQuery(id+"F0.imprint","IMPRINT",EDGE,{"disambiguationData":[TD([[subQ2,-1.0]])],"derivedFrom":subQ1}),-1.0]])]});}
            var Q244;
            {var subQ0=sQuery(id+"F0.wireOp",EDGE,"E9.5.24.0");var subQ1=sQuery(id+"F0.wireOp",EDGE,"E8.3.21.0");var subQ2=makeQuery(id+"F0.imprint","INTERSECT",VERTEX,{"derivedFrom":[subQ1,subQ0]});Q244=makeQuery(id+"F0.imprint","IMPRINT",FACE,{"disambiguationData":[TD([[makeQuery(id+"F0.imprint","IMPRINT",EDGE,{"disambiguationData":[TD([[subQ2,-1.0]])],"derivedFrom":subQ1}),-1.0]])]});}
            var Q245;
            {var subQ0=sQuery(id+"F0.wireOp",EDGE,"E8.5.21.0");var subQ1=sQuery(id+"F0.wireOp",EDGE,"E8.3.18.0");var subQ2=makeQuery(id+"F0.imprint","INTERSECT",VERTEX,{"derivedFrom":[subQ1,subQ0]});Q245=makeQuery(id+"F0.imprint","IMPRINT",FACE,{"disambiguationData":[TD([[makeQuery(id+"F0.imprint","IMPRINT",EDGE,{"disambiguationData":[TD([[subQ2,-1.0]])],"derivedFrom":subQ1}),-1.0]])]});}
            var Q246;
            {var subQ0=sQuery(id+"F0.wireOp",EDGE,"E9.3.27.0");var subQ1=sQuery(id+"F0.wireOp",EDGE,"E1");var subQ2=makeQuery(id+"F0.imprint","INTERSECT",VERTEX,{"derivedFrom":[subQ1,subQ0]});Q246=makeQuery(id+"F0.imprint","IMPRINT",FACE,{"disambiguationData":[TD([[makeQuery(id+"F0.imprint","IMPRINT",EDGE,{"disambiguationData":[TD([[subQ2,-1.0]])],"derivedFrom":subQ1}),1.0]])]});}
            var Q247;
            {var subQ1=sQuery(id+"F0.wireOp",EDGE,"E1");var subQ3=sQuery(id+"F0.wireOp",EDGE,"E5");var subQ4=makeQuery(id+"F0.imprint","INTERSECT",VERTEX,{"derivedFrom":[subQ1,subQ3]});Q247=makeQuery(id+"F0.imprint","IMPRINT",FACE,{"disambiguationData":[TD([[makeQuery(id+"F0.imprint","IMPRINT",EDGE,{"disambiguationData":[TD([[subQ4,-1.0]])],"derivedFrom":subQ3}),1.0]])]});}
            var Q248;
            {var subQ0=sQuery(id+"F0.wireOp",EDGE,"E9.3.28.0");var subQ1=sQuery(id+"F0.wireOp",EDGE,"E1");var subQ2=makeQuery(id+"F0.imprint","INTERSECT",VERTEX,{"derivedFrom":[subQ1,subQ0]});Q248=makeQuery(id+"F0.imprint","IMPRINT",FACE,{"disambiguationData":[TD([[makeQuery(id+"F0.imprint","IMPRINT",EDGE,{"disambiguationData":[TD([[subQ2,-1.0]])],"derivedFrom":subQ1}),1.0]])]});}
            var Q249;
            {var subQ0=sQuery(id+"F0.wireOp",EDGE,"E8.3.13.0");var subQ1=sQuery(id+"F0.wireOp",EDGE,"E2.3");var subQ2=makeQuery(id+"F0.imprint","INTERSECT",VERTEX,{"derivedFrom":[subQ1,subQ0]});Q249=makeQuery(id+"F0.imprint","IMPRINT",FACE,{"disambiguationData":[TD([[makeQuery(id+"F0.imprint","IMPRINT",EDGE,{"disambiguationData":[TD([[subQ2,-1.0]])],"derivedFrom":subQ1}),1.0]])]});}
            var Q250;
            {var subQ0=sQuery(id+"F0.wireOp",EDGE,"E6.4.1");var subQ1=sQuery(id+"F0.wireOp",EDGE,"E1");var subQ2=makeQuery(id+"F0.imprint","INTERSECT",VERTEX,{"derivedFrom":[subQ1,subQ0]});Q250=makeQuery(id+"F0.imprint","IMPRINT",FACE,{"disambiguationData":[TD([[makeQuery(id+"F0.imprint","IMPRINT",EDGE,{"disambiguationData":[TD([[subQ2,-1.0]])],"derivedFrom":subQ1}),1.0]])]});}
            var Q251;
            {var subQ0=sQuery(id+"F0.wireOp",EDGE,"E7.5.9.0");var subQ1=sQuery(id+"F0.wireOp",EDGE,"E7.3.6.0");var subQ2=makeQuery(id+"F0.imprint","INTERSECT",VERTEX,{"derivedFrom":[subQ1,subQ0]});Q251=makeQuery(id+"F0.imprint","IMPRINT",FACE,{"disambiguationData":[TD([[makeQuery(id+"F0.imprint","IMPRINT",EDGE,{"disambiguationData":[TD([[subQ2,-1.0]])],"derivedFrom":subQ1}),-1.0]])]});}
            var Q252;
            {var subQ0=sQuery(id+"F0.wireOp",EDGE,"E9.3.29.0");var subQ1=sQuery(id+"F0.wireOp",EDGE,"E1");var subQ2=makeQuery(id+"F0.imprint","INTERSECT",VERTEX,{"derivedFrom":[subQ1,subQ0]});Q252=makeQuery(id+"F0.imprint","IMPRINT",FACE,{"disambiguationData":[TD([[makeQuery(id+"F0.imprint","IMPRINT",EDGE,{"disambiguationData":[TD([[subQ2,-1.0]])],"derivedFrom":subQ1}),1.0]])]});}
            var Q253;
            {var subQ0=sQuery(id+"F0.wireOp",EDGE,"E7.3.9.0");var subQ1=sQuery(id+"F0.wireOp",EDGE,"E1");var subQ2=makeQuery(id+"F0.imprint","INTERSECT",VERTEX,{"derivedFrom":[subQ1,subQ0]});Q253=makeQuery(id+"F0.imprint","IMPRINT",FACE,{"disambiguationData":[TD([[makeQuery(id+"F0.imprint","IMPRINT",EDGE,{"disambiguationData":[TD([[subQ2,-1.0]])],"derivedFrom":subQ1}),1.0]])]});}
            var Q254;
            {var subQ0=sQuery(id+"F0.wireOp",EDGE,"E9.5.25.0");var subQ1=sQuery(id+"F0.wireOp",EDGE,"E8.3.22.0");var subQ2=makeQuery(id+"F0.imprint","INTERSECT",VERTEX,{"derivedFrom":[subQ1,subQ0]});Q254=makeQuery(id+"F0.imprint","IMPRINT",FACE,{"disambiguationData":[TD([[makeQuery(id+"F0.imprint","IMPRINT",EDGE,{"disambiguationData":[TD([[subQ2,-1.0]])],"derivedFrom":subQ1}),-1.0]])]});}
            var Q255;
            {var subQ0=sQuery(id+"F0.wireOp",EDGE,"E6.2.1");var subQ1=sQuery(id+"F0.wireOp",EDGE,"E1");var subQ2=makeQuery(id+"F0.imprint","INTERSECT",VERTEX,{"derivedFrom":[subQ1,subQ0]});Q255=makeQuery(id+"F0.imprint","IMPRINT",FACE,{"disambiguationData":[TD([[makeQuery(id+"F0.imprint","IMPRINT",EDGE,{"disambiguationData":[TD([[subQ2,-1.0]])],"derivedFrom":subQ1}),1.0]])]});}
            var Q256;
            {var subQ0=sQuery(id+"F0.wireOp",EDGE,"E6.3.1");var subQ1=sQuery(id+"F0.wireOp",EDGE,"E1");var subQ2=makeQuery(id+"F0.imprint","INTERSECT",VERTEX,{"derivedFrom":[subQ1,subQ0]});Q256=makeQuery(id+"F0.imprint","IMPRINT",FACE,{"disambiguationData":[TD([[makeQuery(id+"F0.imprint","IMPRINT",EDGE,{"disambiguationData":[TD([[subQ2,-1.0]])],"derivedFrom":subQ1}),1.0]])]});}
            var Q257;
            {var subQ0=sQuery(id+"F0.wireOp",EDGE,"E8.5.20.0");var subQ1=sQuery(id+"F0.wireOp",EDGE,"E1");var subQ2=makeQuery(id+"F0.imprint","INTERSECT",VERTEX,{"derivedFrom":[subQ1,subQ0]});Q257=makeQuery(id+"F0.imprint","IMPRINT",FACE,{"disambiguationData":[TD([[makeQuery(id+"F0.imprint","IMPRINT",EDGE,{"disambiguationData":[TD([[subQ2,-1.0]])],"derivedFrom":subQ1}),1.0]])]});}
            var Q258;
            {var subQ0=sQuery(id+"F0.wireOp",EDGE,"E8.5.13.0");var subQ1=sQuery(id+"F0.wireOp",EDGE,"E7.3.10.0");var subQ2=makeQuery(id+"F0.imprint","INTERSECT",VERTEX,{"derivedFrom":[subQ1,subQ0]});Q258=makeQuery(id+"F0.imprint","IMPRINT",FACE,{"disambiguationData":[TD([[makeQuery(id+"F0.imprint","IMPRINT",EDGE,{"disambiguationData":[TD([[subQ2,-1.0]])],"derivedFrom":subQ1}),-1.0]])]});}
            var Q259;
            {var subQ0=sQuery(id+"F0.wireOp",EDGE,"E8.5.16.0");var subQ1=sQuery(id+"F0.wireOp",EDGE,"E8.3.13.0");var subQ2=makeQuery(id+"F0.imprint","INTERSECT",VERTEX,{"derivedFrom":[subQ1,subQ0]});Q259=makeQuery(id+"F0.imprint","IMPRINT",FACE,{"disambiguationData":[TD([[makeQuery(id+"F0.imprint","IMPRINT",EDGE,{"disambiguationData":[TD([[subQ2,-1.0]])],"derivedFrom":subQ1}),-1.0]])]});}
            var Q260;
            {var subQ1=sQuery(id+"F0.wireOp",EDGE,"E1");var subQ3=sQuery(id+"F0.wireOp",EDGE,"E6.5.0");var subQ4=makeQuery(id+"F0.imprint","INTERSECT",VERTEX,{"derivedFrom":[subQ1,subQ3]});Q260=makeQuery(id+"F0.imprint","IMPRINT",FACE,{"disambiguationData":[TD([[makeQuery(id+"F0.imprint","IMPRINT",EDGE,{"disambiguationData":[TD([[subQ4,-1.0]])],"derivedFrom":subQ3}),-1.0]])]});}
            var Q261;
            {var subQ0=sQuery(id+"F0.wireOp",EDGE,"E9.3.29.0");var subQ1=sQuery(id+"F0.wireOp",EDGE,"E6.1.0");var subQ2=makeQuery(id+"F0.imprint","INTERSECT",VERTEX,{"derivedFrom":[subQ1,subQ0]});Q261=makeQuery(id+"F0.imprint","IMPRINT",FACE,{"disambiguationData":[TD([[makeQuery(id+"F0.imprint","IMPRINT",EDGE,{"disambiguationData":[TD([[subQ2,-1.0]])],"derivedFrom":subQ1}),-1.0]])]});}
            var Q262;
            {var subQ0=sQuery(id+"F0.wireOp",EDGE,"E8.3.18.0");var subQ1=sQuery(id+"F0.wireOp",EDGE,"E2.2");var subQ2=makeQuery(id+"F0.imprint","INTERSECT",VERTEX,{"derivedFrom":[subQ1,subQ0]});Q262=makeQuery(id+"F0.imprint","IMPRINT",FACE,{"disambiguationData":[TD([[makeQuery(id+"F0.imprint","IMPRINT",EDGE,{"disambiguationData":[TD([[subQ2,-1.0]])],"derivedFrom":subQ1}),1.0]])]});}
            var Q263;
            {var subQ0=sQuery(id+"F0.wireOp",EDGE,"E8.5.23.0");var subQ1=sQuery(id+"F0.wireOp",EDGE,"E8.3.20.0");var subQ2=makeQuery(id+"F0.imprint","INTERSECT",VERTEX,{"derivedFrom":[subQ1,subQ0]});Q263=makeQuery(id+"F0.imprint","IMPRINT",FACE,{"disambiguationData":[TD([[makeQuery(id+"F0.imprint","IMPRINT",EDGE,{"disambiguationData":[TD([[subQ2,-1.0]])],"derivedFrom":subQ1}),-1.0]])]});}
            var Q264;
            {var subQ0=sQuery(id+"F0.wireOp",EDGE,"E8.3.22.0");var subQ1=sQuery(id+"F0.wireOp",EDGE,"E1");var subQ2=makeQuery(id+"F0.imprint","INTERSECT",VERTEX,{"derivedFrom":[subQ1,subQ0]});Q264=makeQuery(id+"F0.imprint","IMPRINT",FACE,{"disambiguationData":[TD([[makeQuery(id+"F0.imprint","IMPRINT",EDGE,{"disambiguationData":[TD([[subQ2,1.0]])],"derivedFrom":subQ1}),-1.0]])]});}
            var Q265;
            {var subQ0=sQuery(id+"F0.wireOp",EDGE,"E6.2.0");var subQ1=sQuery(id+"F0.wireOp",EDGE,"E5");var subQ2=makeQuery(id+"F0.imprint","INTERSECT",VERTEX,{"derivedFrom":[subQ1,subQ0]});Q265=makeQuery(id+"F0.imprint","IMPRINT",FACE,{"disambiguationData":[TD([[makeQuery(id+"F0.imprint","IMPRINT",EDGE,{"disambiguationData":[TD([[subQ2,-1.0]])],"derivedFrom":subQ1}),1.0]])]});}
            var Q266;
            {var subQ0=sQuery(id+"F0.wireOp",EDGE,"E9.5.28.0");var subQ1=sQuery(id+"F0.wireOp",EDGE,"E9.3.25.0");var subQ2=makeQuery(id+"F0.imprint","INTERSECT",VERTEX,{"derivedFrom":[subQ1,subQ0]});Q266=makeQuery(id+"F0.imprint","IMPRINT",FACE,{"disambiguationData":[TD([[makeQuery(id+"F0.imprint","IMPRINT",EDGE,{"disambiguationData":[TD([[subQ2,-1.0]])],"derivedFrom":subQ1}),-1.0]])]});}
            var Q267;
            {var subQ0=sQuery(id+"F0.wireOp",EDGE,"E5");var subQ1=sQuery(id+"F0.wireOp",EDGE,"E2.5");var subQ2=makeQuery(id+"F0.imprint","INTERSECT",VERTEX,{"derivedFrom":[subQ1,subQ0]});Q267=makeQuery(id+"F0.imprint","IMPRINT",FACE,{"disambiguationData":[TD([[makeQuery(id+"F0.imprint","IMPRINT",EDGE,{"disambiguationData":[TD([[subQ2,-1.0]])],"derivedFrom":subQ1}),1.0]])]});}
            var Q268;
            {var subQ1=sQuery(id+"F0.wireOp",EDGE,"E1");var subQ3=sQuery(id+"F0.wireOp",EDGE,"E8.3.19.0");var subQ4=makeQuery(id+"F0.imprint","INTERSECT",VERTEX,{"derivedFrom":[subQ1,subQ3]});Q268=makeQuery(id+"F0.imprint","IMPRINT",FACE,{"disambiguationData":[TD([[makeQuery(id+"F0.imprint","IMPRINT",EDGE,{"disambiguationData":[TD([[subQ4,-1.0]])],"derivedFrom":subQ3}),-1.0]])]});}
            var Q269;
            {var subQ0=sQuery(id+"F0.wireOp",EDGE,"E9.5.26.0");var subQ1=sQuery(id+"F0.wireOp",EDGE,"E8.3.23.0");var subQ2=makeQuery(id+"F0.imprint","INTERSECT",VERTEX,{"derivedFrom":[subQ1,subQ0]});Q269=makeQuery(id+"F0.imprint","IMPRINT",FACE,{"disambiguationData":[TD([[makeQuery(id+"F0.imprint","IMPRINT",EDGE,{"disambiguationData":[TD([[subQ2,-1.0]])],"derivedFrom":subQ1}),-1.0]])]});}
            var Q270;
            {var subQ0=sQuery(id+"F0.wireOp",EDGE,"E9.5.27.0");var subQ1=sQuery(id+"F0.wireOp",EDGE,"E9.3.24.0");var subQ2=makeQuery(id+"F0.imprint","INTERSECT",VERTEX,{"derivedFrom":[subQ1,subQ0]});Q270=makeQuery(id+"F0.imprint","IMPRINT",FACE,{"disambiguationData":[TD([[makeQuery(id+"F0.imprint","IMPRINT",EDGE,{"disambiguationData":[TD([[subQ2,-1.0]])],"derivedFrom":subQ1}),-1.0]])]});}
            var Q271;
            {var subQ0=sQuery(id+"F0.wireOp",EDGE,"E5");var subQ1=sQuery(id+"F0.wireOp",EDGE,"E1");var subQ2=makeQuery(id+"F0.imprint","INTERSECT",VERTEX,{"derivedFrom":[subQ1,subQ0]});Q271=makeQuery(id+"F0.imprint","IMPRINT",FACE,{"disambiguationData":[TD([[makeQuery(id+"F0.imprint","IMPRINT",EDGE,{"disambiguationData":[TD([[subQ2,-1.0]])],"derivedFrom":subQ1}),1.0]])]});}
            var Q272;
            {var subQ0=sQuery(id+"F0.wireOp",EDGE,"E9.3.27.0");var subQ1=sQuery(id+"F0.wireOp",EDGE,"E4");var subQ2=makeQuery(id+"F0.imprint","INTERSECT",VERTEX,{"derivedFrom":[subQ1,subQ0]});Q272=makeQuery(id+"F0.imprint","IMPRINT",FACE,{"disambiguationData":[TD([[makeQuery(id+"F0.imprint","IMPRINT",EDGE,{"disambiguationData":[TD([[subQ2,-1.0]])],"derivedFrom":subQ1}),1.0]])]});}
            var Q273;
            {var subQ0=sQuery(id+"F0.wireOp",EDGE,"E8.5.12.0");var subQ1=sQuery(id+"F0.wireOp",EDGE,"E7.3.9.0");var subQ2=makeQuery(id+"F0.imprint","INTERSECT",VERTEX,{"derivedFrom":[subQ1,subQ0]});Q273=makeQuery(id+"F0.imprint","IMPRINT",FACE,{"disambiguationData":[TD([[makeQuery(id+"F0.imprint","IMPRINT",EDGE,{"disambiguationData":[TD([[subQ2,-1.0]])],"derivedFrom":subQ1}),-1.0]])]});}
            var Q274;
            {var subQ0=sQuery(id+"F0.wireOp",EDGE,"E7.5.11.0");var subQ1=sQuery(id+"F0.wireOp",EDGE,"E7.3.8.0");var subQ2=makeQuery(id+"F0.imprint","INTERSECT",VERTEX,{"derivedFrom":[subQ1,subQ0]});Q274=makeQuery(id+"F0.imprint","IMPRINT",FACE,{"disambiguationData":[TD([[makeQuery(id+"F0.imprint","IMPRINT",EDGE,{"disambiguationData":[TD([[subQ2,-1.0]])],"derivedFrom":subQ1}),-1.0]])]});}
            var Q275;
            {var subQ0=sQuery(id+"F0.wireOp",EDGE,"E8.5.18.0");var subQ1=sQuery(id+"F0.wireOp",EDGE,"E8.3.14.0");var subQ2=makeQuery(id+"F0.imprint","INTERSECT",VERTEX,{"derivedFrom":[subQ1,subQ0]});Q275=makeQuery(id+"F0.imprint","IMPRINT",FACE,{"disambiguationData":[TD([[makeQuery(id+"F0.imprint","IMPRINT",EDGE,{"disambiguationData":[TD([[subQ2,-1.0]])],"derivedFrom":subQ1}),-1.0]])]});}
            var Q276;
            {var subQ0=sQuery(id+"F0.wireOp",EDGE,"E8.5.16.0");var subQ1=sQuery(id+"F0.wireOp",EDGE,"E8.3.12.0");var subQ2=makeQuery(id+"F0.imprint","INTERSECT",VERTEX,{"derivedFrom":[subQ1,subQ0]});Q276=makeQuery(id+"F0.imprint","IMPRINT",FACE,{"disambiguationData":[TD([[makeQuery(id+"F0.imprint","IMPRINT",EDGE,{"disambiguationData":[TD([[subQ2,-1.0]])],"derivedFrom":subQ1}),-1.0]])]});}
            var Q277;
            {var subQ0=sQuery(id+"F0.wireOp",EDGE,"E8.5.13.0");var subQ1=sQuery(id+"F0.wireOp",EDGE,"E7.3.9.0");var subQ2=makeQuery(id+"F0.imprint","INTERSECT",VERTEX,{"derivedFrom":[subQ1,subQ0]});Q277=makeQuery(id+"F0.imprint","IMPRINT",FACE,{"disambiguationData":[TD([[makeQuery(id+"F0.imprint","IMPRINT",EDGE,{"disambiguationData":[TD([[subQ2,-1.0]])],"derivedFrom":subQ1}),-1.0]])]});}
            var Q278;
            {var subQ0=sQuery(id+"F0.wireOp",EDGE,"E8.5.12.0");var subQ1=sQuery(id+"F0.wireOp",EDGE,"E7.3.8.0");var subQ2=makeQuery(id+"F0.imprint","INTERSECT",VERTEX,{"derivedFrom":[subQ1,subQ0]});Q278=makeQuery(id+"F0.imprint","IMPRINT",FACE,{"disambiguationData":[TD([[makeQuery(id+"F0.imprint","IMPRINT",EDGE,{"disambiguationData":[TD([[subQ2,-1.0]])],"derivedFrom":subQ1}),-1.0]])]});}
            var Q279;
            {var subQ0=sQuery(id+"F0.wireOp",EDGE,"E8.5.15.0");var subQ1=sQuery(id+"F0.wireOp",EDGE,"E7.3.11.0");var subQ2=makeQuery(id+"F0.imprint","INTERSECT",VERTEX,{"derivedFrom":[subQ1,subQ0]});Q279=makeQuery(id+"F0.imprint","IMPRINT",FACE,{"disambiguationData":[TD([[makeQuery(id+"F0.imprint","IMPRINT",EDGE,{"disambiguationData":[TD([[subQ2,-1.0]])],"derivedFrom":subQ1}),-1.0]])]});}
            var Q280;
            {var subQ0=sQuery(id+"F0.wireOp",EDGE,"E8.5.17.0");var subQ1=sQuery(id+"F0.wireOp",EDGE,"E8.3.13.0");var subQ2=makeQuery(id+"F0.imprint","INTERSECT",VERTEX,{"derivedFrom":[subQ1,subQ0]});Q280=makeQuery(id+"F0.imprint","IMPRINT",FACE,{"disambiguationData":[TD([[makeQuery(id+"F0.imprint","IMPRINT",EDGE,{"disambiguationData":[TD([[subQ2,-1.0]])],"derivedFrom":subQ1}),-1.0]])]});}
            var Q281;
            {var subQ0=sQuery(id+"F0.wireOp",EDGE,"E8.5.16.0");var subQ1=sQuery(id+"F0.wireOp",EDGE,"E7.3.11.0");var subQ2=makeQuery(id+"F0.imprint","INTERSECT",VERTEX,{"derivedFrom":[subQ1,subQ0]});Q281=makeQuery(id+"F0.imprint","IMPRINT",FACE,{"disambiguationData":[TD([[makeQuery(id+"F0.imprint","IMPRINT",EDGE,{"disambiguationData":[TD([[subQ2,-1.0]])],"derivedFrom":subQ1}),-1.0]])]});}
            var Q282;
            {var subQ0=sQuery(id+"F0.wireOp",EDGE,"E8.5.22.0");var subQ1=sQuery(id+"F0.wireOp",EDGE,"E8.3.18.0");var subQ2=makeQuery(id+"F0.imprint","INTERSECT",VERTEX,{"derivedFrom":[subQ1,subQ0]});Q282=makeQuery(id+"F0.imprint","IMPRINT",FACE,{"disambiguationData":[TD([[makeQuery(id+"F0.imprint","IMPRINT",EDGE,{"disambiguationData":[TD([[subQ2,-1.0]])],"derivedFrom":subQ1}),-1.0]])]});}
            var Q283;
            {var subQ0=sQuery(id+"F0.wireOp",EDGE,"E8.5.19.0");var subQ1=sQuery(id+"F0.wireOp",EDGE,"E8.3.15.0");var subQ2=makeQuery(id+"F0.imprint","INTERSECT",VERTEX,{"derivedFrom":[subQ1,subQ0]});Q283=makeQuery(id+"F0.imprint","IMPRINT",FACE,{"disambiguationData":[TD([[makeQuery(id+"F0.imprint","IMPRINT",EDGE,{"disambiguationData":[TD([[subQ2,-1.0]])],"derivedFrom":subQ1}),-1.0]])]});}
            var Q284;
            {var subQ0=sQuery(id+"F0.wireOp",EDGE,"E9.5.26.0");var subQ1=sQuery(id+"F0.wireOp",EDGE,"E8.3.22.0");var subQ2=makeQuery(id+"F0.imprint","INTERSECT",VERTEX,{"derivedFrom":[subQ1,subQ0]});Q284=makeQuery(id+"F0.imprint","IMPRINT",FACE,{"disambiguationData":[TD([[makeQuery(id+"F0.imprint","IMPRINT",EDGE,{"disambiguationData":[TD([[subQ2,-1.0]])],"derivedFrom":subQ1}),-1.0]])]});}
            var Q285;
            {var subQ0=sQuery(id+"F0.wireOp",EDGE,"E9.5.24.0");var subQ1=sQuery(id+"F0.wireOp",EDGE,"E8.3.20.0");var subQ2=makeQuery(id+"F0.imprint","INTERSECT",VERTEX,{"derivedFrom":[subQ1,subQ0]});Q285=makeQuery(id+"F0.imprint","IMPRINT",FACE,{"disambiguationData":[TD([[makeQuery(id+"F0.imprint","IMPRINT",EDGE,{"disambiguationData":[TD([[subQ2,-1.0]])],"derivedFrom":subQ1}),-1.0]])]});}
            var Q286;
            {var subQ0=sQuery(id+"F0.wireOp",EDGE,"E8.5.23.0");var subQ1=sQuery(id+"F0.wireOp",EDGE,"E8.3.19.0");var subQ2=makeQuery(id+"F0.imprint","INTERSECT",VERTEX,{"derivedFrom":[subQ1,subQ0]});Q286=makeQuery(id+"F0.imprint","IMPRINT",FACE,{"disambiguationData":[TD([[makeQuery(id+"F0.imprint","IMPRINT",EDGE,{"disambiguationData":[TD([[subQ2,-1.0]])],"derivedFrom":subQ1}),-1.0]])]});}
            var Q287;
            {var subQ0=sQuery(id+"F0.wireOp",EDGE,"E8.5.20.0");var subQ1=sQuery(id+"F0.wireOp",EDGE,"E8.3.16.0");var subQ2=makeQuery(id+"F0.imprint","INTERSECT",VERTEX,{"derivedFrom":[subQ1,subQ0]});Q287=makeQuery(id+"F0.imprint","IMPRINT",FACE,{"disambiguationData":[TD([[makeQuery(id+"F0.imprint","IMPRINT",EDGE,{"disambiguationData":[TD([[subQ2,-1.0]])],"derivedFrom":subQ1}),-1.0]])]});}
            var Q288;
            {var subQ0=sQuery(id+"F0.wireOp",EDGE,"E8.5.14.0");var subQ1=sQuery(id+"F0.wireOp",EDGE,"E7.3.10.0");var subQ2=makeQuery(id+"F0.imprint","INTERSECT",VERTEX,{"derivedFrom":[subQ1,subQ0]});Q288=makeQuery(id+"F0.imprint","IMPRINT",FACE,{"disambiguationData":[TD([[makeQuery(id+"F0.imprint","IMPRINT",EDGE,{"disambiguationData":[TD([[subQ2,-1.0]])],"derivedFrom":subQ1}),-1.0]])]});}
            var Q289;
            {var subQ0=sQuery(id+"F0.wireOp",EDGE,"E9.5.27.0");var subQ1=sQuery(id+"F0.wireOp",EDGE,"E8.3.23.0");var subQ2=makeQuery(id+"F0.imprint","INTERSECT",VERTEX,{"derivedFrom":[subQ1,subQ0]});Q289=makeQuery(id+"F0.imprint","IMPRINT",FACE,{"disambiguationData":[TD([[makeQuery(id+"F0.imprint","IMPRINT",EDGE,{"disambiguationData":[TD([[subQ2,-1.0]])],"derivedFrom":subQ1}),-1.0]])]});}
            var Q290;
            {var subQ0=sQuery(id+"F0.wireOp",EDGE,"E8.5.21.0");var subQ1=sQuery(id+"F0.wireOp",EDGE,"E8.3.17.0");var subQ2=makeQuery(id+"F0.imprint","INTERSECT",VERTEX,{"derivedFrom":[subQ1,subQ0]});Q290=makeQuery(id+"F0.imprint","IMPRINT",FACE,{"disambiguationData":[TD([[makeQuery(id+"F0.imprint","IMPRINT",EDGE,{"disambiguationData":[TD([[subQ2,-1.0]])],"derivedFrom":subQ1}),-1.0]])]});}
            var Q291;
            {var subQ0=sQuery(id+"F0.wireOp",EDGE,"E9.5.24.0");var subQ1=sQuery(id+"F0.wireOp",EDGE,"E8.3.19.0");var subQ2=makeQuery(id+"F0.imprint","INTERSECT",VERTEX,{"derivedFrom":[subQ1,subQ0]});Q291=makeQuery(id+"F0.imprint","IMPRINT",FACE,{"disambiguationData":[TD([[makeQuery(id+"F0.imprint","IMPRINT",EDGE,{"disambiguationData":[TD([[subQ2,-1.0]])],"derivedFrom":subQ1}),-1.0]])]});}
            var Q292;
            {var subQ0=sQuery(id+"F0.wireOp",EDGE,"E8.5.15.0");var subQ1=sQuery(id+"F0.wireOp",EDGE,"E7.3.10.0");var subQ2=makeQuery(id+"F0.imprint","INTERSECT",VERTEX,{"derivedFrom":[subQ1,subQ0]});Q292=makeQuery(id+"F0.imprint","IMPRINT",FACE,{"disambiguationData":[TD([[makeQuery(id+"F0.imprint","IMPRINT",EDGE,{"disambiguationData":[TD([[subQ2,-1.0]])],"derivedFrom":subQ1}),-1.0]])]});}
            var Q293;
            {var subQ0=sQuery(id+"F0.wireOp",EDGE,"E6.5.0");var subQ1=sQuery(id+"F0.wireOp",EDGE,"E6.1.1");var subQ2=makeQuery(id+"F0.imprint","INTERSECT",VERTEX,{"derivedFrom":[subQ1,subQ0]});Q293=makeQuery(id+"F0.imprint","IMPRINT",FACE,{"disambiguationData":[TD([[makeQuery(id+"F0.imprint","IMPRINT",EDGE,{"disambiguationData":[TD([[subQ2,-1.0]])],"derivedFrom":subQ1}),-1.0]])]});}
            var Q294;
            {var subQ0=sQuery(id+"F0.wireOp",EDGE,"E7.5.9.0");var subQ1=sQuery(id+"F0.wireOp",EDGE,"E6.5.1");var subQ2=makeQuery(id+"F0.imprint","INTERSECT",VERTEX,{"derivedFrom":[subQ1,subQ0]});Q294=makeQuery(id+"F0.imprint","IMPRINT",FACE,{"disambiguationData":[TD([[makeQuery(id+"F0.imprint","IMPRINT",EDGE,{"disambiguationData":[TD([[subQ2,-1.0]])],"derivedFrom":subQ1}),-1.0]])]});}
            var Q295;
            {var subQ0=sQuery(id+"F0.wireOp",EDGE,"E8.5.19.0");var subQ1=sQuery(id+"F0.wireOp",EDGE,"E8.3.14.0");var subQ2=makeQuery(id+"F0.imprint","INTERSECT",VERTEX,{"derivedFrom":[subQ1,subQ0]});Q295=makeQuery(id+"F0.imprint","IMPRINT",FACE,{"disambiguationData":[TD([[makeQuery(id+"F0.imprint","IMPRINT",EDGE,{"disambiguationData":[TD([[subQ2,-1.0]])],"derivedFrom":subQ1}),-1.0]])]});}
            var Q296;
            {var subQ0=sQuery(id+"F0.wireOp",EDGE,"E9.5.25.0");var subQ1=sQuery(id+"F0.wireOp",EDGE,"E8.3.20.0");var subQ2=makeQuery(id+"F0.imprint","INTERSECT",VERTEX,{"derivedFrom":[subQ1,subQ0]});Q296=makeQuery(id+"F0.imprint","IMPRINT",FACE,{"disambiguationData":[TD([[makeQuery(id+"F0.imprint","IMPRINT",EDGE,{"disambiguationData":[TD([[subQ2,-1.0]])],"derivedFrom":subQ1}),-1.0]])]});}
            var Q297;
            {var subQ0=sQuery(id+"F0.wireOp",EDGE,"E8.5.22.0");var subQ1=sQuery(id+"F0.wireOp",EDGE,"E8.3.17.0");var subQ2=makeQuery(id+"F0.imprint","INTERSECT",VERTEX,{"derivedFrom":[subQ1,subQ0]});Q297=makeQuery(id+"F0.imprint","IMPRINT",FACE,{"disambiguationData":[TD([[makeQuery(id+"F0.imprint","IMPRINT",EDGE,{"disambiguationData":[TD([[subQ2,-1.0]])],"derivedFrom":subQ1}),-1.0]])]});}
            var Q298;
            {var subQ0=sQuery(id+"F0.wireOp",EDGE,"E8.5.13.0");var subQ1=sQuery(id+"F0.wireOp",EDGE,"E7.3.8.0");var subQ2=makeQuery(id+"F0.imprint","INTERSECT",VERTEX,{"derivedFrom":[subQ1,subQ0]});Q298=makeQuery(id+"F0.imprint","IMPRINT",FACE,{"disambiguationData":[TD([[makeQuery(id+"F0.imprint","IMPRINT",EDGE,{"disambiguationData":[TD([[subQ2,-1.0]])],"derivedFrom":subQ1}),-1.0]])]});}
            var Q299;
            {var subQ0=sQuery(id+"F0.wireOp",EDGE,"E8.5.17.0");var subQ1=sQuery(id+"F0.wireOp",EDGE,"E7.3.11.0");var subQ2=makeQuery(id+"F0.imprint","INTERSECT",VERTEX,{"derivedFrom":[subQ1,subQ0]});Q299=makeQuery(id+"F0.imprint","IMPRINT",FACE,{"disambiguationData":[TD([[makeQuery(id+"F0.imprint","IMPRINT",EDGE,{"disambiguationData":[TD([[subQ2,-1.0]])],"derivedFrom":subQ1}),-1.0]])]});}
            var Q300;
            {var subQ0=sQuery(id+"F0.wireOp",EDGE,"E6.3.0");var subQ1=sQuery(id+"F0.wireOp",EDGE,"E5");var subQ2=makeQuery(id+"F0.imprint","INTERSECT",VERTEX,{"derivedFrom":[subQ1,subQ0]});Q300=makeQuery(id+"F0.imprint","IMPRINT",FACE,{"disambiguationData":[TD([[makeQuery(id+"F0.imprint","IMPRINT",EDGE,{"disambiguationData":[TD([[subQ2,-1.0]])],"derivedFrom":subQ1}),1.0]])]});}
            var Q301;
            {var subQ0=sQuery(id+"F0.wireOp",EDGE,"E7.5.7.0");var subQ1=sQuery(id+"F0.wireOp",EDGE,"E6.3.1");var subQ2=makeQuery(id+"F0.imprint","INTERSECT",VERTEX,{"derivedFrom":[subQ1,subQ0]});Q301=makeQuery(id+"F0.imprint","IMPRINT",FACE,{"disambiguationData":[TD([[makeQuery(id+"F0.imprint","IMPRINT",EDGE,{"disambiguationData":[TD([[subQ2,-1.0]])],"derivedFrom":subQ1}),-1.0]])]});}
            var Q302;
            {var subQ0=sQuery(id+"F0.wireOp",EDGE,"E8.5.12.0");var subQ1=sQuery(id+"F0.wireOp",EDGE,"E6.3.1");var subQ2=makeQuery(id+"F0.imprint","INTERSECT",VERTEX,{"derivedFrom":[subQ1,subQ0]});Q302=makeQuery(id+"F0.imprint","IMPRINT",FACE,{"disambiguationData":[TD([[makeQuery(id+"F0.imprint","IMPRINT",EDGE,{"disambiguationData":[TD([[subQ2,1.0]])],"derivedFrom":subQ1}),-1.0]])]});}
            var Q303;
            {var subQ0=sQuery(id+"F0.wireOp",EDGE,"E8.5.20.0");var subQ1=sQuery(id+"F0.wireOp",EDGE,"E8.3.15.0");var subQ2=makeQuery(id+"F0.imprint","INTERSECT",VERTEX,{"derivedFrom":[subQ1,subQ0]});Q303=makeQuery(id+"F0.imprint","IMPRINT",FACE,{"disambiguationData":[TD([[makeQuery(id+"F0.imprint","IMPRINT",EDGE,{"disambiguationData":[TD([[subQ2,-1.0]])],"derivedFrom":subQ1}),-1.0]])]});}
            var Q304;
            {var subQ0=sQuery(id+"F0.wireOp",EDGE,"E9.5.24.0");var subQ1=sQuery(id+"F0.wireOp",EDGE,"E8.3.18.0");var subQ2=makeQuery(id+"F0.imprint","INTERSECT",VERTEX,{"derivedFrom":[subQ1,subQ0]});Q304=makeQuery(id+"F0.imprint","IMPRINT",FACE,{"disambiguationData":[TD([[makeQuery(id+"F0.imprint","IMPRINT",EDGE,{"disambiguationData":[TD([[subQ2,-1.0]])],"derivedFrom":subQ1}),-1.0]])]});}
            var Q305;
            {var subQ0=sQuery(id+"F0.wireOp",EDGE,"E9.3.29.0");var subQ1=sQuery(id+"F0.wireOp",EDGE,"E7.5.6.0");var subQ2=makeQuery(id+"F0.imprint","INTERSECT",VERTEX,{"derivedFrom":[subQ1,subQ0]});Q305=makeQuery(id+"F0.imprint","IMPRINT",FACE,{"disambiguationData":[TD([[makeQuery(id+"F0.imprint","IMPRINT",EDGE,{"disambiguationData":[TD([[subQ2,-1.0]])],"derivedFrom":subQ1}),-1.0]])]});}
            var Q306;
            {var subQ0=sQuery(id+"F0.wireOp",EDGE,"E9.3.26.0");var subQ1=sQuery(id+"F0.wireOp",EDGE,"E4");var subQ2=makeQuery(id+"F0.imprint","INTERSECT",VERTEX,{"derivedFrom":[subQ1,subQ0]});Q306=makeQuery(id+"F0.imprint","IMPRINT",FACE,{"disambiguationData":[TD([[makeQuery(id+"F0.imprint","IMPRINT",EDGE,{"disambiguationData":[TD([[subQ2,-1.0]])],"derivedFrom":subQ1}),-1.0]])]});}
            var Q307;
            {var subQ0=sQuery(id+"F0.wireOp",EDGE,"E7.5.11.0");var subQ1=sQuery(id+"F0.wireOp",EDGE,"E7.3.7.0");var subQ2=makeQuery(id+"F0.imprint","INTERSECT",VERTEX,{"derivedFrom":[subQ1,subQ0]});Q307=makeQuery(id+"F0.imprint","IMPRINT",FACE,{"disambiguationData":[TD([[makeQuery(id+"F0.imprint","IMPRINT",EDGE,{"disambiguationData":[TD([[subQ2,-1.0]])],"derivedFrom":subQ1}),-1.0]])]});}
            var Q308;
            {var subQ8=sQuery(id+"F0.wireOp",EDGE,"E4");var subQ14=sQuery(id+"F0.wireOp",EDGE,"E8.3.21.0");var subQ15=makeQuery(id+"F0.imprint","INTERSECT",VERTEX,{"derivedFrom":[subQ8,subQ14]});Q308=makeQuery(id+"F0.imprint","IMPRINT",FACE,{"disambiguationData":[TD([[makeQuery(id+"F0.imprint","IMPRINT",EDGE,{"disambiguationData":[TD([[subQ15,1.0]])],"derivedFrom":subQ8}),-1.0]])]});}
            var Q309;
            {var subQ0=sQuery(id+"F0.wireOp",EDGE,"E9.5.28.0");var subQ1=sQuery(id+"F0.wireOp",EDGE,"E8.3.23.0");var subQ2=makeQuery(id+"F0.imprint","INTERSECT",VERTEX,{"derivedFrom":[subQ1,subQ0]});Q309=makeQuery(id+"F0.imprint","IMPRINT",FACE,{"disambiguationData":[TD([[makeQuery(id+"F0.imprint","IMPRINT",EDGE,{"disambiguationData":[TD([[subQ2,-1.0]])],"derivedFrom":subQ1}),-1.0]])]});}
            var Q310;
            {var subQ0=sQuery(id+"F0.wireOp",EDGE,"E8.5.23.0");var subQ1=sQuery(id+"F0.wireOp",EDGE,"E8.3.17.0");var subQ2=makeQuery(id+"F0.imprint","INTERSECT",VERTEX,{"derivedFrom":[subQ1,subQ0]});Q310=makeQuery(id+"F0.imprint","IMPRINT",FACE,{"disambiguationData":[TD([[makeQuery(id+"F0.imprint","IMPRINT",EDGE,{"disambiguationData":[TD([[subQ2,-1.0]])],"derivedFrom":subQ1}),-1.0]])]});}
            var Q311;
            {var subQ0=sQuery(id+"F0.wireOp",EDGE,"E9.5.28.0");var subQ1=sQuery(id+"F0.wireOp",EDGE,"E9.3.24.0");var subQ2=makeQuery(id+"F0.imprint","INTERSECT",VERTEX,{"derivedFrom":[subQ1,subQ0]});Q311=makeQuery(id+"F0.imprint","IMPRINT",FACE,{"disambiguationData":[TD([[makeQuery(id+"F0.imprint","IMPRINT",EDGE,{"disambiguationData":[TD([[subQ2,-1.0]])],"derivedFrom":subQ1}),-1.0]])]});}
            var Q312;
            {var subQ0=sQuery(id+"F0.wireOp",EDGE,"E9.5.25.0");var subQ1=sQuery(id+"F0.wireOp",EDGE,"E8.3.21.0");var subQ2=makeQuery(id+"F0.imprint","INTERSECT",VERTEX,{"derivedFrom":[subQ1,subQ0]});Q312=makeQuery(id+"F0.imprint","IMPRINT",FACE,{"disambiguationData":[TD([[makeQuery(id+"F0.imprint","IMPRINT",EDGE,{"disambiguationData":[TD([[subQ2,-1.0]])],"derivedFrom":subQ1}),-1.0]])]});}
            var Q313;
            {var subQ0=sQuery(id+"F0.wireOp",EDGE,"E9.3.29.0");var subQ1=sQuery(id+"F0.wireOp",EDGE,"E6.2.0");var subQ2=makeQuery(id+"F0.imprint","INTERSECT",VERTEX,{"derivedFrom":[subQ1,subQ0]});Q313=makeQuery(id+"F0.imprint","IMPRINT",FACE,{"disambiguationData":[TD([[makeQuery(id+"F0.imprint","IMPRINT",EDGE,{"disambiguationData":[TD([[subQ2,-1.0]])],"derivedFrom":subQ1}),-1.0]])]});}
            var Q314;
            {var subQ0=sQuery(id+"F0.wireOp",EDGE,"E8.5.13.0");var subQ1=sQuery(id+"F0.wireOp",EDGE,"E6.4.1");var subQ2=makeQuery(id+"F0.imprint","INTERSECT",VERTEX,{"derivedFrom":[subQ1,subQ0]});Q314=makeQuery(id+"F0.imprint","IMPRINT",FACE,{"disambiguationData":[TD([[makeQuery(id+"F0.imprint","IMPRINT",EDGE,{"disambiguationData":[TD([[subQ2,1.0]])],"derivedFrom":subQ1}),-1.0]])]});}
            var Q315;
            {var subQ0=sQuery(id+"F0.wireOp",EDGE,"E7.5.10.0");var subQ1=sQuery(id+"F0.wireOp",EDGE,"E7.3.6.0");var subQ2=makeQuery(id+"F0.imprint","INTERSECT",VERTEX,{"derivedFrom":[subQ1,subQ0]});Q315=makeQuery(id+"F0.imprint","IMPRINT",FACE,{"disambiguationData":[TD([[makeQuery(id+"F0.imprint","IMPRINT",EDGE,{"disambiguationData":[TD([[subQ2,-1.0]])],"derivedFrom":subQ1}),-1.0]])]});}
            var Q316;
            {var subQ0=sQuery(id+"F0.wireOp",EDGE,"E8.5.21.0");var subQ1=sQuery(id+"F0.wireOp",EDGE,"E8.3.15.0");var subQ2=makeQuery(id+"F0.imprint","INTERSECT",VERTEX,{"derivedFrom":[subQ1,subQ0]});Q316=makeQuery(id+"F0.imprint","IMPRINT",FACE,{"disambiguationData":[TD([[makeQuery(id+"F0.imprint","IMPRINT",EDGE,{"disambiguationData":[TD([[subQ2,-1.0]])],"derivedFrom":subQ1}),-1.0]])]});}
            var Q317;
            {var subQ0=sQuery(id+"F0.wireOp",EDGE,"E9.5.25.0");var subQ1=sQuery(id+"F0.wireOp",EDGE,"E8.3.18.0");var subQ2=makeQuery(id+"F0.imprint","INTERSECT",VERTEX,{"derivedFrom":[subQ1,subQ0]});Q317=makeQuery(id+"F0.imprint","IMPRINT",FACE,{"disambiguationData":[TD([[makeQuery(id+"F0.imprint","IMPRINT",EDGE,{"disambiguationData":[TD([[subQ2,-1.0]])],"derivedFrom":subQ1}),-1.0]])]});}
            var Q318;
            {var subQ0=sQuery(id+"F0.wireOp",EDGE,"E7.5.6.0");var subQ1=sQuery(id+"F0.wireOp",EDGE,"E5");var subQ2=makeQuery(id+"F0.imprint","INTERSECT",VERTEX,{"derivedFrom":[subQ1,subQ0]});Q318=makeQuery(id+"F0.imprint","IMPRINT",FACE,{"disambiguationData":[TD([[makeQuery(id+"F0.imprint","IMPRINT",EDGE,{"disambiguationData":[TD([[subQ2,-1.0]])],"derivedFrom":subQ1}),1.0]])]});}
            var Q319;
            {var subQ0=sQuery(id+"F0.wireOp",EDGE,"E7.5.6.0");var subQ1=sQuery(id+"F0.wireOp",EDGE,"E6.2.1");var subQ2=makeQuery(id+"F0.imprint","INTERSECT",VERTEX,{"derivedFrom":[subQ1,subQ0]});Q319=makeQuery(id+"F0.imprint","IMPRINT",FACE,{"disambiguationData":[TD([[makeQuery(id+"F0.imprint","IMPRINT",EDGE,{"disambiguationData":[TD([[subQ2,-1.0]])],"derivedFrom":subQ1}),-1.0]])]});}
            var Q320;
            {var subQ0=sQuery(id+"F0.wireOp",EDGE,"E9.3.26.0");var subQ1=sQuery(id+"F0.wireOp",EDGE,"E4");var subQ2=makeQuery(id+"F0.imprint","INTERSECT",VERTEX,{"derivedFrom":[subQ1,subQ0]});Q320=makeQuery(id+"F0.imprint","IMPRINT",FACE,{"disambiguationData":[TD([[makeQuery(id+"F0.imprint","IMPRINT",EDGE,{"disambiguationData":[TD([[subQ2,-1.0]])],"derivedFrom":subQ1}),1.0]])]});}
            var Q321;
            {var subQ0=sQuery(id+"F0.wireOp",EDGE,"E7.5.8.0");var subQ1=sQuery(id+"F0.wireOp",EDGE,"E6.4.1");var subQ2=makeQuery(id+"F0.imprint","INTERSECT",VERTEX,{"derivedFrom":[subQ1,subQ0]});Q321=makeQuery(id+"F0.imprint","IMPRINT",FACE,{"disambiguationData":[TD([[makeQuery(id+"F0.imprint","IMPRINT",EDGE,{"disambiguationData":[TD([[subQ2,-1.0]])],"derivedFrom":subQ1}),-1.0]])]});}
            var Q322;
            {var subQ0=sQuery(id+"F0.wireOp",EDGE,"E8.5.21.0");var subQ1=sQuery(id+"F0.wireOp",EDGE,"E8.3.16.0");var subQ2=makeQuery(id+"F0.imprint","INTERSECT",VERTEX,{"derivedFrom":[subQ1,subQ0]});Q322=makeQuery(id+"F0.imprint","IMPRINT",FACE,{"disambiguationData":[TD([[makeQuery(id+"F0.imprint","IMPRINT",EDGE,{"disambiguationData":[TD([[subQ2,-1.0]])],"derivedFrom":subQ1}),-1.0]])]});}
            var Q323;
            {var subQ0=sQuery(id+"F0.wireOp",EDGE,"E8.3.21.0");var subQ1=sQuery(id+"F0.wireOp",EDGE,"E4");var subQ2=makeQuery(id+"F0.imprint","INTERSECT",VERTEX,{"derivedFrom":[subQ1,subQ0]});Q323=makeQuery(id+"F0.imprint","IMPRINT",FACE,{"disambiguationData":[TD([[makeQuery(id+"F0.imprint","IMPRINT",EDGE,{"disambiguationData":[TD([[subQ2,1.0]])],"derivedFrom":subQ1}),1.0]])]});}
            var Q324;
            {var subQ0=sQuery(id+"F0.wireOp",EDGE,"E8.5.12.0");var subQ1=sQuery(id+"F0.wireOp",EDGE,"E7.3.7.0");var subQ2=makeQuery(id+"F0.imprint","INTERSECT",VERTEX,{"derivedFrom":[subQ1,subQ0]});Q324=makeQuery(id+"F0.imprint","IMPRINT",FACE,{"disambiguationData":[TD([[makeQuery(id+"F0.imprint","IMPRINT",EDGE,{"disambiguationData":[TD([[subQ2,-1.0]])],"derivedFrom":subQ1}),-1.0]])]});}
            var Q325;
            {var subQ0=sQuery(id+"F0.wireOp",EDGE,"E8.5.18.0");var subQ1=sQuery(id+"F0.wireOp",EDGE,"E8.3.13.0");var subQ2=makeQuery(id+"F0.imprint","INTERSECT",VERTEX,{"derivedFrom":[subQ1,subQ0]});Q325=makeQuery(id+"F0.imprint","IMPRINT",FACE,{"disambiguationData":[TD([[makeQuery(id+"F0.imprint","IMPRINT",EDGE,{"disambiguationData":[TD([[subQ2,-1.0]])],"derivedFrom":subQ1}),-1.0]])]});}
            var Q326;
            {var subQ0=sQuery(id+"F0.wireOp",EDGE,"E8.5.16.0");var subQ1=sQuery(id+"F0.wireOp",EDGE,"E7.3.10.0");var subQ2=makeQuery(id+"F0.imprint","INTERSECT",VERTEX,{"derivedFrom":[subQ1,subQ0]});Q326=makeQuery(id+"F0.imprint","IMPRINT",FACE,{"disambiguationData":[TD([[makeQuery(id+"F0.imprint","IMPRINT",EDGE,{"disambiguationData":[TD([[subQ2,-1.0]])],"derivedFrom":subQ1}),-1.0]])]});}
            var Q327;
            {var subQ0=sQuery(id+"F0.wireOp",EDGE,"E9.3.24.0");var subQ1=sQuery(id+"F0.wireOp",EDGE,"E4");var subQ2=makeQuery(id+"F0.imprint","INTERSECT",VERTEX,{"derivedFrom":[subQ1,subQ0]});Q327=makeQuery(id+"F0.imprint","IMPRINT",FACE,{"disambiguationData":[TD([[makeQuery(id+"F0.imprint","IMPRINT",EDGE,{"disambiguationData":[TD([[subQ2,-1.0]])],"derivedFrom":subQ1}),1.0]])]});}
            var Q328;
            {var subQ0=sQuery(id+"F0.wireOp",EDGE,"E8.3.23.0");var subQ1=sQuery(id+"F0.wireOp",EDGE,"E4");var subQ2=makeQuery(id+"F0.imprint","INTERSECT",VERTEX,{"derivedFrom":[subQ1,subQ0]});Q328=makeQuery(id+"F0.imprint","IMPRINT",FACE,{"disambiguationData":[TD([[makeQuery(id+"F0.imprint","IMPRINT",EDGE,{"disambiguationData":[TD([[subQ2,-1.0]])],"derivedFrom":subQ1}),1.0]])]});}
            var Q329;
            {var subQ0=sQuery(id+"F0.wireOp",EDGE,"E8.5.20.0");var subQ1=sQuery(id+"F0.wireOp",EDGE,"E8.3.14.0");var subQ2=makeQuery(id+"F0.imprint","INTERSECT",VERTEX,{"derivedFrom":[subQ1,subQ0]});Q329=makeQuery(id+"F0.imprint","IMPRINT",FACE,{"disambiguationData":[TD([[makeQuery(id+"F0.imprint","IMPRINT",EDGE,{"disambiguationData":[TD([[subQ2,-1.0]])],"derivedFrom":subQ1}),-1.0]])]});}
            var Q330;
            {var subQ0=sQuery(id+"F0.wireOp",EDGE,"E8.5.23.0");var subQ1=sQuery(id+"F0.wireOp",EDGE,"E8.3.18.0");var subQ2=makeQuery(id+"F0.imprint","INTERSECT",VERTEX,{"derivedFrom":[subQ1,subQ0]});Q330=makeQuery(id+"F0.imprint","IMPRINT",FACE,{"disambiguationData":[TD([[makeQuery(id+"F0.imprint","IMPRINT",EDGE,{"disambiguationData":[TD([[subQ2,-1.0]])],"derivedFrom":subQ1}),-1.0]])]});}
            var Q331;
            {var subQ0=sQuery(id+"F0.wireOp",EDGE,"E8.5.17.0");var subQ1=sQuery(id+"F0.wireOp",EDGE,"E8.3.12.0");var subQ2=makeQuery(id+"F0.imprint","INTERSECT",VERTEX,{"derivedFrom":[subQ1,subQ0]});Q331=makeQuery(id+"F0.imprint","IMPRINT",FACE,{"disambiguationData":[TD([[makeQuery(id+"F0.imprint","IMPRINT",EDGE,{"disambiguationData":[TD([[subQ2,-1.0]])],"derivedFrom":subQ1}),-1.0]])]});}
            var Q332;
            {var subQ0=sQuery(id+"F0.wireOp",EDGE,"E7.5.7.0");var subQ1=sQuery(id+"F0.wireOp",EDGE,"E6.2.1");var subQ2=makeQuery(id+"F0.imprint","INTERSECT",VERTEX,{"derivedFrom":[subQ1,subQ0]});Q332=makeQuery(id+"F0.imprint","IMPRINT",FACE,{"disambiguationData":[TD([[makeQuery(id+"F0.imprint","IMPRINT",EDGE,{"disambiguationData":[TD([[subQ2,-1.0]])],"derivedFrom":subQ1}),-1.0]])]});}
            var Q333;
            {var subQ0=sQuery(id+"F0.wireOp",EDGE,"E9.5.25.0");var subQ1=sQuery(id+"F0.wireOp",EDGE,"E8.3.19.0");var subQ2=makeQuery(id+"F0.imprint","INTERSECT",VERTEX,{"derivedFrom":[subQ1,subQ0]});Q333=makeQuery(id+"F0.imprint","IMPRINT",FACE,{"disambiguationData":[TD([[makeQuery(id+"F0.imprint","IMPRINT",EDGE,{"disambiguationData":[TD([[subQ2,-1.0]])],"derivedFrom":subQ1}),-1.0]])]});}
            var Q334;
            {var subQ0=sQuery(id+"F0.wireOp",EDGE,"E9.3.25.0");var subQ1=sQuery(id+"F0.wireOp",EDGE,"E4");var subQ2=makeQuery(id+"F0.imprint","INTERSECT",VERTEX,{"derivedFrom":[subQ1,subQ0]});Q334=makeQuery(id+"F0.imprint","IMPRINT",FACE,{"disambiguationData":[TD([[makeQuery(id+"F0.imprint","IMPRINT",EDGE,{"disambiguationData":[TD([[subQ2,-1.0]])],"derivedFrom":subQ1}),-1.0]])]});}
            var Q335;
            {var subQ0=sQuery(id+"F0.wireOp",EDGE,"E7.5.9.0");var subQ1=sQuery(id+"F0.wireOp",EDGE,"E6.4.1");var subQ2=makeQuery(id+"F0.imprint","INTERSECT",VERTEX,{"derivedFrom":[subQ1,subQ0]});Q335=makeQuery(id+"F0.imprint","IMPRINT",FACE,{"disambiguationData":[TD([[makeQuery(id+"F0.imprint","IMPRINT",EDGE,{"disambiguationData":[TD([[subQ2,-1.0]])],"derivedFrom":subQ1}),-1.0]])]});}
            var Q336;
            {var subQ0=sQuery(id+"F0.wireOp",EDGE,"E7.5.7.0");var subQ1=sQuery(id+"F0.wireOp",EDGE,"E5");var subQ2=makeQuery(id+"F0.imprint","INTERSECT",VERTEX,{"derivedFrom":[subQ1,subQ0]});Q336=makeQuery(id+"F0.imprint","IMPRINT",FACE,{"disambiguationData":[TD([[makeQuery(id+"F0.imprint","IMPRINT",EDGE,{"disambiguationData":[TD([[subQ2,-1.0]])],"derivedFrom":subQ1}),1.0]])]});}
            var Q337;
            {var subQ0=sQuery(id+"F0.wireOp",EDGE,"E8.5.13.0");var subQ1=sQuery(id+"F0.wireOp",EDGE,"E7.3.7.0");var subQ2=makeQuery(id+"F0.imprint","INTERSECT",VERTEX,{"derivedFrom":[subQ1,subQ0]});Q337=makeQuery(id+"F0.imprint","IMPRINT",FACE,{"disambiguationData":[TD([[makeQuery(id+"F0.imprint","IMPRINT",EDGE,{"disambiguationData":[TD([[subQ2,-1.0]])],"derivedFrom":subQ1}),-1.0]])]});}
            var Q338;
            {var subQ0=sQuery(id+"F0.wireOp",EDGE,"E9.3.29.0");var subQ1=sQuery(id+"F0.wireOp",EDGE,"E6.3.0");var subQ2=makeQuery(id+"F0.imprint","INTERSECT",VERTEX,{"derivedFrom":[subQ1,subQ0]});Q338=makeQuery(id+"F0.imprint","IMPRINT",FACE,{"disambiguationData":[TD([[makeQuery(id+"F0.imprint","IMPRINT",EDGE,{"disambiguationData":[TD([[subQ2,-1.0]])],"derivedFrom":subQ1}),-1.0]])]});}
            var Q339;
            {var subQ0=sQuery(id+"F0.wireOp",EDGE,"E7.5.11.0");var subQ1=sQuery(id+"F0.wireOp",EDGE,"E6.4.1");var subQ2=makeQuery(id+"F0.imprint","INTERSECT",VERTEX,{"derivedFrom":[subQ1,subQ0]});Q339=makeQuery(id+"F0.imprint","IMPRINT",FACE,{"disambiguationData":[TD([[makeQuery(id+"F0.imprint","IMPRINT",EDGE,{"disambiguationData":[TD([[subQ2,-1.0]])],"derivedFrom":subQ1}),-1.0]])]});}
            var Q340;
            {var subQ0=sQuery(id+"F0.wireOp",EDGE,"E8.5.17.0");var subQ1=sQuery(id+"F0.wireOp",EDGE,"E7.3.10.0");var subQ2=makeQuery(id+"F0.imprint","INTERSECT",VERTEX,{"derivedFrom":[subQ1,subQ0]});Q340=makeQuery(id+"F0.imprint","IMPRINT",FACE,{"disambiguationData":[TD([[makeQuery(id+"F0.imprint","IMPRINT",EDGE,{"disambiguationData":[TD([[subQ2,-1.0]])],"derivedFrom":subQ1}),-1.0]])]});}
            var Q341;
            {var subQ0=sQuery(id+"F0.wireOp",EDGE,"E7.5.11.0");var subQ1=sQuery(id+"F0.wireOp",EDGE,"E6.2.1");var subQ2=makeQuery(id+"F0.imprint","INTERSECT",VERTEX,{"derivedFrom":[subQ1,subQ0]});Q341=makeQuery(id+"F0.imprint","IMPRINT",FACE,{"disambiguationData":[TD([[makeQuery(id+"F0.imprint","IMPRINT",EDGE,{"disambiguationData":[TD([[subQ2,1.0]])],"derivedFrom":subQ1}),-1.0]])]});}
            var Q342;
            {var subQ0=sQuery(id+"F0.wireOp",EDGE,"E9.5.24.0");var subQ1=sQuery(id+"F0.wireOp",EDGE,"E8.3.17.0");var subQ2=makeQuery(id+"F0.imprint","INTERSECT",VERTEX,{"derivedFrom":[subQ1,subQ0]});Q342=makeQuery(id+"F0.imprint","IMPRINT",FACE,{"disambiguationData":[TD([[makeQuery(id+"F0.imprint","IMPRINT",EDGE,{"disambiguationData":[TD([[subQ2,-1.0]])],"derivedFrom":subQ1}),-1.0]])]});}
            var Q343;
            {var subQ0=sQuery(id+"F0.wireOp",EDGE,"E8.5.21.0");var subQ1=sQuery(id+"F0.wireOp",EDGE,"E8.3.14.0");var subQ2=makeQuery(id+"F0.imprint","INTERSECT",VERTEX,{"derivedFrom":[subQ1,subQ0]});Q343=makeQuery(id+"F0.imprint","IMPRINT",FACE,{"disambiguationData":[TD([[makeQuery(id+"F0.imprint","IMPRINT",EDGE,{"disambiguationData":[TD([[subQ2,-1.0]])],"derivedFrom":subQ1}),-1.0]])]});}
            var Q344;
            {var subQ0=sQuery(id+"F0.wireOp",EDGE,"E6.4.0");var subQ1=sQuery(id+"F0.wireOp",EDGE,"E5");var subQ2=makeQuery(id+"F0.imprint","INTERSECT",VERTEX,{"derivedFrom":[subQ1,subQ0]});Q344=makeQuery(id+"F0.imprint","IMPRINT",FACE,{"disambiguationData":[TD([[makeQuery(id+"F0.imprint","IMPRINT",EDGE,{"disambiguationData":[TD([[subQ2,-1.0]])],"derivedFrom":subQ1}),-1.0]])]});}
            var Q345;
            {var subQ0=sQuery(id+"F0.wireOp",EDGE,"E7.5.8.0");var subQ1=sQuery(id+"F0.wireOp",EDGE,"E6.3.1");var subQ2=makeQuery(id+"F0.imprint","INTERSECT",VERTEX,{"derivedFrom":[subQ1,subQ0]});Q345=makeQuery(id+"F0.imprint","IMPRINT",FACE,{"disambiguationData":[TD([[makeQuery(id+"F0.imprint","IMPRINT",EDGE,{"disambiguationData":[TD([[subQ2,-1.0]])],"derivedFrom":subQ1}),-1.0]])]});}
            var Q346;
            {var subQ0=sQuery(id+"F0.wireOp",EDGE,"E9.5.26.0");var subQ1=sQuery(id+"F0.wireOp",EDGE,"E8.3.21.0");var subQ2=makeQuery(id+"F0.imprint","INTERSECT",VERTEX,{"derivedFrom":[subQ1,subQ0]});Q346=makeQuery(id+"F0.imprint","IMPRINT",FACE,{"disambiguationData":[TD([[makeQuery(id+"F0.imprint","IMPRINT",EDGE,{"disambiguationData":[TD([[subQ2,-1.0]])],"derivedFrom":subQ1}),-1.0]])]});}
            var Q347;
            {var subQ0=sQuery(id+"F0.wireOp",EDGE,"E9.3.27.0");var subQ1=sQuery(id+"F0.wireOp",EDGE,"E6.4.0");var subQ2=makeQuery(id+"F0.imprint","INTERSECT",VERTEX,{"derivedFrom":[subQ1,subQ0]});Q347=makeQuery(id+"F0.imprint","IMPRINT",FACE,{"disambiguationData":[TD([[makeQuery(id+"F0.imprint","IMPRINT",EDGE,{"disambiguationData":[TD([[subQ2,-1.0]])],"derivedFrom":subQ1}),-1.0]])]});}
            var Q348;
            {var subQ0=sQuery(id+"F0.wireOp",EDGE,"E8.5.12.0");var subQ1=sQuery(id+"F0.wireOp",EDGE,"E7.3.6.0");var subQ2=makeQuery(id+"F0.imprint","INTERSECT",VERTEX,{"derivedFrom":[subQ1,subQ0]});Q348=makeQuery(id+"F0.imprint","IMPRINT",FACE,{"disambiguationData":[TD([[makeQuery(id+"F0.imprint","IMPRINT",EDGE,{"disambiguationData":[TD([[subQ2,-1.0]])],"derivedFrom":subQ1}),-1.0]])]});}
            var Q349;
            {var subQ0=sQuery(id+"F0.wireOp",EDGE,"E8.5.16.0");var subQ1=sQuery(id+"F0.wireOp",EDGE,"E7.3.9.0");var subQ2=makeQuery(id+"F0.imprint","INTERSECT",VERTEX,{"derivedFrom":[subQ1,subQ0]});Q349=makeQuery(id+"F0.imprint","IMPRINT",FACE,{"disambiguationData":[TD([[makeQuery(id+"F0.imprint","IMPRINT",EDGE,{"disambiguationData":[TD([[subQ2,-1.0]])],"derivedFrom":subQ1}),-1.0]])]});}
            var Q350;
            {var subQ0=sQuery(id+"F0.wireOp",EDGE,"E8.3.23.0");var subQ1=sQuery(id+"F0.wireOp",EDGE,"E4");var subQ2=makeQuery(id+"F0.imprint","INTERSECT",VERTEX,{"derivedFrom":[subQ1,subQ0]});Q350=makeQuery(id+"F0.imprint","IMPRINT",FACE,{"disambiguationData":[TD([[makeQuery(id+"F0.imprint","IMPRINT",EDGE,{"disambiguationData":[TD([[subQ2,-1.0]])],"derivedFrom":subQ1}),-1.0]])]});}
            var Q351;
            {var subQ0=sQuery(id+"F0.wireOp",EDGE,"E8.5.22.0");var subQ1=sQuery(id+"F0.wireOp",EDGE,"E8.3.16.0");var subQ2=makeQuery(id+"F0.imprint","INTERSECT",VERTEX,{"derivedFrom":[subQ1,subQ0]});Q351=makeQuery(id+"F0.imprint","IMPRINT",FACE,{"disambiguationData":[TD([[makeQuery(id+"F0.imprint","IMPRINT",EDGE,{"disambiguationData":[TD([[subQ2,-1.0]])],"derivedFrom":subQ1}),-1.0]])]});}
            var Q352;
            {var subQ0=sQuery(id+"F0.wireOp",EDGE,"E9.3.25.0");var subQ1=sQuery(id+"F0.wireOp",EDGE,"E4");var subQ2=makeQuery(id+"F0.imprint","INTERSECT",VERTEX,{"derivedFrom":[subQ1,subQ0]});Q352=makeQuery(id+"F0.imprint","IMPRINT",FACE,{"disambiguationData":[TD([[makeQuery(id+"F0.imprint","IMPRINT",EDGE,{"disambiguationData":[TD([[subQ2,-1.0]])],"derivedFrom":subQ1}),1.0]])]});}
            var Q353;
            {var subQ0=sQuery(id+"F0.wireOp",EDGE,"E8.5.19.0");var subQ1=sQuery(id+"F0.wireOp",EDGE,"E8.3.13.0");var subQ2=makeQuery(id+"F0.imprint","INTERSECT",VERTEX,{"derivedFrom":[subQ1,subQ0]});Q353=makeQuery(id+"F0.imprint","IMPRINT",FACE,{"disambiguationData":[TD([[makeQuery(id+"F0.imprint","IMPRINT",EDGE,{"disambiguationData":[TD([[subQ2,-1.0]])],"derivedFrom":subQ1}),-1.0]])]});}
            var Q354;
            {var subQ0=sQuery(id+"F0.wireOp",EDGE,"E8.5.18.0");var subQ1=sQuery(id+"F0.wireOp",EDGE,"E7.3.11.0");var subQ2=makeQuery(id+"F0.imprint","INTERSECT",VERTEX,{"derivedFrom":[subQ1,subQ0]});Q354=makeQuery(id+"F0.imprint","IMPRINT",FACE,{"disambiguationData":[TD([[makeQuery(id+"F0.imprint","IMPRINT",EDGE,{"disambiguationData":[TD([[subQ2,-1.0]])],"derivedFrom":subQ1}),-1.0]])]});}
            var Q355;
            {var subQ0=sQuery(id+"F0.wireOp",EDGE,"E9.5.26.0");var subQ1=sQuery(id+"F0.wireOp",EDGE,"E8.3.17.0");var subQ2=makeQuery(id+"F0.imprint","INTERSECT",VERTEX,{"derivedFrom":[subQ1,subQ0]});Q355=makeQuery(id+"F0.imprint","IMPRINT",FACE,{"disambiguationData":[TD([[makeQuery(id+"F0.imprint","IMPRINT",EDGE,{"disambiguationData":[TD([[subQ2,1.0]])],"derivedFrom":subQ1}),-1.0]])]});}
            var Q356;
            {var subQ0=sQuery(id+"F0.wireOp",EDGE,"E6.4.0");var subQ1=sQuery(id+"F0.wireOp",EDGE,"E5");var subQ2=makeQuery(id+"F0.imprint","INTERSECT",VERTEX,{"derivedFrom":[subQ1,subQ0]});Q356=makeQuery(id+"F0.imprint","IMPRINT",FACE,{"disambiguationData":[TD([[makeQuery(id+"F0.imprint","IMPRINT",EDGE,{"disambiguationData":[TD([[subQ2,-1.0]])],"derivedFrom":subQ1}),1.0]])]});}
            var Q357;
            {var subQ0=sQuery(id+"F0.wireOp",EDGE,"E7.5.10.0");var subQ1=sQuery(id+"F0.wireOp",EDGE,"E6.3.1");var subQ2=makeQuery(id+"F0.imprint","INTERSECT",VERTEX,{"derivedFrom":[subQ1,subQ0]});Q357=makeQuery(id+"F0.imprint","IMPRINT",FACE,{"disambiguationData":[TD([[makeQuery(id+"F0.imprint","IMPRINT",EDGE,{"disambiguationData":[TD([[subQ2,-1.0]])],"derivedFrom":subQ1}),-1.0]])]});}
            var Q358;
            {var subQ0=sQuery(id+"F0.wireOp",EDGE,"E9.3.27.0");var subQ1=sQuery(id+"F0.wireOp",EDGE,"E4");var subQ2=makeQuery(id+"F0.imprint","INTERSECT",VERTEX,{"derivedFrom":[subQ1,subQ0]});Q358=makeQuery(id+"F0.imprint","IMPRINT",FACE,{"disambiguationData":[TD([[makeQuery(id+"F0.imprint","IMPRINT",EDGE,{"disambiguationData":[TD([[subQ2,-1.0]])],"derivedFrom":subQ1}),-1.0]])]});}
            var Q359;
            {var subQ0=sQuery(id+"F0.wireOp",EDGE,"E9.3.28.0");var subQ1=sQuery(id+"F0.wireOp",EDGE,"E6.4.0");var subQ2=makeQuery(id+"F0.imprint","INTERSECT",VERTEX,{"derivedFrom":[subQ1,subQ0]});Q359=makeQuery(id+"F0.imprint","IMPRINT",FACE,{"disambiguationData":[TD([[makeQuery(id+"F0.imprint","IMPRINT",EDGE,{"disambiguationData":[TD([[subQ2,-1.0]])],"derivedFrom":subQ1}),-1.0]])]});}
            var Q360;
            {var subQ0=sQuery(id+"F0.wireOp",EDGE,"E8.5.22.0");var subQ1=sQuery(id+"F0.wireOp",EDGE,"E8.3.15.0");var subQ2=makeQuery(id+"F0.imprint","INTERSECT",VERTEX,{"derivedFrom":[subQ1,subQ0]});Q360=makeQuery(id+"F0.imprint","IMPRINT",FACE,{"disambiguationData":[TD([[makeQuery(id+"F0.imprint","IMPRINT",EDGE,{"disambiguationData":[TD([[subQ2,-1.0]])],"derivedFrom":subQ1}),-1.0]])]});}
            var Q361;
            {var subQ0=sQuery(id+"F0.wireOp",EDGE,"E8.5.13.0");var subQ1=sQuery(id+"F0.wireOp",EDGE,"E7.3.6.0");var subQ2=makeQuery(id+"F0.imprint","INTERSECT",VERTEX,{"derivedFrom":[subQ1,subQ0]});Q361=makeQuery(id+"F0.imprint","IMPRINT",FACE,{"disambiguationData":[TD([[makeQuery(id+"F0.imprint","IMPRINT",EDGE,{"disambiguationData":[TD([[subQ2,-1.0]])],"derivedFrom":subQ1}),-1.0]])]});}
            var Q362;
            {var subQ0=sQuery(id+"F0.wireOp",EDGE,"E8.5.18.0");var subQ1=sQuery(id+"F0.wireOp",EDGE,"E7.3.9.0");var subQ2=makeQuery(id+"F0.imprint","INTERSECT",VERTEX,{"derivedFrom":[subQ1,subQ0]});Q362=makeQuery(id+"F0.imprint","IMPRINT",FACE,{"disambiguationData":[TD([[makeQuery(id+"F0.imprint","IMPRINT",EDGE,{"disambiguationData":[TD([[subQ2,1.0]])],"derivedFrom":subQ1}),-1.0]])]});}
            var Q363;
            {var subQ0=sQuery(id+"F0.wireOp",EDGE,"E9.3.24.0");var subQ1=sQuery(id+"F0.wireOp",EDGE,"E4");var subQ2=makeQuery(id+"F0.imprint","INTERSECT",VERTEX,{"derivedFrom":[subQ1,subQ0]});Q363=makeQuery(id+"F0.imprint","IMPRINT",FACE,{"disambiguationData":[TD([[makeQuery(id+"F0.imprint","IMPRINT",EDGE,{"disambiguationData":[TD([[subQ2,-1.0]])],"derivedFrom":subQ1}),-1.0]])]});}
            var Q364;
            {var subQ0=sQuery(id+"F0.wireOp",EDGE,"E8.5.22.0");var subQ1=sQuery(id+"F0.wireOp",EDGE,"E8.3.13.0");var subQ2=makeQuery(id+"F0.imprint","INTERSECT",VERTEX,{"derivedFrom":[subQ1,subQ0]});Q364=makeQuery(id+"F0.imprint","IMPRINT",FACE,{"disambiguationData":[TD([[makeQuery(id+"F0.imprint","IMPRINT",EDGE,{"disambiguationData":[TD([[subQ2,1.0]])],"derivedFrom":subQ1}),-1.0]])]});}
            var Q365;
            {var subQ0=sQuery(id+"F0.wireOp",EDGE,"E9.3.24.0");var subQ1=sQuery(id+"F0.wireOp",EDGE,"E6.1.0");var subQ2=makeQuery(id+"F0.imprint","INTERSECT",VERTEX,{"derivedFrom":[subQ1,subQ0]});Q365=makeQuery(id+"F0.imprint","IMPRINT",FACE,{"disambiguationData":[TD([[makeQuery(id+"F0.imprint","IMPRINT",EDGE,{"disambiguationData":[TD([[subQ2,-1.0]])],"derivedFrom":subQ1}),-1.0]])]});}
            var Q366;
            {var subQ0=sQuery(id+"F0.wireOp",EDGE,"E9.5.26.0");var subQ1=sQuery(id+"F0.wireOp",EDGE,"E8.3.20.0");var subQ2=makeQuery(id+"F0.imprint","INTERSECT",VERTEX,{"derivedFrom":[subQ1,subQ0]});Q366=makeQuery(id+"F0.imprint","IMPRINT",FACE,{"disambiguationData":[TD([[makeQuery(id+"F0.imprint","IMPRINT",EDGE,{"disambiguationData":[TD([[subQ2,-1.0]])],"derivedFrom":subQ1}),-1.0]])]});}
            var Q367;
            {var subQ0=sQuery(id+"F0.wireOp",EDGE,"E8.5.12.0");var subQ1=sQuery(id+"F0.wireOp",EDGE,"E6.5.1");var subQ2=makeQuery(id+"F0.imprint","INTERSECT",VERTEX,{"derivedFrom":[subQ1,subQ0]});Q367=makeQuery(id+"F0.imprint","IMPRINT",FACE,{"disambiguationData":[TD([[makeQuery(id+"F0.imprint","IMPRINT",EDGE,{"disambiguationData":[TD([[subQ2,-1.0]])],"derivedFrom":subQ1}),-1.0]])]});}
            var Q368;
            {var subQ0=sQuery(id+"F0.wireOp",EDGE,"E9.3.28.0");var subQ1=sQuery(id+"F0.wireOp",EDGE,"E6.5.0");var subQ2=makeQuery(id+"F0.imprint","INTERSECT",VERTEX,{"derivedFrom":[subQ1,subQ0]});Q368=makeQuery(id+"F0.imprint","IMPRINT",FACE,{"disambiguationData":[TD([[makeQuery(id+"F0.imprint","IMPRINT",EDGE,{"disambiguationData":[TD([[subQ2,-1.0]])],"derivedFrom":subQ1}),-1.0]])]});}
            var Q369;
            {var subQ0=sQuery(id+"F0.wireOp",EDGE,"E8.5.18.0");var subQ1=sQuery(id+"F0.wireOp",EDGE,"E8.3.12.0");var subQ2=makeQuery(id+"F0.imprint","INTERSECT",VERTEX,{"derivedFrom":[subQ1,subQ0]});Q369=makeQuery(id+"F0.imprint","IMPRINT",FACE,{"disambiguationData":[TD([[makeQuery(id+"F0.imprint","IMPRINT",EDGE,{"disambiguationData":[TD([[subQ2,-1.0]])],"derivedFrom":subQ1}),-1.0]])]});}
            var Q370;
            {var subQ0=sQuery(id+"F0.wireOp",EDGE,"E8.5.15.0");var subQ1=sQuery(id+"F0.wireOp",EDGE,"E7.3.9.0");var subQ2=makeQuery(id+"F0.imprint","INTERSECT",VERTEX,{"derivedFrom":[subQ1,subQ0]});Q370=makeQuery(id+"F0.imprint","IMPRINT",FACE,{"disambiguationData":[TD([[makeQuery(id+"F0.imprint","IMPRINT",EDGE,{"disambiguationData":[TD([[subQ2,-1.0]])],"derivedFrom":subQ1}),-1.0]])]});}
            var Q371;
            {var subQ0=sQuery(id+"F0.wireOp",EDGE,"E9.3.27.0");var subQ1=sQuery(id+"F0.wireOp",EDGE,"E6.1.0");var subQ2=makeQuery(id+"F0.imprint","INTERSECT",VERTEX,{"derivedFrom":[subQ1,subQ0]});Q371=makeQuery(id+"F0.imprint","IMPRINT",FACE,{"disambiguationData":[TD([[makeQuery(id+"F0.imprint","IMPRINT",EDGE,{"disambiguationData":[TD([[subQ2,-1.0]])],"derivedFrom":subQ1}),-1.0]])]});}
            var Q372;
            {var subQ0=sQuery(id+"F0.wireOp",EDGE,"E7.5.10.0");var subQ1=sQuery(id+"F0.wireOp",EDGE,"E6.4.1");var subQ2=makeQuery(id+"F0.imprint","INTERSECT",VERTEX,{"derivedFrom":[subQ1,subQ0]});Q372=makeQuery(id+"F0.imprint","IMPRINT",FACE,{"disambiguationData":[TD([[makeQuery(id+"F0.imprint","IMPRINT",EDGE,{"disambiguationData":[TD([[subQ2,-1.0]])],"derivedFrom":subQ1}),-1.0]])]});}
            var Q373;
            {var subQ0=sQuery(id+"F0.wireOp",EDGE,"E9.3.25.0");var subQ1=sQuery(id+"F0.wireOp",EDGE,"E6.1.0");var subQ2=makeQuery(id+"F0.imprint","INTERSECT",VERTEX,{"derivedFrom":[subQ1,subQ0]});Q373=makeQuery(id+"F0.imprint","IMPRINT",FACE,{"disambiguationData":[TD([[makeQuery(id+"F0.imprint","IMPRINT",EDGE,{"disambiguationData":[TD([[subQ2,-1.0]])],"derivedFrom":subQ1}),-1.0]])]});}
            var Q374;
            {var subQ0=sQuery(id+"F0.wireOp",EDGE,"E7.5.10.0");var subQ1=sQuery(id+"F0.wireOp",EDGE,"E6.5.1");var subQ2=makeQuery(id+"F0.imprint","INTERSECT",VERTEX,{"derivedFrom":[subQ1,subQ0]});Q374=makeQuery(id+"F0.imprint","IMPRINT",FACE,{"disambiguationData":[TD([[makeQuery(id+"F0.imprint","IMPRINT",EDGE,{"disambiguationData":[TD([[subQ2,-1.0]])],"derivedFrom":subQ1}),-1.0]])]});}
            var Q375;
            {var subQ0=sQuery(id+"F0.wireOp",EDGE,"E8.5.14.0");var subQ1=sQuery(id+"F0.wireOp",EDGE,"E6.5.1");var subQ2=makeQuery(id+"F0.imprint","INTERSECT",VERTEX,{"derivedFrom":[subQ1,subQ0]});Q375=makeQuery(id+"F0.imprint","IMPRINT",FACE,{"disambiguationData":[TD([[makeQuery(id+"F0.imprint","IMPRINT",EDGE,{"disambiguationData":[TD([[subQ2,1.0]])],"derivedFrom":subQ1}),-1.0]])]});}
            var Q376;
            {var subQ0=sQuery(id+"F0.wireOp",EDGE,"E7.5.6.0");var subQ1=sQuery(id+"F0.wireOp",EDGE,"E5");var subQ2=makeQuery(id+"F0.imprint","INTERSECT",VERTEX,{"derivedFrom":[subQ1,subQ0]});Q376=makeQuery(id+"F0.imprint","IMPRINT",FACE,{"disambiguationData":[TD([[makeQuery(id+"F0.imprint","IMPRINT",EDGE,{"disambiguationData":[TD([[subQ2,-1.0]])],"derivedFrom":subQ1}),-1.0]])]});}
            var Q377;
            {var subQ0=sQuery(id+"F0.wireOp",EDGE,"E8.5.19.0");var subQ1=sQuery(id+"F0.wireOp",EDGE,"E8.3.12.0");var subQ2=makeQuery(id+"F0.imprint","INTERSECT",VERTEX,{"derivedFrom":[subQ1,subQ0]});Q377=makeQuery(id+"F0.imprint","IMPRINT",FACE,{"disambiguationData":[TD([[makeQuery(id+"F0.imprint","IMPRINT",EDGE,{"disambiguationData":[TD([[subQ2,-1.0]])],"derivedFrom":subQ1}),-1.0]])]});}
            var Q378;
            {var subQ0=sQuery(id+"F0.wireOp",EDGE,"E8.5.17.0");var subQ1=sQuery(id+"F0.wireOp",EDGE,"E7.3.8.0");var subQ2=makeQuery(id+"F0.imprint","INTERSECT",VERTEX,{"derivedFrom":[subQ1,subQ0]});Q378=makeQuery(id+"F0.imprint","IMPRINT",FACE,{"disambiguationData":[TD([[makeQuery(id+"F0.imprint","IMPRINT",EDGE,{"disambiguationData":[TD([[subQ2,1.0]])],"derivedFrom":subQ1}),-1.0]])]});}
            var Q379;
            {var subQ0=sQuery(id+"F0.wireOp",EDGE,"E9.5.26.0");var subQ1=sQuery(id+"F0.wireOp",EDGE,"E8.3.19.0");var subQ2=makeQuery(id+"F0.imprint","INTERSECT",VERTEX,{"derivedFrom":[subQ1,subQ0]});Q379=makeQuery(id+"F0.imprint","IMPRINT",FACE,{"disambiguationData":[TD([[makeQuery(id+"F0.imprint","IMPRINT",EDGE,{"disambiguationData":[TD([[subQ2,-1.0]])],"derivedFrom":subQ1}),-1.0]])]});}
            var Q380;
            {var subQ0=sQuery(id+"F0.wireOp",EDGE,"E9.3.26.0");var subQ1=sQuery(id+"F0.wireOp",EDGE,"E6.1.0");var subQ2=makeQuery(id+"F0.imprint","INTERSECT",VERTEX,{"derivedFrom":[subQ1,subQ0]});Q380=makeQuery(id+"F0.imprint","IMPRINT",FACE,{"disambiguationData":[TD([[makeQuery(id+"F0.imprint","IMPRINT",EDGE,{"disambiguationData":[TD([[subQ2,-1.0]])],"derivedFrom":subQ1}),-1.0]])]});}
            var Q381;
            {var subQ0=sQuery(id+"F0.wireOp",EDGE,"E8.5.20.0");var subQ1=sQuery(id+"F0.wireOp",EDGE,"E8.3.13.0");var subQ2=makeQuery(id+"F0.imprint","INTERSECT",VERTEX,{"derivedFrom":[subQ1,subQ0]});Q381=makeQuery(id+"F0.imprint","IMPRINT",FACE,{"disambiguationData":[TD([[makeQuery(id+"F0.imprint","IMPRINT",EDGE,{"disambiguationData":[TD([[subQ2,-1.0]])],"derivedFrom":subQ1}),-1.0]])]});}
            var Q382;
            {var subQ0=sQuery(id+"F0.wireOp",EDGE,"E9.3.25.0");var subQ1=sQuery(id+"F0.wireOp",EDGE,"E6.2.0");var subQ2=makeQuery(id+"F0.imprint","INTERSECT",VERTEX,{"derivedFrom":[subQ1,subQ0]});Q382=makeQuery(id+"F0.imprint","IMPRINT",FACE,{"disambiguationData":[TD([[makeQuery(id+"F0.imprint","IMPRINT",EDGE,{"disambiguationData":[TD([[subQ2,-1.0]])],"derivedFrom":subQ1}),-1.0]])]});}
            var Q383;
            {var subQ0=sQuery(id+"F0.wireOp",EDGE,"E8.5.21.0");var subQ1=sQuery(id+"F0.wireOp",EDGE,"E8.3.12.0");var subQ2=makeQuery(id+"F0.imprint","INTERSECT",VERTEX,{"derivedFrom":[subQ1,subQ0]});Q383=makeQuery(id+"F0.imprint","IMPRINT",FACE,{"disambiguationData":[TD([[makeQuery(id+"F0.imprint","IMPRINT",EDGE,{"disambiguationData":[TD([[subQ2,1.0]])],"derivedFrom":subQ1}),-1.0]])]});}
            var Q384;
            {var subQ0=sQuery(id+"F0.wireOp",EDGE,"E7.5.11.0");var subQ1=sQuery(id+"F0.wireOp",EDGE,"E6.5.1");var subQ2=makeQuery(id+"F0.imprint","INTERSECT",VERTEX,{"derivedFrom":[subQ1,subQ0]});Q384=makeQuery(id+"F0.imprint","IMPRINT",FACE,{"disambiguationData":[TD([[makeQuery(id+"F0.imprint","IMPRINT",EDGE,{"disambiguationData":[TD([[subQ2,-1.0]])],"derivedFrom":subQ1}),-1.0]])]});}
            var Q385;
            {var subQ0=sQuery(id+"F0.wireOp",EDGE,"E9.5.27.0");var subQ1=sQuery(id+"F0.wireOp",EDGE,"E8.3.18.0");var subQ2=makeQuery(id+"F0.imprint","INTERSECT",VERTEX,{"derivedFrom":[subQ1,subQ0]});Q385=makeQuery(id+"F0.imprint","IMPRINT",FACE,{"disambiguationData":[TD([[makeQuery(id+"F0.imprint","IMPRINT",EDGE,{"disambiguationData":[TD([[subQ2,1.0]])],"derivedFrom":subQ1}),-1.0]])]});}
            var Q386;
            {var subQ0=sQuery(id+"F0.wireOp",EDGE,"E9.3.28.0");var subQ1=sQuery(id+"F0.wireOp",EDGE,"E6.2.0");var subQ2=makeQuery(id+"F0.imprint","INTERSECT",VERTEX,{"derivedFrom":[subQ1,subQ0]});Q386=makeQuery(id+"F0.imprint","IMPRINT",FACE,{"disambiguationData":[TD([[makeQuery(id+"F0.imprint","IMPRINT",EDGE,{"disambiguationData":[TD([[subQ2,-1.0]])],"derivedFrom":subQ1}),-1.0]])]});}
            var Q387;
            {var subQ0=sQuery(id+"F0.wireOp",EDGE,"E7.5.11.0");var subQ1=sQuery(id+"F0.wireOp",EDGE,"E7.3.6.0");var subQ2=makeQuery(id+"F0.imprint","INTERSECT",VERTEX,{"derivedFrom":[subQ1,subQ0]});Q387=makeQuery(id+"F0.imprint","IMPRINT",FACE,{"disambiguationData":[TD([[makeQuery(id+"F0.imprint","IMPRINT",EDGE,{"disambiguationData":[TD([[subQ2,-1.0]])],"derivedFrom":subQ1}),-1.0]])]});}
            var Q388;
            {var subQ0=sQuery(id+"F0.wireOp",EDGE,"E8.5.14.0");var subQ1=sQuery(id+"F0.wireOp",EDGE,"E7.3.9.0");var subQ2=makeQuery(id+"F0.imprint","INTERSECT",VERTEX,{"derivedFrom":[subQ1,subQ0]});Q388=makeQuery(id+"F0.imprint","IMPRINT",FACE,{"disambiguationData":[TD([[makeQuery(id+"F0.imprint","IMPRINT",EDGE,{"disambiguationData":[TD([[subQ2,-1.0]])],"derivedFrom":subQ1}),-1.0]])]});}
            var Q389;
            {var subQ0=sQuery(id+"F0.wireOp",EDGE,"E7.5.7.0");var subQ1=sQuery(id+"F0.wireOp",EDGE,"E5");var subQ2=makeQuery(id+"F0.imprint","INTERSECT",VERTEX,{"derivedFrom":[subQ1,subQ0]});Q389=makeQuery(id+"F0.imprint","IMPRINT",FACE,{"disambiguationData":[TD([[makeQuery(id+"F0.imprint","IMPRINT",EDGE,{"disambiguationData":[TD([[subQ2,-1.0]])],"derivedFrom":subQ1}),-1.0]])]});}
            var Q390;
            {var subQ0=sQuery(id+"F0.wireOp",EDGE,"E8.5.20.0");var subQ1=sQuery(id+"F0.wireOp",EDGE,"E7.3.11.0");var subQ2=makeQuery(id+"F0.imprint","INTERSECT",VERTEX,{"derivedFrom":[subQ1,subQ0]});Q390=makeQuery(id+"F0.imprint","IMPRINT",FACE,{"disambiguationData":[TD([[makeQuery(id+"F0.imprint","IMPRINT",EDGE,{"disambiguationData":[TD([[subQ2,1.0]])],"derivedFrom":subQ1}),-1.0]])]});}
            var Q391;
            {var subQ0=sQuery(id+"F0.wireOp",EDGE,"E9.3.29.0");var subQ1=sQuery(id+"F0.wireOp",EDGE,"E6.5.0");var subQ2=makeQuery(id+"F0.imprint","INTERSECT",VERTEX,{"derivedFrom":[subQ1,subQ0]});Q391=makeQuery(id+"F0.imprint","IMPRINT",FACE,{"disambiguationData":[TD([[makeQuery(id+"F0.imprint","IMPRINT",EDGE,{"disambiguationData":[TD([[subQ2,-1.0]])],"derivedFrom":subQ1}),-1.0]])]});}
            var Q392;
            {var subQ0=sQuery(id+"F0.wireOp",EDGE,"E7.5.10.0");var subQ1=sQuery(id+"F0.wireOp",EDGE,"E6.1.1");var subQ2=makeQuery(id+"F0.imprint","INTERSECT",VERTEX,{"derivedFrom":[subQ1,subQ0]});Q392=makeQuery(id+"F0.imprint","IMPRINT",FACE,{"disambiguationData":[TD([[makeQuery(id+"F0.imprint","IMPRINT",EDGE,{"disambiguationData":[TD([[subQ2,1.0]])],"derivedFrom":subQ1}),-1.0]])]});}
            var Q393;
            {var subQ0=sQuery(id+"F0.wireOp",EDGE,"E8.5.23.0");var subQ1=sQuery(id+"F0.wireOp",EDGE,"E8.3.14.0");var subQ2=makeQuery(id+"F0.imprint","INTERSECT",VERTEX,{"derivedFrom":[subQ1,subQ0]});Q393=makeQuery(id+"F0.imprint","IMPRINT",FACE,{"disambiguationData":[TD([[makeQuery(id+"F0.imprint","IMPRINT",EDGE,{"disambiguationData":[TD([[subQ2,1.0]])],"derivedFrom":subQ1}),-1.0]])]});}
            var Q394;
            {var subQ0=sQuery(id+"F0.wireOp",EDGE,"E8.5.15.0");var subQ1=sQuery(id+"F0.wireOp",EDGE,"E7.3.8.0");var subQ2=makeQuery(id+"F0.imprint","INTERSECT",VERTEX,{"derivedFrom":[subQ1,subQ0]});Q394=makeQuery(id+"F0.imprint","IMPRINT",FACE,{"disambiguationData":[TD([[makeQuery(id+"F0.imprint","IMPRINT",EDGE,{"disambiguationData":[TD([[subQ2,-1.0]])],"derivedFrom":subQ1}),-1.0]])]});}
            var Q395;
            {var subQ0=sQuery(id+"F0.wireOp",EDGE,"E9.5.28.0");var subQ1=sQuery(id+"F0.wireOp",EDGE,"E8.3.19.0");var subQ2=makeQuery(id+"F0.imprint","INTERSECT",VERTEX,{"derivedFrom":[subQ1,subQ0]});Q395=makeQuery(id+"F0.imprint","IMPRINT",FACE,{"disambiguationData":[TD([[makeQuery(id+"F0.imprint","IMPRINT",EDGE,{"disambiguationData":[TD([[subQ2,1.0]])],"derivedFrom":subQ1}),-1.0]])]});}
            var Q396;
            {var subQ0=sQuery(id+"F0.wireOp",EDGE,"E9.3.27.0");var subQ1=sQuery(id+"F0.wireOp",EDGE,"E6.2.0");var subQ2=makeQuery(id+"F0.imprint","INTERSECT",VERTEX,{"derivedFrom":[subQ1,subQ0]});Q396=makeQuery(id+"F0.imprint","IMPRINT",FACE,{"disambiguationData":[TD([[makeQuery(id+"F0.imprint","IMPRINT",EDGE,{"disambiguationData":[TD([[subQ2,-1.0]])],"derivedFrom":subQ1}),-1.0]])]});}
            var Q397;
            {var subQ0=sQuery(id+"F0.wireOp",EDGE,"E9.3.26.0");var subQ1=sQuery(id+"F0.wireOp",EDGE,"E6.2.0");var subQ2=makeQuery(id+"F0.imprint","INTERSECT",VERTEX,{"derivedFrom":[subQ1,subQ0]});Q397=makeQuery(id+"F0.imprint","IMPRINT",FACE,{"disambiguationData":[TD([[makeQuery(id+"F0.imprint","IMPRINT",EDGE,{"disambiguationData":[TD([[subQ2,-1.0]])],"derivedFrom":subQ1}),-1.0]])]});}
            var Q398;
            {var subQ0=sQuery(id+"F0.wireOp",EDGE,"E9.5.27.0");var subQ1=sQuery(id+"F0.wireOp",EDGE,"E8.3.20.0");var subQ2=makeQuery(id+"F0.imprint","INTERSECT",VERTEX,{"derivedFrom":[subQ1,subQ0]});Q398=makeQuery(id+"F0.imprint","IMPRINT",FACE,{"disambiguationData":[TD([[makeQuery(id+"F0.imprint","IMPRINT",EDGE,{"disambiguationData":[TD([[subQ2,-1.0]])],"derivedFrom":subQ1}),-1.0]])]});}
            var Q399;
            {var subQ0=sQuery(id+"F0.wireOp",EDGE,"E9.3.26.0");var subQ1=sQuery(id+"F0.wireOp",EDGE,"E6.3.0");var subQ2=makeQuery(id+"F0.imprint","INTERSECT",VERTEX,{"derivedFrom":[subQ1,subQ0]});Q399=makeQuery(id+"F0.imprint","IMPRINT",FACE,{"disambiguationData":[TD([[makeQuery(id+"F0.imprint","IMPRINT",EDGE,{"disambiguationData":[TD([[subQ2,-1.0]])],"derivedFrom":subQ1}),-1.0]])]});}
            var Q400;
            {var subQ0=sQuery(id+"F0.wireOp",EDGE,"E9.3.29.0");var subQ1=sQuery(id+"F0.wireOp",EDGE,"E6.4.0");var subQ2=makeQuery(id+"F0.imprint","INTERSECT",VERTEX,{"derivedFrom":[subQ1,subQ0]});Q400=makeQuery(id+"F0.imprint","IMPRINT",FACE,{"disambiguationData":[TD([[makeQuery(id+"F0.imprint","IMPRINT",EDGE,{"disambiguationData":[TD([[subQ2,-1.0]])],"derivedFrom":subQ1}),-1.0]])]});}
            var Q401;
            {var subQ0=sQuery(id+"F0.wireOp",EDGE,"E8.5.16.0");var subQ1=sQuery(id+"F0.wireOp",EDGE,"E7.3.7.0");var subQ2=makeQuery(id+"F0.imprint","INTERSECT",VERTEX,{"derivedFrom":[subQ1,subQ0]});Q401=makeQuery(id+"F0.imprint","IMPRINT",FACE,{"disambiguationData":[TD([[makeQuery(id+"F0.imprint","IMPRINT",EDGE,{"disambiguationData":[TD([[subQ2,1.0]])],"derivedFrom":subQ1}),-1.0]])]});}
            var Q402;
            {var subQ0=sQuery(id+"F0.wireOp",EDGE,"E9.3.28.0");var subQ1=sQuery(id+"F0.wireOp",EDGE,"E6.1.0");var subQ2=makeQuery(id+"F0.imprint","INTERSECT",VERTEX,{"derivedFrom":[subQ1,subQ0]});Q402=makeQuery(id+"F0.imprint","IMPRINT",FACE,{"disambiguationData":[TD([[makeQuery(id+"F0.imprint","IMPRINT",EDGE,{"disambiguationData":[TD([[subQ2,-1.0]])],"derivedFrom":subQ1}),-1.0]])]});}
            var Q403;
            {var subQ0=sQuery(id+"F0.wireOp",EDGE,"E7.5.9.0");var subQ1=sQuery(id+"F0.wireOp",EDGE,"E6.2.1");var subQ2=makeQuery(id+"F0.imprint","INTERSECT",VERTEX,{"derivedFrom":[subQ1,subQ0]});Q403=makeQuery(id+"F0.imprint","IMPRINT",FACE,{"disambiguationData":[TD([[makeQuery(id+"F0.imprint","IMPRINT",EDGE,{"disambiguationData":[TD([[subQ2,-1.0]])],"derivedFrom":subQ1}),-1.0]])]});}
            var Q404;
            {var subQ0=sQuery(id+"F0.wireOp",EDGE,"E8.5.23.0");var subQ1=sQuery(id+"F0.wireOp",EDGE,"E8.3.16.0");var subQ2=makeQuery(id+"F0.imprint","INTERSECT",VERTEX,{"derivedFrom":[subQ1,subQ0]});Q404=makeQuery(id+"F0.imprint","IMPRINT",FACE,{"disambiguationData":[TD([[makeQuery(id+"F0.imprint","IMPRINT",EDGE,{"disambiguationData":[TD([[subQ2,-1.0]])],"derivedFrom":subQ1}),-1.0]])]});}
            var Q405;
            {var subQ0=sQuery(id+"F0.wireOp",EDGE,"E8.5.19.0");var subQ1=sQuery(id+"F0.wireOp",EDGE,"E7.3.10.0");var subQ2=makeQuery(id+"F0.imprint","INTERSECT",VERTEX,{"derivedFrom":[subQ1,subQ0]});Q405=makeQuery(id+"F0.imprint","IMPRINT",FACE,{"disambiguationData":[TD([[makeQuery(id+"F0.imprint","IMPRINT",EDGE,{"disambiguationData":[TD([[subQ2,1.0]])],"derivedFrom":subQ1}),-1.0]])]});}
            var Q406;
            {var subQ0=sQuery(id+"F0.wireOp",EDGE,"E9.3.28.0");var subQ1=sQuery(id+"F0.wireOp",EDGE,"E6.3.0");var subQ2=makeQuery(id+"F0.imprint","INTERSECT",VERTEX,{"derivedFrom":[subQ1,subQ0]});Q406=makeQuery(id+"F0.imprint","IMPRINT",FACE,{"disambiguationData":[TD([[makeQuery(id+"F0.imprint","IMPRINT",EDGE,{"disambiguationData":[TD([[subQ2,-1.0]])],"derivedFrom":subQ1}),-1.0]])]});}
            var Q407;
            {var subQ0=sQuery(id+"F0.wireOp",EDGE,"E9.3.27.0");var subQ1=sQuery(id+"F0.wireOp",EDGE,"E6.3.0");var subQ2=makeQuery(id+"F0.imprint","INTERSECT",VERTEX,{"derivedFrom":[subQ1,subQ0]});Q407=makeQuery(id+"F0.imprint","IMPRINT",FACE,{"disambiguationData":[TD([[makeQuery(id+"F0.imprint","IMPRINT",EDGE,{"disambiguationData":[TD([[subQ2,-1.0]])],"derivedFrom":subQ1}),-1.0]])]});}
            var Q408;
            {var subQ0=sQuery(id+"F0.wireOp",EDGE,"E9.5.24.0");var subQ1=sQuery(id+"F0.wireOp",EDGE,"E8.3.15.0");var subQ2=makeQuery(id+"F0.imprint","INTERSECT",VERTEX,{"derivedFrom":[subQ1,subQ0]});Q408=makeQuery(id+"F0.imprint","IMPRINT",FACE,{"disambiguationData":[TD([[makeQuery(id+"F0.imprint","IMPRINT",EDGE,{"disambiguationData":[TD([[subQ2,1.0]])],"derivedFrom":subQ1}),-1.0]])]});}
            var Q409;
            {var subQ0=sQuery(id+"F0.wireOp",EDGE,"E7.5.9.0");var subQ1=sQuery(id+"F0.wireOp",EDGE,"E6.3.1");var subQ2=makeQuery(id+"F0.imprint","INTERSECT",VERTEX,{"derivedFrom":[subQ1,subQ0]});Q409=makeQuery(id+"F0.imprint","IMPRINT",FACE,{"disambiguationData":[TD([[makeQuery(id+"F0.imprint","IMPRINT",EDGE,{"disambiguationData":[TD([[subQ2,-1.0]])],"derivedFrom":subQ1}),-1.0]])]});}
            var Q410;
            {var subQ0=sQuery(id+"F0.wireOp",EDGE,"E9.5.27.0");var subQ1=sQuery(id+"F0.wireOp",EDGE,"E8.3.21.0");var subQ2=makeQuery(id+"F0.imprint","INTERSECT",VERTEX,{"derivedFrom":[subQ1,subQ0]});Q410=makeQuery(id+"F0.imprint","IMPRINT",FACE,{"disambiguationData":[TD([[makeQuery(id+"F0.imprint","IMPRINT",EDGE,{"disambiguationData":[TD([[subQ2,-1.0]])],"derivedFrom":subQ1}),-1.0]])]});}
            var Q411;
            {var subQ0=sQuery(id+"F0.wireOp",EDGE,"E6.5.0");var subQ1=sQuery(id+"F0.wireOp",EDGE,"E5");var subQ2=makeQuery(id+"F0.imprint","INTERSECT",VERTEX,{"derivedFrom":[subQ1,subQ0]});Q411=makeQuery(id+"F0.imprint","IMPRINT",FACE,{"disambiguationData":[TD([[makeQuery(id+"F0.imprint","IMPRINT",EDGE,{"disambiguationData":[TD([[subQ2,-1.0]])],"derivedFrom":subQ1}),1.0]])]});}
            var Q412;
            {var subQ0=sQuery(id+"F0.wireOp",EDGE,"E8.5.15.0");var subQ1=sQuery(id+"F0.wireOp",EDGE,"E7.3.6.0");var subQ2=makeQuery(id+"F0.imprint","INTERSECT",VERTEX,{"derivedFrom":[subQ1,subQ0]});Q412=makeQuery(id+"F0.imprint","IMPRINT",FACE,{"disambiguationData":[TD([[makeQuery(id+"F0.imprint","IMPRINT",EDGE,{"disambiguationData":[TD([[subQ2,1.0]])],"derivedFrom":subQ1}),-1.0]])]});}
            var Q413;
            {var subQ0=sQuery(id+"F0.wireOp",EDGE,"E7.5.6.0");var subQ1=sQuery(id+"F0.wireOp",EDGE,"E6.1.1");var subQ2=makeQuery(id+"F0.imprint","INTERSECT",VERTEX,{"derivedFrom":[subQ1,subQ0]});Q413=makeQuery(id+"F0.imprint","IMPRINT",FACE,{"disambiguationData":[TD([[makeQuery(id+"F0.imprint","IMPRINT",EDGE,{"disambiguationData":[TD([[subQ2,-1.0]])],"derivedFrom":subQ1}),-1.0]])]});}
            var Q414;
            {var subQ0=sQuery(id+"F0.wireOp",EDGE,"E7.5.7.0");var subQ1=sQuery(id+"F0.wireOp",EDGE,"E6.1.1");var subQ2=makeQuery(id+"F0.imprint","INTERSECT",VERTEX,{"derivedFrom":[subQ1,subQ0]});Q414=makeQuery(id+"F0.imprint","IMPRINT",FACE,{"disambiguationData":[TD([[makeQuery(id+"F0.imprint","IMPRINT",EDGE,{"disambiguationData":[TD([[subQ2,-1.0]])],"derivedFrom":subQ1}),-1.0]])]});}
            var Q415;
            {var subQ0=sQuery(id+"F0.wireOp",EDGE,"E8.5.14.0");var subQ1=sQuery(id+"F0.wireOp",EDGE,"E7.3.8.0");var subQ2=makeQuery(id+"F0.imprint","INTERSECT",VERTEX,{"derivedFrom":[subQ1,subQ0]});Q415=makeQuery(id+"F0.imprint","IMPRINT",FACE,{"disambiguationData":[TD([[makeQuery(id+"F0.imprint","IMPRINT",EDGE,{"disambiguationData":[TD([[subQ2,-1.0]])],"derivedFrom":subQ1}),-1.0]])]});}
            var Q416;
            {var subQ0=sQuery(id+"F0.wireOp",EDGE,"E9.5.25.0");var subQ1=sQuery(id+"F0.wireOp",EDGE,"E8.3.16.0");var subQ2=makeQuery(id+"F0.imprint","INTERSECT",VERTEX,{"derivedFrom":[subQ1,subQ0]});Q416=makeQuery(id+"F0.imprint","IMPRINT",FACE,{"disambiguationData":[TD([[makeQuery(id+"F0.imprint","IMPRINT",EDGE,{"disambiguationData":[TD([[subQ2,1.0]])],"derivedFrom":subQ1}),-1.0]])]});}
            var Q417;
            {var subQ0=sQuery(id+"F0.wireOp",EDGE,"E9.5.27.0");var subQ1=sQuery(id+"F0.wireOp",EDGE,"E8.3.22.0");var subQ2=makeQuery(id+"F0.imprint","INTERSECT",VERTEX,{"derivedFrom":[subQ1,subQ0]});Q417=makeQuery(id+"F0.imprint","IMPRINT",FACE,{"disambiguationData":[TD([[makeQuery(id+"F0.imprint","IMPRINT",EDGE,{"disambiguationData":[TD([[subQ2,-1.0]])],"derivedFrom":subQ1}),-1.0]])]});}
            var Q418;
            {var subQ0=sQuery(id+"F0.wireOp",EDGE,"E6.5.0");var subQ1=sQuery(id+"F0.wireOp",EDGE,"E5");var subQ2=makeQuery(id+"F0.imprint","INTERSECT",VERTEX,{"derivedFrom":[subQ1,subQ0]});Q418=makeQuery(id+"F0.imprint","IMPRINT",FACE,{"disambiguationData":[TD([[makeQuery(id+"F0.imprint","IMPRINT",EDGE,{"disambiguationData":[TD([[subQ2,-1.0]])],"derivedFrom":subQ1}),-1.0]])]});}
            var Q419;
            {var subQ0=sQuery(id+"F0.wireOp",EDGE,"E9.5.28.0");var subQ1=sQuery(id+"F0.wireOp",EDGE,"E8.3.21.0");var subQ2=makeQuery(id+"F0.imprint","INTERSECT",VERTEX,{"derivedFrom":[subQ1,subQ0]});Q419=makeQuery(id+"F0.imprint","IMPRINT",FACE,{"disambiguationData":[TD([[makeQuery(id+"F0.imprint","IMPRINT",EDGE,{"disambiguationData":[TD([[subQ2,-1.0]])],"derivedFrom":subQ1}),-1.0]])]});}
            var Q420;
            {var subQ0=sQuery(id+"F0.wireOp",EDGE,"E7.5.8.0");var subQ1=sQuery(id+"F0.wireOp",EDGE,"E6.2.1");var subQ2=makeQuery(id+"F0.imprint","INTERSECT",VERTEX,{"derivedFrom":[subQ1,subQ0]});Q420=makeQuery(id+"F0.imprint","IMPRINT",FACE,{"disambiguationData":[TD([[makeQuery(id+"F0.imprint","IMPRINT",EDGE,{"disambiguationData":[TD([[subQ2,-1.0]])],"derivedFrom":subQ1}),-1.0]])]});}
            var Q421;
            {var subQ0=sQuery(id+"F0.wireOp",EDGE,"E8.5.14.0");var subQ1=sQuery(id+"F0.wireOp",EDGE,"E7.3.7.0");var subQ2=makeQuery(id+"F0.imprint","INTERSECT",VERTEX,{"derivedFrom":[subQ1,subQ0]});Q421=makeQuery(id+"F0.imprint","IMPRINT",FACE,{"disambiguationData":[TD([[makeQuery(id+"F0.imprint","IMPRINT",EDGE,{"disambiguationData":[TD([[subQ2,-1.0]])],"derivedFrom":subQ1}),-1.0]])]});}
            var Q422;
            {var subQ0=sQuery(id+"F0.wireOp",EDGE,"E9.5.29.0");var subQ1=sQuery(id+"F0.wireOp",EDGE,"E8.3.20.0");var subQ2=makeQuery(id+"F0.imprint","INTERSECT",VERTEX,{"derivedFrom":[subQ1,subQ0]});Q422=makeQuery(id+"F0.imprint","IMPRINT",FACE,{"disambiguationData":[TD([[makeQuery(id+"F0.imprint","IMPRINT",EDGE,{"disambiguationData":[TD([[subQ2,1.0]])],"derivedFrom":subQ1}),-1.0]])]});}
            var Q423;
            {var subQ0=sQuery(id+"F0.wireOp",EDGE,"E7.5.9.0");var subQ1=sQuery(id+"F0.wireOp",EDGE,"E5");var subQ2=makeQuery(id+"F0.imprint","INTERSECT",VERTEX,{"derivedFrom":[subQ1,subQ0]});Q423=makeQuery(id+"F0.imprint","IMPRINT",FACE,{"disambiguationData":[TD([[makeQuery(id+"F0.imprint","IMPRINT",EDGE,{"disambiguationData":[TD([[subQ2,1.0]])],"derivedFrom":subQ1}),-1.0]])]});}
            var Q424;
            {var subQ0=sQuery(id+"F0.wireOp",EDGE,"E7.5.8.0");var subQ1=sQuery(id+"F0.wireOp",EDGE,"E6.1.1");var subQ2=makeQuery(id+"F0.imprint","INTERSECT",VERTEX,{"derivedFrom":[subQ1,subQ0]});Q424=makeQuery(id+"F0.imprint","IMPRINT",FACE,{"disambiguationData":[TD([[makeQuery(id+"F0.imprint","IMPRINT",EDGE,{"disambiguationData":[TD([[subQ2,-1.0]])],"derivedFrom":subQ1}),-1.0]])]});}
            var Q425;
            {var subQ0=sQuery(id+"F0.wireOp",EDGE,"E9.5.28.0");var subQ1=sQuery(id+"F0.wireOp",EDGE,"E8.3.22.0");var subQ2=makeQuery(id+"F0.imprint","INTERSECT",VERTEX,{"derivedFrom":[subQ1,subQ0]});Q425=makeQuery(id+"F0.imprint","IMPRINT",FACE,{"disambiguationData":[TD([[makeQuery(id+"F0.imprint","IMPRINT",EDGE,{"disambiguationData":[TD([[subQ2,-1.0]])],"derivedFrom":subQ1}),-1.0]])]});}
            extrude(context, id + "F1", {"entities" : qUnion([Q0, Q1, Q2, Q3, Q4, Q5, Q6, Q7, Q8, Q9, Q10, Q11, Q12, Q13, Q14, Q15, Q16, Q17, Q18, Q19, Q20, Q21, Q22, Q23, Q24, Q25, Q26, Q27, Q28, Q29, Q30, Q31, Q32, Q33, Q34, Q35, Q36, Q37, Q38, Q39, Q40, Q41, Q42, Q43, Q44, Q45, Q46, Q47, Q48, Q49, Q50, Q51, Q52, Q53, Q54, Q55, Q56, Q57, Q58, Q59, Q60, Q61, Q62, Q63, Q64, Q65, Q66, Q67, Q68, Q69, Q70, Q71, Q72, Q73, Q74, Q75, Q76, Q77, Q78, Q79, Q80, Q81, Q82, Q83, Q84, Q85, Q86, Q87, Q88, Q89, Q90, Q91, Q92, Q93, Q94, Q95, Q96, Q97, Q98, Q99, Q100, Q101, Q102, Q103, Q104, Q105, Q106, Q107, Q108, Q109, Q110, Q111, Q112, Q113, Q114, Q115, Q116, Q117, Q118, Q119, Q120, Q121, Q122, Q123, Q124, Q125, Q126, Q127, Q128, Q129, Q130, Q131, Q132, Q133, Q134, Q135, Q136, Q137, Q138, Q139, Q140, Q141, Q142, Q143, Q144, Q145, Q146, Q147, Q148, Q149, Q150, Q151, Q152, Q153, Q154, Q155, Q156, Q157, Q158, Q159, Q160, Q161, Q162, Q163, Q164, Q165, Q166, Q167, Q168, Q169, Q170, Q171, Q172, Q173, Q174, Q175, Q176, Q177, Q178, Q179, Q180, Q181, Q182, Q183, Q184, Q185, Q186, Q187, Q188, Q189, Q190, Q191, Q192, Q193, Q194, Q195, Q196, Q197, Q198, Q199, Q200, Q201, Q202, Q203, Q204, Q205, Q206, Q207, Q208, Q209, Q210, Q211, Q212, Q213, Q214, Q215, Q216, Q217, Q218, Q219, Q220, Q221, Q222, Q223, Q224, Q225, Q226, Q227, Q228, Q229, Q230, Q231, Q232, Q233, Q234, Q235, Q236, Q237, Q238, Q239, Q240, Q241, Q242, Q243, Q244, Q245, Q246, Q247, Q248, Q249, Q250, Q251, Q252, Q253, Q254, Q255, Q256, Q257, Q258, Q259, Q260, Q261, Q262, Q263, Q264, Q265, Q266, Q267, Q268, Q269, Q270, Q271, Q272, Q273, Q274, Q275, Q276, Q277, Q278, Q279, Q280, Q281, Q282, Q283, Q284, Q285, Q286, Q287, Q288, Q289, Q290, Q291, Q292, Q293, Q294, Q295, Q296, Q297, Q298, Q299, Q300, Q301, Q302, Q303, Q304, Q305, Q306, Q307, Q308, Q309, Q310, Q311, Q312, Q313, Q314, Q315, Q316, Q317, Q318, Q319, Q320, Q321, Q322, Q323, Q324, Q325, Q326, Q327, Q328, Q329, Q330, Q331, Q332, Q333, Q334, Q335, Q336, Q337, Q338, Q339, Q340, Q341, Q342, Q343, Q344, Q345, Q346, Q347, Q348, Q349, Q350, Q351, Q352, Q353, Q354, Q355, Q356, Q357, Q358, Q359, Q360, Q361, Q362, Q363, Q364, Q365, Q366, Q367, Q368, Q369, Q370, Q371, Q372, Q373, Q374, Q375, Q376, Q377, Q378, Q379, Q380, Q381, Q382, Q383, Q384, Q385, Q386, Q387, Q388, Q389, Q390, Q391, Q392, Q393, Q394, Q395, Q396, Q397, Q398, Q399, Q400, Q401, Q402, Q403, Q404, Q405, Q406, Q407, Q408, Q409, Q410, Q411, Q412, Q413, Q414, Q415, Q416, Q417, Q418, Q419, Q420, Q421, Q422, Q423, Q424, Q425]), "depth" : 6 * mm, "offsetDistance" : 25 * mm});
        }
        {
            var Q0;
            Q0=makeQuery(id+"F1.opExtrude","CAP_FACE",FACE,{"disambiguationData":[OSD([sQuery(id+"F0.wireOp",EDGE,"E0"),sQuery(id+"F0.wireOp",EDGE,"E3"),sQuery(id+"F0.wireOp",EDGE,"E4"),sQuery(id+"F0.wireOp",EDGE,"E5"),sQuery(id+"F0.wireOp",EDGE,"E6.1.0"),sQuery(id+"F0.wireOp",EDGE,"E6.1.1"),sQuery(id+"F0.wireOp",EDGE,"E6.1.2"),sQuery(id+"F0.wireOp",EDGE,"E6.2.0"),sQuery(id+"F0.wireOp",EDGE,"E6.2.1"),sQuery(id+"F0.wireOp",EDGE,"E6.2.2"),sQuery(id+"F0.wireOp",EDGE,"E6.3.0"),sQuery(id+"F0.wireOp",EDGE,"E6.3.1"),sQuery(id+"F0.wireOp",EDGE,"E6.3.2"),sQuery(id+"F0.wireOp",EDGE,"E6.4.0"),sQuery(id+"F0.wireOp",EDGE,"E6.4.1"),sQuery(id+"F0.wireOp",EDGE,"E6.4.2"),sQuery(id+"F0.wireOp",EDGE,"E6.5.0"),sQuery(id+"F0.wireOp",EDGE,"E6.5.1"),sQuery(id+"F0.wireOp",EDGE,"E6.5.2"),sQuery(id+"F0.wireOp",EDGE,"E7.3.6.0"),sQuery(id+"F0.wireOp",EDGE,"E7.5.6.0"),sQuery(id+"F0.wireOp",EDGE,"E7.6.6.0"),sQuery(id+"F0.wireOp",EDGE,"E7.3.7.0"),sQuery(id+"F0.wireOp",EDGE,"E7.5.7.0"),sQuery(id+"F0.wireOp",EDGE,"E7.6.7.0"),sQuery(id+"F0.wireOp",EDGE,"E7.3.8.0"),sQuery(id+"F0.wireOp",EDGE,"E7.5.8.0"),sQuery(id+"F0.wireOp",EDGE,"E7.6.8.0"),sQuery(id+"F0.wireOp",EDGE,"E7.3.9.0"),sQuery(id+"F0.wireOp",EDGE,"E7.5.9.0"),sQuery(id+"F0.wireOp",EDGE,"E7.6.9.0"),sQuery(id+"F0.wireOp",EDGE,"E7.3.10.0"),sQuery(id+"F0.wireOp",EDGE,"E7.5.10.0"),sQuery(id+"F0.wireOp",EDGE,"E7.6.10.0"),sQuery(id+"F0.wireOp",EDGE,"E7.3.11.0"),sQuery(id+"F0.wireOp",EDGE,"E7.5.11.0"),sQuery(id+"F0.wireOp",EDGE,"E7.6.11.0"),sQuery(id+"F0.wireOp",EDGE,"E8.3.12.0"),sQuery(id+"F0.wireOp",EDGE,"E8.5.12.0"),sQuery(id+"F0.wireOp",EDGE,"E8.6.12.0"),sQuery(id+"F0.wireOp",EDGE,"E8.3.13.0"),sQuery(id+"F0.wireOp",EDGE,"E8.5.13.0"),sQuery(id+"F0.wireOp",EDGE,"E8.6.13.0"),sQuery(id+"F0.wireOp",EDGE,"E8.3.14.0"),sQuery(id+"F0.wireOp",EDGE,"E8.5.14.0"),sQuery(id+"F0.wireOp",EDGE,"E8.6.14.0"),sQuery(id+"F0.wireOp",EDGE,"E8.3.15.0"),sQuery(id+"F0.wireOp",EDGE,"E8.5.15.0"),sQuery(id+"F0.wireOp",EDGE,"E8.6.15.0"),sQuery(id+"F0.wireOp",EDGE,"E8.3.16.0"),sQuery(id+"F0.wireOp",EDGE,"E8.5.16.0"),sQuery(id+"F0.wireOp",EDGE,"E8.6.16.0"),sQuery(id+"F0.wireOp",EDGE,"E8.3.17.0"),sQuery(id+"F0.wireOp",EDGE,"E8.5.17.0"),sQuery(id+"F0.wireOp",EDGE,"E8.6.17.0"),sQuery(id+"F0.wireOp",EDGE,"E8.3.18.0"),sQuery(id+"F0.wireOp",EDGE,"E8.5.18.0"),sQuery(id+"F0.wireOp",EDGE,"E8.6.18.0"),sQuery(id+"F0.wireOp",EDGE,"E8.3.19.0"),sQuery(id+"F0.wireOp",EDGE,"E8.5.19.0"),sQuery(id+"F0.wireOp",EDGE,"E8.6.19.0"),sQuery(id+"F0.wireOp",EDGE,"E8.3.20.0"),sQuery(id+"F0.wireOp",EDGE,"E8.5.20.0"),sQuery(id+"F0.wireOp",EDGE,"E8.6.20.0"),sQuery(id+"F0.wireOp",EDGE,"E8.3.21.0"),sQuery(id+"F0.wireOp",EDGE,"E8.5.21.0"),sQuery(id+"F0.wireOp",EDGE,"E8.6.21.0"),sQuery(id+"F0.wireOp",EDGE,"E8.3.22.0"),sQuery(id+"F0.wireOp",EDGE,"E8.5.22.0"),sQuery(id+"F0.wireOp",EDGE,"E8.6.22.0"),sQuery(id+"F0.wireOp",EDGE,"E8.3.23.0"),sQuery(id+"F0.wireOp",EDGE,"E8.5.23.0"),sQuery(id+"F0.wireOp",EDGE,"E8.6.23.0"),sQuery(id+"F0.wireOp",EDGE,"E9.3.24.0"),sQuery(id+"F0.wireOp",EDGE,"E9.5.24.0"),sQuery(id+"F0.wireOp",EDGE,"E9.6.24.0"),sQuery(id+"F0.wireOp",EDGE,"E9.3.25.0"),sQuery(id+"F0.wireOp",EDGE,"E9.5.25.0"),sQuery(id+"F0.wireOp",EDGE,"E9.6.25.0"),sQuery(id+"F0.wireOp",EDGE,"E9.3.26.0"),sQuery(id+"F0.wireOp",EDGE,"E9.5.26.0"),sQuery(id+"F0.wireOp",EDGE,"E9.6.26.0"),sQuery(id+"F0.wireOp",EDGE,"E9.3.27.0"),sQuery(id+"F0.wireOp",EDGE,"E9.5.27.0"),sQuery(id+"F0.wireOp",EDGE,"E9.6.27.0"),sQuery(id+"F0.wireOp",EDGE,"E9.3.28.0"),sQuery(id+"F0.wireOp",EDGE,"E9.5.28.0"),sQuery(id+"F0.wireOp",EDGE,"E9.6.28.0"),sQuery(id+"F0.wireOp",EDGE,"E9.3.29.0"),sQuery(id+"F0.wireOp",EDGE,"E9.5.29.0"),sQuery(id+"F0.wireOp",EDGE,"E9.6.29.0")])],"isStart":false});
            var sketch = newSketch(context, id + "F2", { "sketchPlane" : qUnion([Q0])});
            skLineSegment(sketch, "E10.0", {"start": v(-4.33, 2.5) * mm, "end": v(0, 5) * mm});
            skLineSegment(sketch, "E10.1", {"start": v(0, 5) * mm, "end": v(4.33, 2.5) * mm});
            skLineSegment(sketch, "E10.2", {"start": v(4.33, 2.5) * mm, "end": v(4.33, -2.5) * mm});
            skLineSegment(sketch, "E10.3", {"start": v(4.33, -2.5) * mm, "end": v(0, -5) * mm});
            skLineSegment(sketch, "E10.4", {"start": v(0, -5) * mm, "end": v(-4.33, -2.5) * mm});
            skLineSegment(sketch, "E10.5", {"start": v(-4.33, -2.5) * mm, "end": v(-4.33, 2.5) * mm});
            skSolve(sketch);
        }
        {
            var Q0;
            Q0=makeQuery(id+"F2.imprint","IMPRINT",FACE,{"disambiguationData":[TD([[makeQuery(id+"F2.imprint","IMPRINT",EDGE,{"derivedFrom":sQuery(id+"F2.wireOp",EDGE,"E10.0")}),-1.0]])]});
            extrude(context, id + "F3", {"entities" : qUnion([Q0]), "operationType" : NewBodyOperationType.REMOVE, "oppositeDirection" : true, "depth" : 25 * mm, "offsetDistance" : 25 * mm});
        }
        {
            var Q0;
            {var subQ5=sQuery(id+"F0.wireOp",EDGE,"E9.6.24.0");Q0=makeQuery(id+"F0.imprint","IMPRINT",FACE,{"disambiguationData":[TD([[makeQuery(id+"F0.imprint","IMPRINT",EDGE,{"derivedFrom":subQ5}),-1.0]])]});}
            var Q1;
            {var subQ5=sQuery(id+"F0.wireOp",EDGE,"E9.6.25.0");Q1=makeQuery(id+"F0.imprint","IMPRINT",FACE,{"disambiguationData":[TD([[makeQuery(id+"F0.imprint","IMPRINT",EDGE,{"derivedFrom":subQ5}),-1.0]])]});}
            var Q2;
            {var subQ5=sQuery(id+"F0.wireOp",EDGE,"E9.6.26.0");Q2=makeQuery(id+"F0.imprint","IMPRINT",FACE,{"disambiguationData":[TD([[makeQuery(id+"F0.imprint","IMPRINT",EDGE,{"derivedFrom":subQ5}),-1.0]])]});}
            var Q3;
            {var subQ5=sQuery(id+"F0.wireOp",EDGE,"E9.6.27.0");Q3=makeQuery(id+"F0.imprint","IMPRINT",FACE,{"disambiguationData":[TD([[makeQuery(id+"F0.imprint","IMPRINT",EDGE,{"derivedFrom":subQ5}),-1.0]])]});}
            var Q4;
            {var subQ5=sQuery(id+"F0.wireOp",EDGE,"E9.6.28.0");Q4=makeQuery(id+"F0.imprint","IMPRINT",FACE,{"disambiguationData":[TD([[makeQuery(id+"F0.imprint","IMPRINT",EDGE,{"derivedFrom":subQ5}),-1.0]])]});}
            var Q5;
            {var subQ5=sQuery(id+"F0.wireOp",EDGE,"E9.6.29.0");Q5=makeQuery(id+"F0.imprint","IMPRINT",FACE,{"disambiguationData":[TD([[makeQuery(id+"F0.imprint","IMPRINT",EDGE,{"derivedFrom":subQ5}),-1.0]])]});}
            var Q6;
            {var subQ5=sQuery(id+"F0.wireOp",EDGE,"E3");Q6=makeQuery(id+"F0.imprint","IMPRINT",FACE,{"disambiguationData":[TD([[makeQuery(id+"F0.imprint","IMPRINT",EDGE,{"derivedFrom":subQ5}),-1.0]])]});}
            var Q7;
            {var subQ5=sQuery(id+"F0.wireOp",EDGE,"E6.1.2");Q7=makeQuery(id+"F0.imprint","IMPRINT",FACE,{"disambiguationData":[TD([[makeQuery(id+"F0.imprint","IMPRINT",EDGE,{"derivedFrom":subQ5}),-1.0]])]});}
            var Q8;
            {var subQ5=sQuery(id+"F0.wireOp",EDGE,"E6.2.2");Q8=makeQuery(id+"F0.imprint","IMPRINT",FACE,{"disambiguationData":[TD([[makeQuery(id+"F0.imprint","IMPRINT",EDGE,{"derivedFrom":subQ5}),-1.0]])]});}
            var Q9;
            {var subQ5=sQuery(id+"F0.wireOp",EDGE,"E6.3.2");Q9=makeQuery(id+"F0.imprint","IMPRINT",FACE,{"disambiguationData":[TD([[makeQuery(id+"F0.imprint","IMPRINT",EDGE,{"derivedFrom":subQ5}),-1.0]])]});}
            var Q10;
            {var subQ5=sQuery(id+"F0.wireOp",EDGE,"E6.4.2");Q10=makeQuery(id+"F0.imprint","IMPRINT",FACE,{"disambiguationData":[TD([[makeQuery(id+"F0.imprint","IMPRINT",EDGE,{"derivedFrom":subQ5}),-1.0]])]});}
            var Q11;
            {var subQ5=sQuery(id+"F0.wireOp",EDGE,"E6.5.2");Q11=makeQuery(id+"F0.imprint","IMPRINT",FACE,{"disambiguationData":[TD([[makeQuery(id+"F0.imprint","IMPRINT",EDGE,{"derivedFrom":subQ5}),-1.0]])]});}
            var Q12;
            {var subQ5=sQuery(id+"F0.wireOp",EDGE,"E7.6.6.0");Q12=makeQuery(id+"F0.imprint","IMPRINT",FACE,{"disambiguationData":[TD([[makeQuery(id+"F0.imprint","IMPRINT",EDGE,{"derivedFrom":subQ5}),-1.0]])]});}
            var Q13;
            {var subQ5=sQuery(id+"F0.wireOp",EDGE,"E7.6.7.0");Q13=makeQuery(id+"F0.imprint","IMPRINT",FACE,{"disambiguationData":[TD([[makeQuery(id+"F0.imprint","IMPRINT",EDGE,{"derivedFrom":subQ5}),-1.0]])]});}
            var Q14;
            {var subQ5=sQuery(id+"F0.wireOp",EDGE,"E7.6.8.0");Q14=makeQuery(id+"F0.imprint","IMPRINT",FACE,{"disambiguationData":[TD([[makeQuery(id+"F0.imprint","IMPRINT",EDGE,{"derivedFrom":subQ5}),-1.0]])]});}
            var Q15;
            {var subQ5=sQuery(id+"F0.wireOp",EDGE,"E7.6.9.0");Q15=makeQuery(id+"F0.imprint","IMPRINT",FACE,{"disambiguationData":[TD([[makeQuery(id+"F0.imprint","IMPRINT",EDGE,{"derivedFrom":subQ5}),-1.0]])]});}
            var Q16;
            {var subQ5=sQuery(id+"F0.wireOp",EDGE,"E7.6.10.0");Q16=makeQuery(id+"F0.imprint","IMPRINT",FACE,{"disambiguationData":[TD([[makeQuery(id+"F0.imprint","IMPRINT",EDGE,{"derivedFrom":subQ5}),-1.0]])]});}
            var Q17;
            {var subQ5=sQuery(id+"F0.wireOp",EDGE,"E7.6.11.0");Q17=makeQuery(id+"F0.imprint","IMPRINT",FACE,{"disambiguationData":[TD([[makeQuery(id+"F0.imprint","IMPRINT",EDGE,{"derivedFrom":subQ5}),-1.0]])]});}
            var Q18;
            {var subQ5=sQuery(id+"F0.wireOp",EDGE,"E8.6.12.0");Q18=makeQuery(id+"F0.imprint","IMPRINT",FACE,{"disambiguationData":[TD([[makeQuery(id+"F0.imprint","IMPRINT",EDGE,{"derivedFrom":subQ5}),-1.0]])]});}
            var Q19;
            {var subQ5=sQuery(id+"F0.wireOp",EDGE,"E8.6.13.0");Q19=makeQuery(id+"F0.imprint","IMPRINT",FACE,{"disambiguationData":[TD([[makeQuery(id+"F0.imprint","IMPRINT",EDGE,{"derivedFrom":subQ5}),-1.0]])]});}
            var Q20;
            {var subQ5=sQuery(id+"F0.wireOp",EDGE,"E8.6.14.0");Q20=makeQuery(id+"F0.imprint","IMPRINT",FACE,{"disambiguationData":[TD([[makeQuery(id+"F0.imprint","IMPRINT",EDGE,{"derivedFrom":subQ5}),-1.0]])]});}
            var Q21;
            {var subQ5=sQuery(id+"F0.wireOp",EDGE,"E8.6.15.0");Q21=makeQuery(id+"F0.imprint","IMPRINT",FACE,{"disambiguationData":[TD([[makeQuery(id+"F0.imprint","IMPRINT",EDGE,{"derivedFrom":subQ5}),-1.0]])]});}
            var Q22;
            {var subQ5=sQuery(id+"F0.wireOp",EDGE,"E8.6.16.0");Q22=makeQuery(id+"F0.imprint","IMPRINT",FACE,{"disambiguationData":[TD([[makeQuery(id+"F0.imprint","IMPRINT",EDGE,{"derivedFrom":subQ5}),-1.0]])]});}
            var Q23;
            {var subQ5=sQuery(id+"F0.wireOp",EDGE,"E8.6.17.0");Q23=makeQuery(id+"F0.imprint","IMPRINT",FACE,{"disambiguationData":[TD([[makeQuery(id+"F0.imprint","IMPRINT",EDGE,{"derivedFrom":subQ5}),-1.0]])]});}
            var Q24;
            {var subQ5=sQuery(id+"F0.wireOp",EDGE,"E8.6.18.0");Q24=makeQuery(id+"F0.imprint","IMPRINT",FACE,{"disambiguationData":[TD([[makeQuery(id+"F0.imprint","IMPRINT",EDGE,{"derivedFrom":subQ5}),-1.0]])]});}
            var Q25;
            {var subQ5=sQuery(id+"F0.wireOp",EDGE,"E8.6.19.0");Q25=makeQuery(id+"F0.imprint","IMPRINT",FACE,{"disambiguationData":[TD([[makeQuery(id+"F0.imprint","IMPRINT",EDGE,{"derivedFrom":subQ5}),-1.0]])]});}
            var Q26;
            {var subQ5=sQuery(id+"F0.wireOp",EDGE,"E8.6.20.0");Q26=makeQuery(id+"F0.imprint","IMPRINT",FACE,{"disambiguationData":[TD([[makeQuery(id+"F0.imprint","IMPRINT",EDGE,{"derivedFrom":subQ5}),-1.0]])]});}
            var Q27;
            {var subQ5=sQuery(id+"F0.wireOp",EDGE,"E8.6.21.0");Q27=makeQuery(id+"F0.imprint","IMPRINT",FACE,{"disambiguationData":[TD([[makeQuery(id+"F0.imprint","IMPRINT",EDGE,{"derivedFrom":subQ5}),-1.0]])]});}
            var Q28;
            {var subQ5=sQuery(id+"F0.wireOp",EDGE,"E8.6.22.0");Q28=makeQuery(id+"F0.imprint","IMPRINT",FACE,{"disambiguationData":[TD([[makeQuery(id+"F0.imprint","IMPRINT",EDGE,{"derivedFrom":subQ5}),-1.0]])]});}
            var Q29;
            {var subQ5=sQuery(id+"F0.wireOp",EDGE,"E8.6.23.0");Q29=makeQuery(id+"F0.imprint","IMPRINT",FACE,{"disambiguationData":[TD([[makeQuery(id+"F0.imprint","IMPRINT",EDGE,{"derivedFrom":subQ5}),-1.0]])]});}
            extrude(context, id + "F4", {"entities" : qUnion([Q0, Q1, Q2, Q3, Q4, Q5, Q6, Q7, Q8, Q9, Q10, Q11, Q12, Q13, Q14, Q15, Q16, Q17, Q18, Q19, Q20, Q21, Q22, Q23, Q24, Q25, Q26, Q27, Q28, Q29]), "operationType" : NewBodyOperationType.ADD, "oppositeDirection" : true, "depth" : 2 * mm, "offsetDistance" : 25 * mm});
        }
    });
